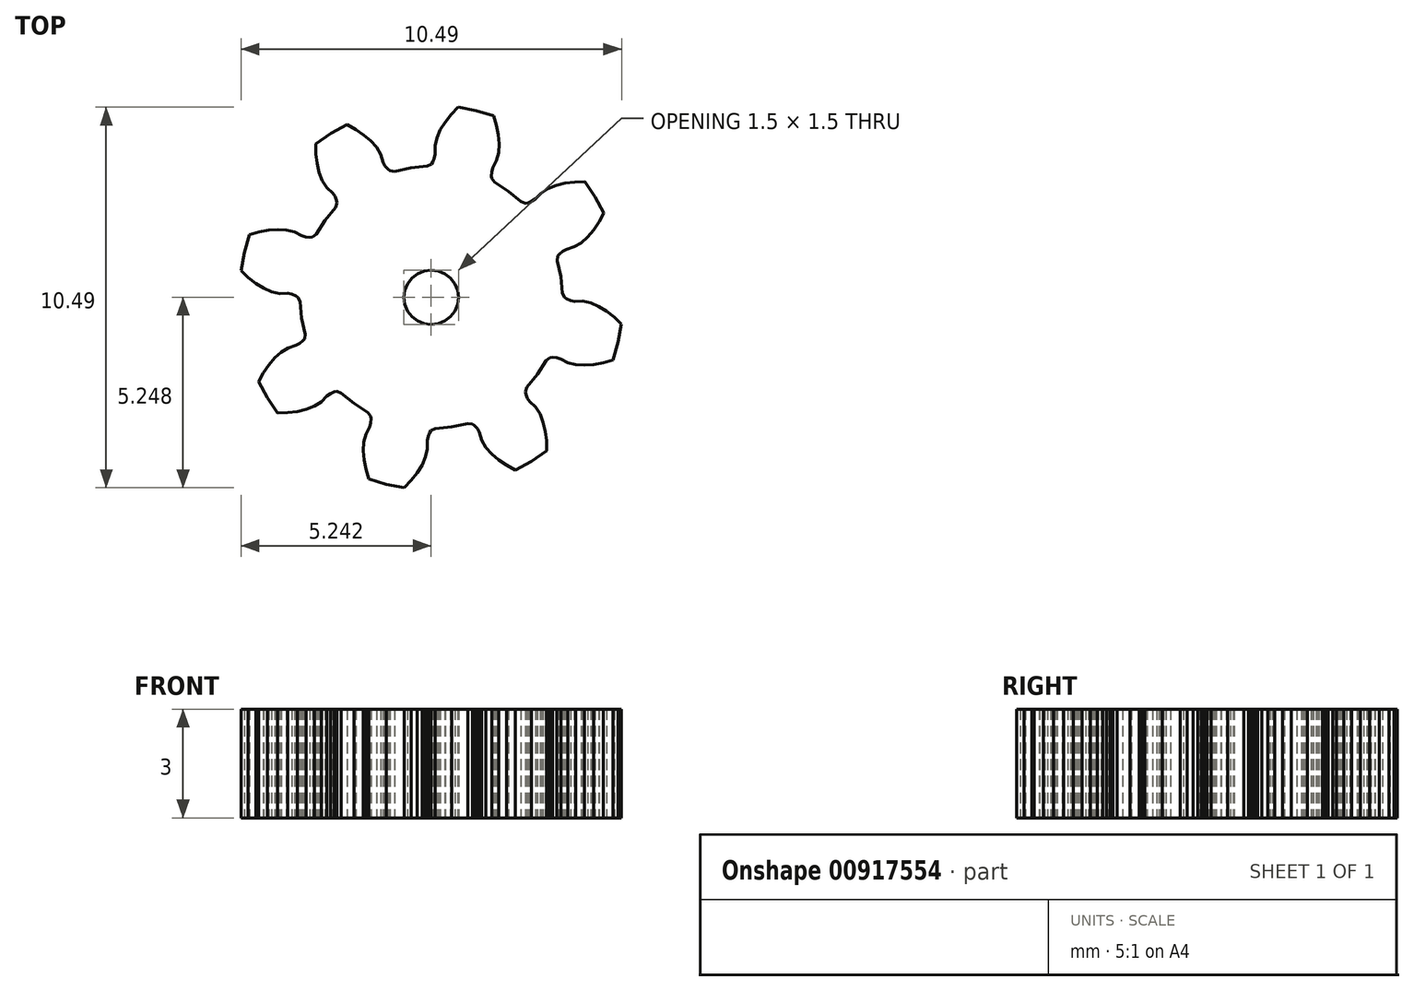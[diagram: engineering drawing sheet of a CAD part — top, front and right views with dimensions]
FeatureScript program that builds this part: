
annotation { "Feature Type Name" : "Feature", "Feature Type Description" : "" }
export const myFeature = defineFeature(function(context is Context, id is Id, definition is map)
    precondition{}
    {
        {
            var Q0;
            Q0=qCreatedBy(makeId("Top.planeOp"),FACE);
            var sketch = newSketch(context, id + "F0", { "sketchPlane" : qUnion([Q0])});
            skLineSegment(sketch, "E0", {"start": v(97.7, 0.47) * mm, "end": v(98.13, 0.32) * mm});
            skLineSegment(sketch, "E1", {"start": v(98.13, 0.32) * mm, "end": v(98.97, 0.02) * mm});
            skLineSegment(sketch, "E2", {"start": v(98.97, 0.02) * mm, "end": v(99.39, -0.14) * mm});
            skLineSegment(sketch, "E3", {"start": v(99.39, -0.14) * mm, "end": v(99.38, -1.27) * mm});
            skLineSegment(sketch, "E4", {"start": v(99.38, -1.27) * mm, "end": v(98.96, -1.43) * mm});
            skLineSegment(sketch, "E5", {"start": v(98.96, -1.43) * mm, "end": v(98.11, -1.72) * mm});
            skLineSegment(sketch, "E6", {"start": v(98.11, -1.72) * mm, "end": v(97.69, -1.86) * mm});
            skLineSegment(sketch, "E7", {"start": v(97.69, -1.86) * mm, "end": v(97.66, -3) * mm});
            skLineSegment(sketch, "E8", {"start": v(97.66, -3) * mm, "end": v(98.08, -3.16) * mm});
            skLineSegment(sketch, "E9", {"start": v(98.08, -3.16) * mm, "end": v(98.9, -3.5) * mm});
            skLineSegment(sketch, "E10", {"start": v(98.9, -3.5) * mm, "end": v(99.32, -3.67) * mm});
            skLineSegment(sketch, "E11", {"start": v(99.32, -3.67) * mm, "end": v(99.28, -4.8) * mm});
            skLineSegment(sketch, "E12", {"start": v(99.28, -4.8) * mm, "end": v(98.85, -4.94) * mm});
            skLineSegment(sketch, "E13", {"start": v(98.85, -4.94) * mm, "end": v(98, -5.2) * mm});
            skLineSegment(sketch, "E14", {"start": v(98, -5.2) * mm, "end": v(97.57, -5.33) * mm});
            skLineSegment(sketch, "E15", {"start": v(97.57, -5.33) * mm, "end": v(97.5, -6.47) * mm});
            skLineSegment(sketch, "E16", {"start": v(97.5, -6.47) * mm, "end": v(97.91, -6.65) * mm});
            skLineSegment(sketch, "E17", {"start": v(97.91, -6.65) * mm, "end": v(98.73, -7) * mm});
            skLineSegment(sketch, "E18", {"start": v(98.73, -7) * mm, "end": v(99.14, -7.2) * mm});
            skLineSegment(sketch, "E19", {"start": v(99.14, -7.2) * mm, "end": v(99.06, -8.32) * mm});
            skLineSegment(sketch, "E20", {"start": v(99.06, -8.32) * mm, "end": v(98.62, -8.45) * mm});
            skLineSegment(sketch, "E21", {"start": v(98.62, -8.45) * mm, "end": v(97.76, -8.68) * mm});
            skLineSegment(sketch, "E22", {"start": v(97.76, -8.68) * mm, "end": v(97.33, -8.8) * mm});
            skLineSegment(sketch, "E23", {"start": v(97.33, -8.8) * mm, "end": v(97.23, -9.93) * mm});
            skLineSegment(sketch, "E24", {"start": v(97.23, -9.93) * mm, "end": v(97.63, -10.12) * mm});
            skLineSegment(sketch, "E25", {"start": v(97.63, -10.12) * mm, "end": v(98.44, -10.5) * mm});
            skLineSegment(sketch, "E26", {"start": v(98.44, -10.5) * mm, "end": v(98.84, -10.7) * mm});
            skLineSegment(sketch, "E27", {"start": v(98.84, -10.7) * mm, "end": v(98.72, -11.83) * mm});
            skLineSegment(sketch, "E28", {"start": v(98.72, -11.83) * mm, "end": v(98.28, -11.94) * mm});
            skLineSegment(sketch, "E29", {"start": v(98.28, -11.94) * mm, "end": v(97.41, -12.15) * mm});
            skLineSegment(sketch, "E30", {"start": v(97.41, -12.15) * mm, "end": v(96.98, -12.24) * mm});
            skLineSegment(sketch, "E31", {"start": v(96.98, -12.24) * mm, "end": v(96.84, -13.38) * mm});
            skLineSegment(sketch, "E32", {"start": v(96.84, -13.38) * mm, "end": v(97.23, -13.58) * mm});
            skLineSegment(sketch, "E33", {"start": v(97.23, -13.58) * mm, "end": v(98.03, -14) * mm});
            skLineSegment(sketch, "E34", {"start": v(98.03, -14) * mm, "end": v(98.42, -14.21) * mm});
            skLineSegment(sketch, "E35", {"start": v(98.42, -14.21) * mm, "end": v(98.26, -15.33) * mm});
            skLineSegment(sketch, "E36", {"start": v(98.26, -15.33) * mm, "end": v(97.82, -15.43) * mm});
            skLineSegment(sketch, "E37", {"start": v(97.82, -15.43) * mm, "end": v(96.95, -15.6) * mm});
            skLineSegment(sketch, "E38", {"start": v(96.95, -15.6) * mm, "end": v(96.5, -15.68) * mm});
            skLineSegment(sketch, "E39", {"start": v(96.5, -15.68) * mm, "end": v(96.33, -16.82) * mm});
            skLineSegment(sketch, "E40", {"start": v(96.33, -16.82) * mm, "end": v(96.72, -17.03) * mm});
            skLineSegment(sketch, "E41", {"start": v(96.72, -17.03) * mm, "end": v(97.5, -17.47) * mm});
            skLineSegment(sketch, "E42", {"start": v(97.5, -17.47) * mm, "end": v(97.88, -17.7) * mm});
            skLineSegment(sketch, "E43", {"start": v(97.88, -17.7) * mm, "end": v(97.69, -18.81) * mm});
            skLineSegment(sketch, "E44", {"start": v(97.69, -18.81) * mm, "end": v(97.25, -18.9) * mm});
            skLineSegment(sketch, "E45", {"start": v(97.25, -18.9) * mm, "end": v(96.36, -19.04) * mm});
            skLineSegment(sketch, "E46", {"start": v(96.36, -19.04) * mm, "end": v(95.93, -19.1) * mm});
            skLineSegment(sketch, "E47", {"start": v(95.93, -19.1) * mm, "end": v(95.7, -20.23) * mm});
            skLineSegment(sketch, "E48", {"start": v(95.7, -20.23) * mm, "end": v(96.09, -20.46) * mm});
            skLineSegment(sketch, "E49", {"start": v(96.09, -20.46) * mm, "end": v(96.85, -20.92) * mm});
            skLineSegment(sketch, "E50", {"start": v(96.85, -20.92) * mm, "end": v(97.23, -21.17) * mm});
            skLineSegment(sketch, "E51", {"start": v(97.23, -21.17) * mm, "end": v(97, -22.27) * mm});
            skLineSegment(sketch, "E52", {"start": v(97, -22.27) * mm, "end": v(96.55, -22.34) * mm});
            skLineSegment(sketch, "E53", {"start": v(96.55, -22.34) * mm, "end": v(95.67, -22.46) * mm});
            skLineSegment(sketch, "E54", {"start": v(95.67, -22.46) * mm, "end": v(95.23, -22.5) * mm});
            skLineSegment(sketch, "E55", {"start": v(95.23, -22.5) * mm, "end": v(94.97, -23.63) * mm});
            skLineSegment(sketch, "E56", {"start": v(94.97, -23.63) * mm, "end": v(95.35, -23.86) * mm});
            skLineSegment(sketch, "E57", {"start": v(95.35, -23.86) * mm, "end": v(96.1, -24.36) * mm});
            skLineSegment(sketch, "E58", {"start": v(96.1, -24.36) * mm, "end": v(96.46, -24.6) * mm});
            skLineSegment(sketch, "E59", {"start": v(96.46, -24.6) * mm, "end": v(96.2, -25.7) * mm});
            skLineSegment(sketch, "E60", {"start": v(96.2, -25.7) * mm, "end": v(95.74, -25.76) * mm});
            skLineSegment(sketch, "E61", {"start": v(95.74, -25.76) * mm, "end": v(94.86, -25.85) * mm});
            skLineSegment(sketch, "E62", {"start": v(94.86, -25.85) * mm, "end": v(94.41, -25.88) * mm});
            skLineSegment(sketch, "E63", {"start": v(94.41, -25.88) * mm, "end": v(94.12, -27) * mm});
            skLineSegment(sketch, "E64", {"start": v(94.12, -27) * mm, "end": v(94.49, -27.24) * mm});
            skLineSegment(sketch, "E65", {"start": v(94.49, -27.24) * mm, "end": v(95.22, -27.76) * mm});
            skLineSegment(sketch, "E66", {"start": v(95.22, -27.76) * mm, "end": v(95.58, -28.02) * mm});
            skLineSegment(sketch, "E67", {"start": v(95.58, -28.02) * mm, "end": v(95.27, -29.11) * mm});
            skLineSegment(sketch, "E68", {"start": v(95.27, -29.11) * mm, "end": v(94.82, -29.15) * mm});
            skLineSegment(sketch, "E69", {"start": v(94.82, -29.15) * mm, "end": v(93.93, -29.2) * mm});
            skLineSegment(sketch, "E70", {"start": v(93.93, -29.2) * mm, "end": v(93.49, -29.23) * mm});
            skLineSegment(sketch, "E71", {"start": v(93.49, -29.23) * mm, "end": v(93.16, -30.33) * mm});
            skLineSegment(sketch, "E72", {"start": v(93.16, -30.33) * mm, "end": v(93.51, -30.59) * mm});
            skLineSegment(sketch, "E73", {"start": v(93.51, -30.59) * mm, "end": v(94.23, -31.13) * mm});
            skLineSegment(sketch, "E74", {"start": v(94.23, -31.13) * mm, "end": v(94.58, -31.4) * mm});
            skLineSegment(sketch, "E75", {"start": v(94.58, -31.4) * mm, "end": v(94.24, -32.48) * mm});
            skLineSegment(sketch, "E76", {"start": v(94.24, -32.48) * mm, "end": v(93.79, -32.5) * mm});
            skLineSegment(sketch, "E77", {"start": v(93.79, -32.5) * mm, "end": v(92.9, -32.54) * mm});
            skLineSegment(sketch, "E78", {"start": v(92.9, -32.54) * mm, "end": v(92.45, -32.54) * mm});
            skLineSegment(sketch, "E79", {"start": v(92.45, -32.54) * mm, "end": v(92.08, -33.63) * mm});
            skLineSegment(sketch, "E80", {"start": v(92.08, -33.63) * mm, "end": v(92.43, -33.9) * mm});
            skLineSegment(sketch, "E81", {"start": v(92.43, -33.9) * mm, "end": v(93.12, -34.47) * mm});
            skLineSegment(sketch, "E82", {"start": v(93.12, -34.47) * mm, "end": v(93.47, -34.76) * mm});
            skLineSegment(sketch, "E83", {"start": v(93.47, -34.76) * mm, "end": v(93.09, -35.82) * mm});
            skLineSegment(sketch, "E84", {"start": v(93.09, -35.82) * mm, "end": v(92.64, -35.83) * mm});
            skLineSegment(sketch, "E85", {"start": v(92.64, -35.83) * mm, "end": v(91.74, -35.83) * mm});
            skLineSegment(sketch, "E86", {"start": v(91.74, -35.83) * mm, "end": v(91.3, -35.82) * mm});
            skLineSegment(sketch, "E87", {"start": v(91.3, -35.82) * mm, "end": v(90.9, -36.9) * mm});
            skLineSegment(sketch, "E88", {"start": v(90.9, -36.9) * mm, "end": v(91.24, -37.18) * mm});
            skLineSegment(sketch, "E89", {"start": v(91.24, -37.18) * mm, "end": v(91.91, -37.76) * mm});
            skLineSegment(sketch, "E90", {"start": v(91.91, -37.76) * mm, "end": v(92.24, -38.07) * mm});
            skLineSegment(sketch, "E91", {"start": v(92.24, -38.07) * mm, "end": v(91.83, -39.12) * mm});
            skLineSegment(sketch, "E92", {"start": v(91.83, -39.12) * mm, "end": v(91.38, -39.1) * mm});
            skLineSegment(sketch, "E93", {"start": v(91.38, -39.1) * mm, "end": v(90.49, -39.08) * mm});
            skLineSegment(sketch, "E94", {"start": v(90.49, -39.08) * mm, "end": v(90.04, -39.05) * mm});
            skLineSegment(sketch, "E95", {"start": v(90.04, -39.05) * mm, "end": v(89.6, -40.11) * mm});
            skLineSegment(sketch, "E96", {"start": v(89.6, -40.11) * mm, "end": v(89.93, -40.41) * mm});
            skLineSegment(sketch, "E97", {"start": v(89.93, -40.41) * mm, "end": v(90.59, -41.02) * mm});
            skLineSegment(sketch, "E98", {"start": v(90.59, -41.02) * mm, "end": v(90.91, -41.33) * mm});
            skLineSegment(sketch, "E99", {"start": v(90.91, -41.33) * mm, "end": v(90.46, -42.37) * mm});
            skLineSegment(sketch, "E100", {"start": v(90.46, -42.37) * mm, "end": v(90.01, -42.35) * mm});
            skLineSegment(sketch, "E101", {"start": v(90.01, -42.35) * mm, "end": v(89.12, -42.28) * mm});
            skLineSegment(sketch, "E102", {"start": v(89.12, -42.28) * mm, "end": v(88.68, -42.24) * mm});
            skLineSegment(sketch, "E103", {"start": v(88.68, -42.24) * mm, "end": v(88.2, -43.3) * mm});
            skLineSegment(sketch, "E104", {"start": v(88.2, -43.3) * mm, "end": v(88.52, -43.6) * mm});
            skLineSegment(sketch, "E105", {"start": v(88.52, -43.6) * mm, "end": v(89.15, -44.23) * mm});
            skLineSegment(sketch, "E106", {"start": v(89.15, -44.23) * mm, "end": v(89.47, -44.55) * mm});
            skLineSegment(sketch, "E107", {"start": v(89.47, -44.55) * mm, "end": v(88.98, -45.57) * mm});
            skLineSegment(sketch, "E108", {"start": v(88.98, -45.57) * mm, "end": v(88.53, -45.53) * mm});
            skLineSegment(sketch, "E109", {"start": v(88.53, -45.53) * mm, "end": v(87.65, -45.44) * mm});
            skLineSegment(sketch, "E110", {"start": v(87.65, -45.44) * mm, "end": v(87.2, -45.39) * mm});
            skLineSegment(sketch, "E111", {"start": v(87.2, -45.39) * mm, "end": v(86.7, -46.42) * mm});
            skLineSegment(sketch, "E112", {"start": v(86.7, -46.42) * mm, "end": v(87, -46.74) * mm});
            skLineSegment(sketch, "E113", {"start": v(87, -46.74) * mm, "end": v(87.62, -47.39) * mm});
            skLineSegment(sketch, "E114", {"start": v(87.62, -47.39) * mm, "end": v(87.92, -47.72) * mm});
            skLineSegment(sketch, "E115", {"start": v(87.92, -47.72) * mm, "end": v(87.4, -48.72) * mm});
            skLineSegment(sketch, "E116", {"start": v(87.4, -48.72) * mm, "end": v(86.95, -48.67) * mm});
            skLineSegment(sketch, "E117", {"start": v(86.95, -48.67) * mm, "end": v(86.07, -48.55) * mm});
            skLineSegment(sketch, "E118", {"start": v(86.07, -48.55) * mm, "end": v(85.63, -48.48) * mm});
            skLineSegment(sketch, "E119", {"start": v(85.63, -48.48) * mm, "end": v(85.08, -49.5) * mm});
            skLineSegment(sketch, "E120", {"start": v(85.08, -49.5) * mm, "end": v(85.38, -49.82) * mm});
            skLineSegment(sketch, "E121", {"start": v(85.38, -49.82) * mm, "end": v(85.97, -50.5) * mm});
            skLineSegment(sketch, "E122", {"start": v(85.97, -50.5) * mm, "end": v(86.26, -50.84) * mm});
            skLineSegment(sketch, "E123", {"start": v(86.26, -50.84) * mm, "end": v(85.7, -51.82) * mm});
            skLineSegment(sketch, "E124", {"start": v(85.7, -51.82) * mm, "end": v(85.26, -51.75) * mm});
            skLineSegment(sketch, "E125", {"start": v(85.26, -51.75) * mm, "end": v(84.38, -51.6) * mm});
            skLineSegment(sketch, "E126", {"start": v(84.38, -51.6) * mm, "end": v(83.95, -51.52) * mm});
            skLineSegment(sketch, "E127", {"start": v(83.95, -51.52) * mm, "end": v(83.37, -52.51) * mm});
            skLineSegment(sketch, "E128", {"start": v(83.37, -52.51) * mm, "end": v(83.66, -52.85) * mm});
            skLineSegment(sketch, "E129", {"start": v(83.66, -52.85) * mm, "end": v(84.22, -53.54) * mm});
            skLineSegment(sketch, "E130", {"start": v(84.22, -53.54) * mm, "end": v(84.5, -53.9) * mm});
            skLineSegment(sketch, "E131", {"start": v(84.5, -53.9) * mm, "end": v(83.92, -54.86) * mm});
            skLineSegment(sketch, "E132", {"start": v(83.92, -54.86) * mm, "end": v(83.47, -54.78) * mm});
            skLineSegment(sketch, "E133", {"start": v(83.47, -54.78) * mm, "end": v(82.6, -54.6) * mm});
            skLineSegment(sketch, "E134", {"start": v(82.6, -54.6) * mm, "end": v(82.17, -54.5) * mm});
            skLineSegment(sketch, "E135", {"start": v(82.17, -54.5) * mm, "end": v(81.56, -55.47) * mm});
            skLineSegment(sketch, "E136", {"start": v(81.56, -55.47) * mm, "end": v(81.83, -55.82) * mm});
            skLineSegment(sketch, "E137", {"start": v(81.83, -55.82) * mm, "end": v(82.37, -56.53) * mm});
            skLineSegment(sketch, "E138", {"start": v(82.37, -56.53) * mm, "end": v(82.64, -56.9) * mm});
            skLineSegment(sketch, "E139", {"start": v(82.64, -56.9) * mm, "end": v(82.02, -57.84) * mm});
            skLineSegment(sketch, "E140", {"start": v(82.02, -57.84) * mm, "end": v(81.58, -57.74) * mm});
            skLineSegment(sketch, "E141", {"start": v(81.58, -57.74) * mm, "end": v(80.72, -57.53) * mm});
            skLineSegment(sketch, "E142", {"start": v(80.72, -57.53) * mm, "end": v(80.29, -57.42) * mm});
            skLineSegment(sketch, "E143", {"start": v(80.29, -57.42) * mm, "end": v(79.64, -58.37) * mm});
            skLineSegment(sketch, "E144", {"start": v(79.64, -58.37) * mm, "end": v(79.9, -58.73) * mm});
            skLineSegment(sketch, "E145", {"start": v(79.9, -58.73) * mm, "end": v(80.43, -59.45) * mm});
            skLineSegment(sketch, "E146", {"start": v(80.43, -59.45) * mm, "end": v(80.68, -59.82) * mm});
            skLineSegment(sketch, "E147", {"start": v(80.68, -59.82) * mm, "end": v(80.03, -60.75) * mm});
            skLineSegment(sketch, "E148", {"start": v(80.03, -60.75) * mm, "end": v(79.6, -60.64) * mm});
            skLineSegment(sketch, "E149", {"start": v(79.6, -60.64) * mm, "end": v(78.73, -60.4) * mm});
            skLineSegment(sketch, "E150", {"start": v(78.73, -60.4) * mm, "end": v(78.3, -60.27) * mm});
            skLineSegment(sketch, "E151", {"start": v(78.3, -60.27) * mm, "end": v(77.63, -61.2) * mm});
            skLineSegment(sketch, "E152", {"start": v(77.63, -61.2) * mm, "end": v(77.89, -61.57) * mm});
            skLineSegment(sketch, "E153", {"start": v(77.89, -61.57) * mm, "end": v(78.38, -62.31) * mm});
            skLineSegment(sketch, "E154", {"start": v(78.38, -62.31) * mm, "end": v(78.62, -62.69) * mm});
            skLineSegment(sketch, "E155", {"start": v(78.62, -62.69) * mm, "end": v(77.94, -63.6) * mm});
            skLineSegment(sketch, "E156", {"start": v(77.94, -63.6) * mm, "end": v(77.51, -63.47) * mm});
            skLineSegment(sketch, "E157", {"start": v(77.51, -63.47) * mm, "end": v(76.66, -63.2) * mm});
            skLineSegment(sketch, "E158", {"start": v(76.66, -63.2) * mm, "end": v(76.24, -63.06) * mm});
            skLineSegment(sketch, "E159", {"start": v(76.24, -63.06) * mm, "end": v(75.53, -63.96) * mm});
            skLineSegment(sketch, "E160", {"start": v(75.53, -63.96) * mm, "end": v(75.77, -64.34) * mm});
            skLineSegment(sketch, "E161", {"start": v(75.77, -64.34) * mm, "end": v(76.24, -65.1) * mm});
            skLineSegment(sketch, "E162", {"start": v(76.24, -65.1) * mm, "end": v(76.47, -65.48) * mm});
            skLineSegment(sketch, "E163", {"start": v(76.47, -65.48) * mm, "end": v(75.76, -66.36) * mm});
            skLineSegment(sketch, "E164", {"start": v(75.76, -66.36) * mm, "end": v(75.33, -66.22) * mm});
            skLineSegment(sketch, "E165", {"start": v(75.33, -66.22) * mm, "end": v(74.49, -65.93) * mm});
            skLineSegment(sketch, "E166", {"start": v(74.49, -65.93) * mm, "end": v(74.07, -65.77) * mm});
            skLineSegment(sketch, "E167", {"start": v(74.07, -65.77) * mm, "end": v(73.34, -66.65) * mm});
            skLineSegment(sketch, "E168", {"start": v(73.34, -66.65) * mm, "end": v(73.56, -67.03) * mm});
            skLineSegment(sketch, "E169", {"start": v(73.56, -67.03) * mm, "end": v(74, -67.81) * mm});
            skLineSegment(sketch, "E170", {"start": v(74, -67.81) * mm, "end": v(74.22, -68.2) * mm});
            skLineSegment(sketch, "E171", {"start": v(74.22, -68.2) * mm, "end": v(73.48, -69.06) * mm});
            skLineSegment(sketch, "E172", {"start": v(73.48, -69.06) * mm, "end": v(73.06, -68.9) * mm});
            skLineSegment(sketch, "E173", {"start": v(73.06, -68.9) * mm, "end": v(72.23, -68.58) * mm});
            skLineSegment(sketch, "E174", {"start": v(72.23, -68.58) * mm, "end": v(71.82, -68.41) * mm});
            skLineSegment(sketch, "E175", {"start": v(71.82, -68.41) * mm, "end": v(71.05, -69.27) * mm});
            skLineSegment(sketch, "E176", {"start": v(71.05, -69.27) * mm, "end": v(71.27, -69.66) * mm});
            skLineSegment(sketch, "E177", {"start": v(71.27, -69.66) * mm, "end": v(71.68, -70.45) * mm});
            skLineSegment(sketch, "E178", {"start": v(71.68, -70.45) * mm, "end": v(71.89, -70.85) * mm});
            skLineSegment(sketch, "E179", {"start": v(71.89, -70.85) * mm, "end": v(71.12, -71.68) * mm});
            skLineSegment(sketch, "E180", {"start": v(71.12, -71.68) * mm, "end": v(70.7, -71.5) * mm});
            skLineSegment(sketch, "E181", {"start": v(70.7, -71.5) * mm, "end": v(69.88, -71.16) * mm});
            skLineSegment(sketch, "E182", {"start": v(69.88, -71.16) * mm, "end": v(69.48, -70.97) * mm});
            skLineSegment(sketch, "E183", {"start": v(69.48, -70.97) * mm, "end": v(68.68, -71.8) * mm});
            skLineSegment(sketch, "E184", {"start": v(68.68, -71.8) * mm, "end": v(68.88, -72.2) * mm});
            skLineSegment(sketch, "E185", {"start": v(68.88, -72.2) * mm, "end": v(69.27, -73) * mm});
            skLineSegment(sketch, "E186", {"start": v(69.27, -73) * mm, "end": v(69.46, -73.41) * mm});
            skLineSegment(sketch, "E187", {"start": v(69.46, -73.41) * mm, "end": v(68.67, -74.22) * mm});
            skLineSegment(sketch, "E188", {"start": v(68.67, -74.22) * mm, "end": v(68.26, -74.03) * mm});
            skLineSegment(sketch, "E189", {"start": v(68.26, -74.03) * mm, "end": v(67.45, -73.65) * mm});
            skLineSegment(sketch, "E190", {"start": v(67.45, -73.65) * mm, "end": v(67.05, -73.46) * mm});
            skLineSegment(sketch, "E191", {"start": v(67.05, -73.46) * mm, "end": v(66.23, -74.26) * mm});
            skLineSegment(sketch, "E192", {"start": v(66.23, -74.26) * mm, "end": v(66.42, -74.66) * mm});
            skLineSegment(sketch, "E193", {"start": v(66.42, -74.66) * mm, "end": v(66.78, -75.48) * mm});
            skLineSegment(sketch, "E194", {"start": v(66.78, -75.48) * mm, "end": v(66.95, -75.9) * mm});
            skLineSegment(sketch, "E195", {"start": v(66.95, -75.9) * mm, "end": v(66.13, -76.67) * mm});
            skLineSegment(sketch, "E196", {"start": v(66.13, -76.67) * mm, "end": v(65.73, -76.47) * mm});
            skLineSegment(sketch, "E197", {"start": v(65.73, -76.47) * mm, "end": v(64.93, -76.07) * mm});
            skLineSegment(sketch, "E198", {"start": v(64.93, -76.07) * mm, "end": v(64.54, -75.86) * mm});
            skLineSegment(sketch, "E199", {"start": v(64.54, -75.86) * mm, "end": v(63.7, -76.63) * mm});
            skLineSegment(sketch, "E200", {"start": v(63.7, -76.63) * mm, "end": v(63.87, -77.04) * mm});
            skLineSegment(sketch, "E201", {"start": v(63.87, -77.04) * mm, "end": v(64.2, -77.87) * mm});
            skLineSegment(sketch, "E202", {"start": v(64.2, -77.87) * mm, "end": v(64.36, -78.29) * mm});
            skLineSegment(sketch, "E203", {"start": v(64.36, -78.29) * mm, "end": v(63.52, -79.04) * mm});
            skLineSegment(sketch, "E204", {"start": v(63.52, -79.04) * mm, "end": v(63.12, -78.83) * mm});
            skLineSegment(sketch, "E205", {"start": v(63.12, -78.83) * mm, "end": v(62.34, -78.4) * mm});
            skLineSegment(sketch, "E206", {"start": v(62.34, -78.4) * mm, "end": v(61.95, -78.17) * mm});
            skLineSegment(sketch, "E207", {"start": v(61.95, -78.17) * mm, "end": v(61.08, -78.92) * mm});
            skLineSegment(sketch, "E208", {"start": v(61.08, -78.92) * mm, "end": v(61.24, -79.33) * mm});
            skLineSegment(sketch, "E209", {"start": v(61.24, -79.33) * mm, "end": v(61.55, -80.17) * mm});
            skLineSegment(sketch, "E210", {"start": v(61.55, -80.17) * mm, "end": v(61.7, -80.6) * mm});
            skLineSegment(sketch, "E211", {"start": v(61.7, -80.6) * mm, "end": v(60.82, -81.31) * mm});
            skLineSegment(sketch, "E212", {"start": v(60.82, -81.31) * mm, "end": v(60.43, -81.1) * mm});
            skLineSegment(sketch, "E213", {"start": v(60.43, -81.1) * mm, "end": v(59.67, -80.63) * mm});
            skLineSegment(sketch, "E214", {"start": v(59.67, -80.63) * mm, "end": v(59.29, -80.4) * mm});
            skLineSegment(sketch, "E215", {"start": v(59.29, -80.4) * mm, "end": v(58.4, -81.11) * mm});
            skLineSegment(sketch, "E216", {"start": v(58.4, -81.11) * mm, "end": v(58.54, -81.53) * mm});
            skLineSegment(sketch, "E217", {"start": v(58.54, -81.53) * mm, "end": v(58.82, -82.38) * mm});
            skLineSegment(sketch, "E218", {"start": v(58.82, -82.38) * mm, "end": v(58.95, -82.81) * mm});
            skLineSegment(sketch, "E219", {"start": v(58.95, -82.81) * mm, "end": v(58.05, -83.5) * mm});
            skLineSegment(sketch, "E220", {"start": v(58.05, -83.5) * mm, "end": v(57.67, -83.26) * mm});
            skLineSegment(sketch, "E221", {"start": v(57.67, -83.26) * mm, "end": v(56.92, -82.78) * mm});
            skLineSegment(sketch, "E222", {"start": v(56.92, -82.78) * mm, "end": v(56.55, -82.53) * mm});
            skLineSegment(sketch, "E223", {"start": v(56.55, -82.53) * mm, "end": v(55.63, -83.22) * mm});
            skLineSegment(sketch, "E224", {"start": v(55.63, -83.22) * mm, "end": v(55.76, -83.64) * mm});
            skLineSegment(sketch, "E225", {"start": v(55.76, -83.64) * mm, "end": v(56.01, -84.5) * mm});
            skLineSegment(sketch, "E226", {"start": v(56.01, -84.5) * mm, "end": v(56.13, -84.93) * mm});
            skLineSegment(sketch, "E227", {"start": v(56.13, -84.93) * mm, "end": v(55.21, -85.6) * mm});
            skLineSegment(sketch, "E228", {"start": v(55.21, -85.6) * mm, "end": v(54.84, -85.34) * mm});
            skLineSegment(sketch, "E229", {"start": v(54.84, -85.34) * mm, "end": v(54.1, -84.83) * mm});
            skLineSegment(sketch, "E230", {"start": v(54.1, -84.83) * mm, "end": v(53.74, -84.57) * mm});
            skLineSegment(sketch, "E231", {"start": v(53.74, -84.57) * mm, "end": v(52.8, -85.23) * mm});
            skLineSegment(sketch, "E232", {"start": v(52.8, -85.23) * mm, "end": v(52.92, -85.66) * mm});
            skLineSegment(sketch, "E233", {"start": v(52.92, -85.66) * mm, "end": v(53.14, -86.52) * mm});
            skLineSegment(sketch, "E234", {"start": v(53.14, -86.52) * mm, "end": v(53.24, -86.96) * mm});
            skLineSegment(sketch, "E235", {"start": v(53.24, -86.96) * mm, "end": v(52.3, -87.59) * mm});
            skLineSegment(sketch, "E236", {"start": v(52.3, -87.59) * mm, "end": v(51.94, -87.33) * mm});
            skLineSegment(sketch, "E237", {"start": v(51.94, -87.33) * mm, "end": v(51.22, -86.8) * mm});
            skLineSegment(sketch, "E238", {"start": v(51.22, -86.8) * mm, "end": v(50.87, -86.52) * mm});
            skLineSegment(sketch, "E239", {"start": v(50.87, -86.52) * mm, "end": v(49.9, -87.14) * mm});
            skLineSegment(sketch, "E240", {"start": v(49.9, -87.14) * mm, "end": v(50, -87.57) * mm});
            skLineSegment(sketch, "E241", {"start": v(50, -87.57) * mm, "end": v(50.2, -88.45) * mm});
            skLineSegment(sketch, "E242", {"start": v(50.2, -88.45) * mm, "end": v(50.29, -88.89) * mm});
            skLineSegment(sketch, "E243", {"start": v(50.29, -88.89) * mm, "end": v(49.33, -89.48) * mm});
            skLineSegment(sketch, "E244", {"start": v(49.33, -89.48) * mm, "end": v(48.97, -89.21) * mm});
            skLineSegment(sketch, "E245", {"start": v(48.97, -89.21) * mm, "end": v(48.27, -88.65) * mm});
            skLineSegment(sketch, "E246", {"start": v(48.27, -88.65) * mm, "end": v(47.93, -88.37) * mm});
            skLineSegment(sketch, "E247", {"start": v(47.93, -88.37) * mm, "end": v(46.95, -88.96) * mm});
            skLineSegment(sketch, "E248", {"start": v(46.95, -88.96) * mm, "end": v(47.03, -89.4) * mm});
            skLineSegment(sketch, "E249", {"start": v(47.03, -89.4) * mm, "end": v(47.2, -90.27) * mm});
            skLineSegment(sketch, "E250", {"start": v(47.2, -90.27) * mm, "end": v(47.27, -90.72) * mm});
            skLineSegment(sketch, "E251", {"start": v(47.27, -90.72) * mm, "end": v(46.3, -91.28) * mm});
            skLineSegment(sketch, "E252", {"start": v(46.3, -91.28) * mm, "end": v(45.94, -91) * mm});
            skLineSegment(sketch, "E253", {"start": v(45.94, -91) * mm, "end": v(45.26, -90.41) * mm});
            skLineSegment(sketch, "E254", {"start": v(45.26, -90.41) * mm, "end": v(44.93, -90.12) * mm});
            skLineSegment(sketch, "E255", {"start": v(44.93, -90.12) * mm, "end": v(43.93, -90.67) * mm});
            skLineSegment(sketch, "E256", {"start": v(43.93, -90.67) * mm, "end": v(44, -91.11) * mm});
            skLineSegment(sketch, "E257", {"start": v(44, -91.11) * mm, "end": v(44.13, -92) * mm});
            skLineSegment(sketch, "E258", {"start": v(44.13, -92) * mm, "end": v(44.2, -92.44) * mm});
            skLineSegment(sketch, "E259", {"start": v(44.2, -92.44) * mm, "end": v(43.2, -92.97) * mm});
            skLineSegment(sketch, "E260", {"start": v(43.2, -92.97) * mm, "end": v(42.86, -92.67) * mm});
            skLineSegment(sketch, "E261", {"start": v(42.86, -92.67) * mm, "end": v(42.2, -92.07) * mm});
            skLineSegment(sketch, "E262", {"start": v(42.2, -92.07) * mm, "end": v(41.88, -91.77) * mm});
            skLineSegment(sketch, "E263", {"start": v(41.88, -91.77) * mm, "end": v(40.85, -92.29) * mm});
            skLineSegment(sketch, "E264", {"start": v(40.85, -92.29) * mm, "end": v(40.91, -92.73) * mm});
            skLineSegment(sketch, "E265", {"start": v(40.91, -92.73) * mm, "end": v(41.02, -93.62) * mm});
            skLineSegment(sketch, "E266", {"start": v(41.02, -93.62) * mm, "end": v(41.06, -94.06) * mm});
            skLineSegment(sketch, "E267", {"start": v(41.06, -94.06) * mm, "end": v(40.04, -94.56) * mm});
            skLineSegment(sketch, "E268", {"start": v(40.04, -94.56) * mm, "end": v(39.72, -94.25) * mm});
            skLineSegment(sketch, "E269", {"start": v(39.72, -94.25) * mm, "end": v(39.08, -93.63) * mm});
            skLineSegment(sketch, "E270", {"start": v(39.08, -93.63) * mm, "end": v(38.77, -93.3) * mm});
            skLineSegment(sketch, "E271", {"start": v(38.77, -93.3) * mm, "end": v(37.73, -93.8) * mm});
            skLineSegment(sketch, "E272", {"start": v(37.73, -93.8) * mm, "end": v(37.77, -94.24) * mm});
            skLineSegment(sketch, "E273", {"start": v(37.77, -94.24) * mm, "end": v(37.84, -95.13) * mm});
            skLineSegment(sketch, "E274", {"start": v(37.84, -95.13) * mm, "end": v(37.87, -95.58) * mm});
            skLineSegment(sketch, "E275", {"start": v(37.87, -95.58) * mm, "end": v(36.84, -96.04) * mm});
            skLineSegment(sketch, "E276", {"start": v(36.84, -96.04) * mm, "end": v(36.53, -95.72) * mm});
            skLineSegment(sketch, "E277", {"start": v(36.53, -95.72) * mm, "end": v(35.9, -95.07) * mm});
            skLineSegment(sketch, "E278", {"start": v(35.9, -95.07) * mm, "end": v(35.6, -94.75) * mm});
            skLineSegment(sketch, "E279", {"start": v(35.6, -94.75) * mm, "end": v(34.55, -95.2) * mm});
            skLineSegment(sketch, "E280", {"start": v(34.55, -95.2) * mm, "end": v(34.58, -95.64) * mm});
            skLineSegment(sketch, "E281", {"start": v(34.58, -95.64) * mm, "end": v(34.62, -96.54) * mm});
            skLineSegment(sketch, "E282", {"start": v(34.62, -96.54) * mm, "end": v(34.64, -96.98) * mm});
            skLineSegment(sketch, "E283", {"start": v(34.64, -96.98) * mm, "end": v(33.6, -97.41) * mm});
            skLineSegment(sketch, "E284", {"start": v(33.6, -97.41) * mm, "end": v(33.29, -97.08) * mm});
            skLineSegment(sketch, "E285", {"start": v(33.29, -97.08) * mm, "end": v(32.7, -96.42) * mm});
            skLineSegment(sketch, "E286", {"start": v(32.7, -96.42) * mm, "end": v(32.4, -96.08) * mm});
            skLineSegment(sketch, "E287", {"start": v(32.4, -96.08) * mm, "end": v(31.33, -96.5) * mm});
            skLineSegment(sketch, "E288", {"start": v(31.33, -96.5) * mm, "end": v(31.35, -96.94) * mm});
            skLineSegment(sketch, "E289", {"start": v(31.35, -96.94) * mm, "end": v(31.36, -97.83) * mm});
            skLineSegment(sketch, "E290", {"start": v(31.36, -97.83) * mm, "end": v(31.36, -98.28) * mm});
            skLineSegment(sketch, "E291", {"start": v(31.36, -98.28) * mm, "end": v(30.3, -98.67) * mm});
            skLineSegment(sketch, "E292", {"start": v(30.3, -98.67) * mm, "end": v(30, -98.33) * mm});
            skLineSegment(sketch, "E293", {"start": v(30, -98.33) * mm, "end": v(29.43, -97.65) * mm});
            skLineSegment(sketch, "E294", {"start": v(29.43, -97.65) * mm, "end": v(29.15, -97.3) * mm});
            skLineSegment(sketch, "E295", {"start": v(29.15, -97.3) * mm, "end": v(28.07, -97.68) * mm});
            skLineSegment(sketch, "E296", {"start": v(28.07, -97.68) * mm, "end": v(28.07, -98.13) * mm});
            skLineSegment(sketch, "E297", {"start": v(28.07, -98.13) * mm, "end": v(28.05, -99.02) * mm});
            skLineSegment(sketch, "E298", {"start": v(28.05, -99.02) * mm, "end": v(28.03, -99.47) * mm});
            skLineSegment(sketch, "E299", {"start": v(28.03, -99.47) * mm, "end": v(26.96, -99.83) * mm});
            skLineSegment(sketch, "E300", {"start": v(26.96, -99.83) * mm, "end": v(26.68, -99.48) * mm});
            skLineSegment(sketch, "E301", {"start": v(26.68, -99.48) * mm, "end": v(26.13, -98.77) * mm});
            skLineSegment(sketch, "E302", {"start": v(26.13, -98.77) * mm, "end": v(25.86, -98.42) * mm});
            skLineSegment(sketch, "E303", {"start": v(25.86, -98.42) * mm, "end": v(24.77, -98.76) * mm});
            skLineSegment(sketch, "E304", {"start": v(24.77, -98.76) * mm, "end": v(24.75, -99.2) * mm});
            skLineSegment(sketch, "E305", {"start": v(24.75, -99.2) * mm, "end": v(24.7, -100.1) * mm});
            skLineSegment(sketch, "E306", {"start": v(24.7, -100.1) * mm, "end": v(24.67, -100.54) * mm});
            skLineSegment(sketch, "E307", {"start": v(24.67, -100.54) * mm, "end": v(23.6, -100.86) * mm});
            skLineSegment(sketch, "E308", {"start": v(23.6, -100.86) * mm, "end": v(23.32, -100.5) * mm});
            skLineSegment(sketch, "E309", {"start": v(23.32, -100.5) * mm, "end": v(22.8, -99.78) * mm});
            skLineSegment(sketch, "E310", {"start": v(22.8, -99.78) * mm, "end": v(22.54, -99.42) * mm});
            skLineSegment(sketch, "E311", {"start": v(22.54, -99.42) * mm, "end": v(21.43, -99.72) * mm});
            skLineSegment(sketch, "E312", {"start": v(21.43, -99.72) * mm, "end": v(21.4, -100.17) * mm});
            skLineSegment(sketch, "E313", {"start": v(21.4, -100.17) * mm, "end": v(21.33, -101.06) * mm});
            skLineSegment(sketch, "E314", {"start": v(21.33, -101.06) * mm, "end": v(21.28, -101.5) * mm});
            skLineSegment(sketch, "E315", {"start": v(21.28, -101.5) * mm, "end": v(20.19, -101.79) * mm});
            skLineSegment(sketch, "E316", {"start": v(20.19, -101.79) * mm, "end": v(19.93, -101.42) * mm});
            skLineSegment(sketch, "E317", {"start": v(19.93, -101.42) * mm, "end": v(19.43, -100.68) * mm});
            skLineSegment(sketch, "E318", {"start": v(19.43, -100.68) * mm, "end": v(19.18, -100.3) * mm});
            skLineSegment(sketch, "E319", {"start": v(19.18, -100.3) * mm, "end": v(18.07, -100.58) * mm});
            skLineSegment(sketch, "E320", {"start": v(18.07, -100.58) * mm, "end": v(18.02, -101.02) * mm});
            skLineSegment(sketch, "E321", {"start": v(18.02, -101.02) * mm, "end": v(17.92, -101.9) * mm});
            skLineSegment(sketch, "E322", {"start": v(17.92, -101.9) * mm, "end": v(17.85, -102.35) * mm});
            skLineSegment(sketch, "E323", {"start": v(17.85, -102.35) * mm, "end": v(16.75, -102.6) * mm});
            skLineSegment(sketch, "E324", {"start": v(16.75, -102.6) * mm, "end": v(16.5, -102.22) * mm});
            skLineSegment(sketch, "E325", {"start": v(16.5, -102.22) * mm, "end": v(16.03, -101.46) * mm});
            skLineSegment(sketch, "E326", {"start": v(16.03, -101.46) * mm, "end": v(15.8, -101.08) * mm});
            skLineSegment(sketch, "E327", {"start": v(15.8, -101.08) * mm, "end": v(14.68, -101.32) * mm});
            skLineSegment(sketch, "E328", {"start": v(14.68, -101.32) * mm, "end": v(14.62, -101.76) * mm});
            skLineSegment(sketch, "E329", {"start": v(14.62, -101.76) * mm, "end": v(14.48, -102.64) * mm});
            skLineSegment(sketch, "E330", {"start": v(14.48, -102.64) * mm, "end": v(14.4, -103.08) * mm});
            skLineSegment(sketch, "E331", {"start": v(14.4, -103.08) * mm, "end": v(13.3, -103.3) * mm});
            skLineSegment(sketch, "E332", {"start": v(13.3, -103.3) * mm, "end": v(13.06, -102.9) * mm});
            skLineSegment(sketch, "E333", {"start": v(13.06, -102.9) * mm, "end": v(12.6, -102.13) * mm});
            skLineSegment(sketch, "E334", {"start": v(12.6, -102.13) * mm, "end": v(12.4, -101.75) * mm});
            skLineSegment(sketch, "E335", {"start": v(12.4, -101.75) * mm, "end": v(11.26, -101.94) * mm});
            skLineSegment(sketch, "E336", {"start": v(11.26, -101.94) * mm, "end": v(11.19, -102.38) * mm});
            skLineSegment(sketch, "E337", {"start": v(11.19, -102.38) * mm, "end": v(11.02, -103.26) * mm});
            skLineSegment(sketch, "E338", {"start": v(11.02, -103.26) * mm, "end": v(10.93, -103.7) * mm});
            skLineSegment(sketch, "E339", {"start": v(10.93, -103.7) * mm, "end": v(9.81, -103.87) * mm});
            skLineSegment(sketch, "E340", {"start": v(9.81, -103.87) * mm, "end": v(9.6, -103.48) * mm});
            skLineSegment(sketch, "E341", {"start": v(9.6, -103.48) * mm, "end": v(9.17, -102.69) * mm});
            skLineSegment(sketch, "E342", {"start": v(9.17, -102.69) * mm, "end": v(8.97, -102.3) * mm});
            skLineSegment(sketch, "E343", {"start": v(8.97, -102.3) * mm, "end": v(7.83, -102.45) * mm});
            skLineSegment(sketch, "E344", {"start": v(7.83, -102.45) * mm, "end": v(7.74, -102.89) * mm});
            skLineSegment(sketch, "E345", {"start": v(7.74, -102.89) * mm, "end": v(7.54, -103.76) * mm});
            skLineSegment(sketch, "E346", {"start": v(7.54, -103.76) * mm, "end": v(7.44, -104.2) * mm});
            skLineSegment(sketch, "E347", {"start": v(7.44, -104.2) * mm, "end": v(6.31, -104.33) * mm});
            skLineSegment(sketch, "E348", {"start": v(6.31, -104.33) * mm, "end": v(6.1, -103.93) * mm});
            skLineSegment(sketch, "E349", {"start": v(6.1, -103.93) * mm, "end": v(5.71, -103.13) * mm});
            skLineSegment(sketch, "E350", {"start": v(5.71, -103.13) * mm, "end": v(5.52, -102.73) * mm});
            skLineSegment(sketch, "E351", {"start": v(5.52, -102.73) * mm, "end": v(4.38, -102.84) * mm});
            skLineSegment(sketch, "E352", {"start": v(4.38, -102.84) * mm, "end": v(4.27, -103.28) * mm});
            skLineSegment(sketch, "E353", {"start": v(4.27, -103.28) * mm, "end": v(4.05, -104.14) * mm});
            skLineSegment(sketch, "E354", {"start": v(4.05, -104.14) * mm, "end": v(3.93, -104.57) * mm});
            skLineSegment(sketch, "E355", {"start": v(3.93, -104.57) * mm, "end": v(2.8, -104.67) * mm});
            skLineSegment(sketch, "E356", {"start": v(2.8, -104.67) * mm, "end": v(2.6, -104.26) * mm});
            skLineSegment(sketch, "E357", {"start": v(2.6, -104.26) * mm, "end": v(2.24, -103.45) * mm});
            skLineSegment(sketch, "E358", {"start": v(2.24, -103.45) * mm, "end": v(2.06, -103.04) * mm});
            skLineSegment(sketch, "E359", {"start": v(2.06, -103.04) * mm, "end": v(0.92, -103.12) * mm});
            skLineSegment(sketch, "E360", {"start": v(0.92, -103.12) * mm, "end": v(0.8, -103.55) * mm});
            skLineSegment(sketch, "E361", {"start": v(0.8, -103.55) * mm, "end": v(0.55, -104.4) * mm});
            skLineSegment(sketch, "E362", {"start": v(0.55, -104.4) * mm, "end": v(0.4, -104.84) * mm});
            skLineSegment(sketch, "E363", {"start": v(0.4, -104.84) * mm, "end": v(-0.72, -104.9) * mm});
            skLineSegment(sketch, "E364", {"start": v(-0.72, -104.9) * mm, "end": v(-0.9, -104.48) * mm});
            skLineSegment(sketch, "E365", {"start": v(-0.9, -104.48) * mm, "end": v(-1.24, -103.66) * mm});
            skLineSegment(sketch, "E366", {"start": v(-1.24, -103.66) * mm, "end": v(-1.4, -103.24) * mm});
            skLineSegment(sketch, "E367", {"start": v(-1.4, -103.24) * mm, "end": v(-2.55, -103.28) * mm});
            skLineSegment(sketch, "E368", {"start": v(-2.55, -103.28) * mm, "end": v(-2.68, -103.7) * mm});
            skLineSegment(sketch, "E369", {"start": v(-2.68, -103.7) * mm, "end": v(-2.97, -104.56) * mm});
            skLineSegment(sketch, "E370", {"start": v(-2.97, -104.56) * mm, "end": v(-3.12, -104.98) * mm});
            skLineSegment(sketch, "E371", {"start": v(-3.12, -104.98) * mm, "end": v(-4.25, -105) * mm});
            skLineSegment(sketch, "E372", {"start": v(-4.25, -105) * mm, "end": v(-4.41, -104.58) * mm});
            skLineSegment(sketch, "E373", {"start": v(-4.41, -104.58) * mm, "end": v(-4.72, -103.75) * mm});
            skLineSegment(sketch, "E374", {"start": v(-4.72, -103.75) * mm, "end": v(-4.87, -103.33) * mm});
            skLineSegment(sketch, "E375", {"start": v(-4.87, -103.33) * mm, "end": v(-6.02, -103.33) * mm});
            skLineSegment(sketch, "E376", {"start": v(-6.02, -103.33) * mm, "end": v(-6.17, -103.75) * mm});
            skLineSegment(sketch, "E377", {"start": v(-6.17, -103.75) * mm, "end": v(-6.48, -104.59) * mm});
            skLineSegment(sketch, "E378", {"start": v(-6.48, -104.59) * mm, "end": v(-6.64, -105) * mm});
            skLineSegment(sketch, "E379", {"start": v(-6.64, -105) * mm, "end": v(-7.77, -104.99) * mm});
            skLineSegment(sketch, "E380", {"start": v(-7.77, -104.99) * mm, "end": v(-7.92, -104.56) * mm});
            skLineSegment(sketch, "E381", {"start": v(-7.92, -104.56) * mm, "end": v(-8.21, -103.72) * mm});
            skLineSegment(sketch, "E382", {"start": v(-8.21, -103.72) * mm, "end": v(-8.34, -103.3) * mm});
            skLineSegment(sketch, "E383", {"start": v(-8.34, -103.3) * mm, "end": v(-9.5, -103.26) * mm});
            skLineSegment(sketch, "E384", {"start": v(-9.5, -103.26) * mm, "end": v(-9.65, -103.67) * mm});
            skLineSegment(sketch, "E385", {"start": v(-9.65, -103.67) * mm, "end": v(-10, -104.5) * mm});
            skLineSegment(sketch, "E386", {"start": v(-10, -104.5) * mm, "end": v(-10.17, -104.91) * mm});
            skLineSegment(sketch, "E387", {"start": v(-10.17, -104.91) * mm, "end": v(-11.3, -104.86) * mm});
            skLineSegment(sketch, "E388", {"start": v(-11.3, -104.86) * mm, "end": v(-11.44, -104.43) * mm});
            skLineSegment(sketch, "E389", {"start": v(-11.44, -104.43) * mm, "end": v(-11.7, -103.57) * mm});
            skLineSegment(sketch, "E390", {"start": v(-11.7, -103.57) * mm, "end": v(-11.81, -103.14) * mm});
            skLineSegment(sketch, "E391", {"start": v(-11.81, -103.14) * mm, "end": v(-12.96, -103.07) * mm});
            skLineSegment(sketch, "E392", {"start": v(-12.96, -103.07) * mm, "end": v(-13.13, -103.48) * mm});
            skLineSegment(sketch, "E393", {"start": v(-13.13, -103.48) * mm, "end": v(-13.5, -104.3) * mm});
            skLineSegment(sketch, "E394", {"start": v(-13.5, -104.3) * mm, "end": v(-13.7, -104.7) * mm});
            skLineSegment(sketch, "E395", {"start": v(-13.7, -104.7) * mm, "end": v(-14.82, -104.6) * mm});
            skLineSegment(sketch, "E396", {"start": v(-14.82, -104.6) * mm, "end": v(-14.94, -104.17) * mm});
            skLineSegment(sketch, "E397", {"start": v(-14.94, -104.17) * mm, "end": v(-15.17, -103.3) * mm});
            skLineSegment(sketch, "E398", {"start": v(-15.17, -103.3) * mm, "end": v(-15.27, -102.88) * mm});
            skLineSegment(sketch, "E399", {"start": v(-15.27, -102.88) * mm, "end": v(-16.42, -102.76) * mm});
            skLineSegment(sketch, "E400", {"start": v(-16.42, -102.76) * mm, "end": v(-16.6, -103.17) * mm});
            skLineSegment(sketch, "E401", {"start": v(-16.6, -103.17) * mm, "end": v(-17, -103.97) * mm});
            skLineSegment(sketch, "E402", {"start": v(-17, -103.97) * mm, "end": v(-17.2, -104.37) * mm});
            skLineSegment(sketch, "E403", {"start": v(-17.2, -104.37) * mm, "end": v(-18.33, -104.24) * mm});
            skLineSegment(sketch, "E404", {"start": v(-18.33, -104.24) * mm, "end": v(-18.43, -103.8) * mm});
            skLineSegment(sketch, "E405", {"start": v(-18.43, -103.8) * mm, "end": v(-18.63, -102.93) * mm});
            skLineSegment(sketch, "E406", {"start": v(-18.63, -102.93) * mm, "end": v(-18.72, -102.5) * mm});
            skLineSegment(sketch, "E407", {"start": v(-18.72, -102.5) * mm, "end": v(-19.86, -102.34) * mm});
            skLineSegment(sketch, "E408", {"start": v(-19.86, -102.34) * mm, "end": v(-20.06, -102.74) * mm});
            skLineSegment(sketch, "E409", {"start": v(-20.06, -102.74) * mm, "end": v(-20.49, -103.53) * mm});
            skLineSegment(sketch, "E410", {"start": v(-20.49, -103.53) * mm, "end": v(-20.7, -103.92) * mm});
            skLineSegment(sketch, "E411", {"start": v(-20.7, -103.92) * mm, "end": v(-21.82, -103.75) * mm});
            skLineSegment(sketch, "E412", {"start": v(-21.82, -103.75) * mm, "end": v(-21.91, -103.31) * mm});
            skLineSegment(sketch, "E413", {"start": v(-21.91, -103.31) * mm, "end": v(-22.08, -102.43) * mm});
            skLineSegment(sketch, "E414", {"start": v(-22.08, -102.43) * mm, "end": v(-22.16, -102) * mm});
            skLineSegment(sketch, "E415", {"start": v(-22.16, -102) * mm, "end": v(-23.3, -101.8) * mm});
            skLineSegment(sketch, "E416", {"start": v(-23.3, -101.8) * mm, "end": v(-23.5, -102.2) * mm});
            skLineSegment(sketch, "E417", {"start": v(-23.5, -102.2) * mm, "end": v(-23.95, -102.97) * mm});
            skLineSegment(sketch, "E418", {"start": v(-23.95, -102.97) * mm, "end": v(-24.19, -103.35) * mm});
            skLineSegment(sketch, "E419", {"start": v(-24.19, -103.35) * mm, "end": v(-25.3, -103.15) * mm});
            skLineSegment(sketch, "E420", {"start": v(-25.3, -103.15) * mm, "end": v(-25.38, -102.7) * mm});
            skLineSegment(sketch, "E421", {"start": v(-25.38, -102.7) * mm, "end": v(-25.52, -101.82) * mm});
            skLineSegment(sketch, "E422", {"start": v(-25.52, -101.82) * mm, "end": v(-25.58, -101.38) * mm});
            skLineSegment(sketch, "E423", {"start": v(-25.58, -101.38) * mm, "end": v(-26.7, -101.16) * mm});
            skLineSegment(sketch, "E424", {"start": v(-26.7, -101.16) * mm, "end": v(-26.93, -101.54) * mm});
            skLineSegment(sketch, "E425", {"start": v(-26.93, -101.54) * mm, "end": v(-27.4, -102.3) * mm});
            skLineSegment(sketch, "E426", {"start": v(-27.4, -102.3) * mm, "end": v(-27.65, -102.67) * mm});
            skLineSegment(sketch, "E427", {"start": v(-27.65, -102.67) * mm, "end": v(-28.75, -102.43) * mm});
            skLineSegment(sketch, "E428", {"start": v(-28.75, -102.43) * mm, "end": v(-28.82, -101.98) * mm});
            skLineSegment(sketch, "E429", {"start": v(-28.82, -101.98) * mm, "end": v(-28.93, -101.1) * mm});
            skLineSegment(sketch, "E430", {"start": v(-28.93, -101.1) * mm, "end": v(-28.97, -100.66) * mm});
            skLineSegment(sketch, "E431", {"start": v(-28.97, -100.66) * mm, "end": v(-30.09, -100.4) * mm});
            skLineSegment(sketch, "E432", {"start": v(-30.09, -100.4) * mm, "end": v(-30.33, -100.76) * mm});
            skLineSegment(sketch, "E433", {"start": v(-30.33, -100.76) * mm, "end": v(-30.83, -101.5) * mm});
            skLineSegment(sketch, "E434", {"start": v(-30.83, -101.5) * mm, "end": v(-31.08, -101.87) * mm});
            skLineSegment(sketch, "E435", {"start": v(-31.08, -101.87) * mm, "end": v(-32.18, -101.6) * mm});
            skLineSegment(sketch, "E436", {"start": v(-32.18, -101.6) * mm, "end": v(-32.23, -101.15) * mm});
            skLineSegment(sketch, "E437", {"start": v(-32.23, -101.15) * mm, "end": v(-32.3, -100.26) * mm});
            skLineSegment(sketch, "E438", {"start": v(-32.3, -100.26) * mm, "end": v(-32.34, -99.81) * mm});
            skLineSegment(sketch, "E439", {"start": v(-32.34, -99.81) * mm, "end": v(-33.45, -99.51) * mm});
            skLineSegment(sketch, "E440", {"start": v(-33.45, -99.51) * mm, "end": v(-33.7, -99.88) * mm});
            skLineSegment(sketch, "E441", {"start": v(-33.7, -99.88) * mm, "end": v(-34.22, -100.6) * mm});
            skLineSegment(sketch, "E442", {"start": v(-34.22, -100.6) * mm, "end": v(-34.5, -100.96) * mm});
            skLineSegment(sketch, "E443", {"start": v(-34.5, -100.96) * mm, "end": v(-35.58, -100.65) * mm});
            skLineSegment(sketch, "E444", {"start": v(-35.58, -100.65) * mm, "end": v(-35.61, -100.2) * mm});
            skLineSegment(sketch, "E445", {"start": v(-35.61, -100.2) * mm, "end": v(-35.66, -99.3) * mm});
            skLineSegment(sketch, "E446", {"start": v(-35.66, -99.3) * mm, "end": v(-35.68, -98.86) * mm});
            skLineSegment(sketch, "E447", {"start": v(-35.68, -98.86) * mm, "end": v(-36.78, -98.52) * mm});
            skLineSegment(sketch, "E448", {"start": v(-36.78, -98.52) * mm, "end": v(-37.04, -98.88) * mm});
            skLineSegment(sketch, "E449", {"start": v(-37.04, -98.88) * mm, "end": v(-37.59, -99.58) * mm});
            skLineSegment(sketch, "E450", {"start": v(-37.59, -99.58) * mm, "end": v(-37.87, -99.93) * mm});
            skLineSegment(sketch, "E451", {"start": v(-37.87, -99.93) * mm, "end": v(-38.94, -99.58) * mm});
            skLineSegment(sketch, "E452", {"start": v(-38.94, -99.58) * mm, "end": v(-38.96, -99.13) * mm});
            skLineSegment(sketch, "E453", {"start": v(-38.96, -99.13) * mm, "end": v(-38.98, -98.24) * mm});
            skLineSegment(sketch, "E454", {"start": v(-38.98, -98.24) * mm, "end": v(-38.98, -97.8) * mm});
            skLineSegment(sketch, "E455", {"start": v(-38.98, -97.8) * mm, "end": v(-40.07, -97.42) * mm});
            skLineSegment(sketch, "E456", {"start": v(-40.07, -97.42) * mm, "end": v(-40.34, -97.77) * mm});
            skLineSegment(sketch, "E457", {"start": v(-40.34, -97.77) * mm, "end": v(-40.91, -98.45) * mm});
            skLineSegment(sketch, "E458", {"start": v(-40.91, -98.45) * mm, "end": v(-41.2, -98.8) * mm});
            skLineSegment(sketch, "E459", {"start": v(-41.2, -98.8) * mm, "end": v(-42.27, -98.4) * mm});
            skLineSegment(sketch, "E460", {"start": v(-42.27, -98.4) * mm, "end": v(-42.27, -97.96) * mm});
            skLineSegment(sketch, "E461", {"start": v(-42.27, -97.96) * mm, "end": v(-42.26, -97.06) * mm});
            skLineSegment(sketch, "E462", {"start": v(-42.26, -97.06) * mm, "end": v(-42.25, -96.62) * mm});
            skLineSegment(sketch, "E463", {"start": v(-42.25, -96.62) * mm, "end": v(-43.32, -96.2) * mm});
            skLineSegment(sketch, "E464", {"start": v(-43.32, -96.2) * mm, "end": v(-43.6, -96.54) * mm});
            skLineSegment(sketch, "E465", {"start": v(-43.6, -96.54) * mm, "end": v(-44.2, -97.21) * mm});
            skLineSegment(sketch, "E466", {"start": v(-44.2, -97.21) * mm, "end": v(-44.5, -97.54) * mm});
            skLineSegment(sketch, "E467", {"start": v(-44.5, -97.54) * mm, "end": v(-45.55, -97.12) * mm});
            skLineSegment(sketch, "E468", {"start": v(-45.55, -97.12) * mm, "end": v(-45.54, -96.67) * mm});
            skLineSegment(sketch, "E469", {"start": v(-45.54, -96.67) * mm, "end": v(-45.5, -95.78) * mm});
            skLineSegment(sketch, "E470", {"start": v(-45.5, -95.78) * mm, "end": v(-45.47, -95.33) * mm});
            skLineSegment(sketch, "E471", {"start": v(-45.47, -95.33) * mm, "end": v(-46.53, -94.89) * mm});
            skLineSegment(sketch, "E472", {"start": v(-46.53, -94.89) * mm, "end": v(-46.83, -95.21) * mm});
            skLineSegment(sketch, "E473", {"start": v(-46.83, -95.21) * mm, "end": v(-47.45, -95.86) * mm});
            skLineSegment(sketch, "E474", {"start": v(-47.45, -95.86) * mm, "end": v(-47.76, -96.18) * mm});
            skLineSegment(sketch, "E475", {"start": v(-47.76, -96.18) * mm, "end": v(-48.8, -95.72) * mm});
            skLineSegment(sketch, "E476", {"start": v(-48.8, -95.72) * mm, "end": v(-48.77, -95.27) * mm});
            skLineSegment(sketch, "E477", {"start": v(-48.77, -95.27) * mm, "end": v(-48.7, -94.38) * mm});
            skLineSegment(sketch, "E478", {"start": v(-48.7, -94.38) * mm, "end": v(-48.65, -93.94) * mm});
            skLineSegment(sketch, "E479", {"start": v(-48.65, -93.94) * mm, "end": v(-49.7, -93.46) * mm});
            skLineSegment(sketch, "E480", {"start": v(-49.7, -93.46) * mm, "end": v(-50, -93.78) * mm});
            skLineSegment(sketch, "E481", {"start": v(-50, -93.78) * mm, "end": v(-50.64, -94.4) * mm});
            skLineSegment(sketch, "E482", {"start": v(-50.64, -94.4) * mm, "end": v(-50.97, -94.71) * mm});
            skLineSegment(sketch, "E483", {"start": v(-50.97, -94.71) * mm, "end": v(-51.98, -94.22) * mm});
            skLineSegment(sketch, "E484", {"start": v(-51.98, -94.22) * mm, "end": v(-51.94, -93.77) * mm});
            skLineSegment(sketch, "E485", {"start": v(-51.94, -93.77) * mm, "end": v(-51.84, -92.88) * mm});
            skLineSegment(sketch, "E486", {"start": v(-51.84, -92.88) * mm, "end": v(-51.79, -92.44) * mm});
            skLineSegment(sketch, "E487", {"start": v(-51.79, -92.44) * mm, "end": v(-52.8, -91.92) * mm});
            skLineSegment(sketch, "E488", {"start": v(-52.8, -91.92) * mm, "end": v(-53.13, -92.23) * mm});
            skLineSegment(sketch, "E489", {"start": v(-53.13, -92.23) * mm, "end": v(-53.79, -92.84) * mm});
            skLineSegment(sketch, "E490", {"start": v(-53.79, -92.84) * mm, "end": v(-54.12, -93.14) * mm});
            skLineSegment(sketch, "E491", {"start": v(-54.12, -93.14) * mm, "end": v(-55.12, -92.6) * mm});
            skLineSegment(sketch, "E492", {"start": v(-55.12, -92.6) * mm, "end": v(-55.07, -92.16) * mm});
            skLineSegment(sketch, "E493", {"start": v(-55.07, -92.16) * mm, "end": v(-54.94, -91.28) * mm});
            skLineSegment(sketch, "E494", {"start": v(-54.94, -91.28) * mm, "end": v(-54.86, -90.84) * mm});
            skLineSegment(sketch, "E495", {"start": v(-54.86, -90.84) * mm, "end": v(-55.87, -90.29) * mm});
            skLineSegment(sketch, "E496", {"start": v(-55.87, -90.29) * mm, "end": v(-56.2, -90.58) * mm});
            skLineSegment(sketch, "E497", {"start": v(-56.2, -90.58) * mm, "end": v(-56.88, -91.17) * mm});
            skLineSegment(sketch, "E498", {"start": v(-56.88, -91.17) * mm, "end": v(-57.22, -91.45) * mm});
            skLineSegment(sketch, "E499", {"start": v(-57.22, -91.45) * mm, "end": v(-58.2, -90.9) * mm});
            skLineSegment(sketch, "E500", {"start": v(-58.2, -90.9) * mm, "end": v(-58.13, -90.45) * mm});
            skLineSegment(sketch, "E501", {"start": v(-58.13, -90.45) * mm, "end": v(-57.98, -89.57) * mm});
            skLineSegment(sketch, "E502", {"start": v(-57.98, -89.57) * mm, "end": v(-57.89, -89.13) * mm});
            skLineSegment(sketch, "E503", {"start": v(-57.89, -89.13) * mm, "end": v(-58.88, -88.55) * mm});
            skLineSegment(sketch, "E504", {"start": v(-58.88, -88.55) * mm, "end": v(-59.22, -88.83) * mm});
            skLineSegment(sketch, "E505", {"start": v(-59.22, -88.83) * mm, "end": v(-59.91, -89.4) * mm});
            skLineSegment(sketch, "E506", {"start": v(-59.91, -89.4) * mm, "end": v(-60.27, -89.67) * mm});
            skLineSegment(sketch, "E507", {"start": v(-60.27, -89.67) * mm, "end": v(-61.23, -89.08) * mm});
            skLineSegment(sketch, "E508", {"start": v(-61.23, -89.08) * mm, "end": v(-61.14, -88.63) * mm});
            skLineSegment(sketch, "E509", {"start": v(-61.14, -88.63) * mm, "end": v(-60.95, -87.76) * mm});
            skLineSegment(sketch, "E510", {"start": v(-60.95, -87.76) * mm, "end": v(-60.85, -87.33) * mm});
            skLineSegment(sketch, "E511", {"start": v(-60.85, -87.33) * mm, "end": v(-61.82, -86.7) * mm});
            skLineSegment(sketch, "E512", {"start": v(-61.82, -86.7) * mm, "end": v(-62.17, -86.98) * mm});
            skLineSegment(sketch, "E513", {"start": v(-62.17, -86.98) * mm, "end": v(-62.88, -87.52) * mm});
            skLineSegment(sketch, "E514", {"start": v(-62.88, -87.52) * mm, "end": v(-63.25, -87.78) * mm});
            skLineSegment(sketch, "E515", {"start": v(-63.25, -87.78) * mm, "end": v(-64.2, -87.16) * mm});
            skLineSegment(sketch, "E516", {"start": v(-64.2, -87.16) * mm, "end": v(-64.09, -86.72) * mm});
            skLineSegment(sketch, "E517", {"start": v(-64.09, -86.72) * mm, "end": v(-63.87, -85.85) * mm});
            skLineSegment(sketch, "E518", {"start": v(-63.87, -85.85) * mm, "end": v(-63.76, -85.42) * mm});
            skLineSegment(sketch, "E519", {"start": v(-63.76, -85.42) * mm, "end": v(-64.7, -84.77) * mm});
            skLineSegment(sketch, "E520", {"start": v(-64.7, -84.77) * mm, "end": v(-65.06, -85.03) * mm});
            skLineSegment(sketch, "E521", {"start": v(-65.06, -85.03) * mm, "end": v(-65.8, -85.55) * mm});
            skLineSegment(sketch, "E522", {"start": v(-65.8, -85.55) * mm, "end": v(-66.17, -85.8) * mm});
            skLineSegment(sketch, "E523", {"start": v(-66.17, -85.8) * mm, "end": v(-67.09, -85.14) * mm});
            skLineSegment(sketch, "E524", {"start": v(-67.09, -85.14) * mm, "end": v(-66.97, -84.7) * mm});
            skLineSegment(sketch, "E525", {"start": v(-66.97, -84.7) * mm, "end": v(-66.72, -83.85) * mm});
            skLineSegment(sketch, "E526", {"start": v(-66.72, -83.85) * mm, "end": v(-66.6, -83.42) * mm});
            skLineSegment(sketch, "E527", {"start": v(-66.6, -83.42) * mm, "end": v(-67.52, -82.74) * mm});
            skLineSegment(sketch, "E528", {"start": v(-67.52, -82.74) * mm, "end": v(-67.88, -82.99) * mm});
            skLineSegment(sketch, "E529", {"start": v(-67.88, -82.99) * mm, "end": v(-68.63, -83.48) * mm});
            skLineSegment(sketch, "E530", {"start": v(-68.63, -83.48) * mm, "end": v(-69.01, -83.71) * mm});
            skLineSegment(sketch, "E531", {"start": v(-69.01, -83.71) * mm, "end": v(-69.91, -83.03) * mm});
            skLineSegment(sketch, "E532", {"start": v(-69.91, -83.03) * mm, "end": v(-69.78, -82.6) * mm});
            skLineSegment(sketch, "E533", {"start": v(-69.78, -82.6) * mm, "end": v(-69.5, -81.75) * mm});
            skLineSegment(sketch, "E534", {"start": v(-69.5, -81.75) * mm, "end": v(-69.36, -81.33) * mm});
            skLineSegment(sketch, "E535", {"start": v(-69.36, -81.33) * mm, "end": v(-70.26, -80.61) * mm});
            skLineSegment(sketch, "E536", {"start": v(-70.26, -80.61) * mm, "end": v(-70.64, -80.85) * mm});
            skLineSegment(sketch, "E537", {"start": v(-70.64, -80.85) * mm, "end": v(-71.4, -81.31) * mm});
            skLineSegment(sketch, "E538", {"start": v(-71.4, -81.31) * mm, "end": v(-71.8, -81.54) * mm});
            skLineSegment(sketch, "E539", {"start": v(-71.8, -81.54) * mm, "end": v(-72.66, -80.82) * mm});
            skLineSegment(sketch, "E540", {"start": v(-72.66, -80.82) * mm, "end": v(-72.52, -80.4) * mm});
            skLineSegment(sketch, "E541", {"start": v(-72.52, -80.4) * mm, "end": v(-72.22, -79.55) * mm});
            skLineSegment(sketch, "E542", {"start": v(-72.22, -79.55) * mm, "end": v(-72.06, -79.14) * mm});
            skLineSegment(sketch, "E543", {"start": v(-72.06, -79.14) * mm, "end": v(-72.93, -78.4) * mm});
            skLineSegment(sketch, "E544", {"start": v(-72.93, -78.4) * mm, "end": v(-73.32, -78.62) * mm});
            skLineSegment(sketch, "E545", {"start": v(-73.32, -78.62) * mm, "end": v(-74.1, -79.06) * mm});
            skLineSegment(sketch, "E546", {"start": v(-74.1, -79.06) * mm, "end": v(-74.5, -79.27) * mm});
            skLineSegment(sketch, "E547", {"start": v(-74.5, -79.27) * mm, "end": v(-75.34, -78.52) * mm});
            skLineSegment(sketch, "E548", {"start": v(-75.34, -78.52) * mm, "end": v(-75.18, -78.1) * mm});
            skLineSegment(sketch, "E549", {"start": v(-75.18, -78.1) * mm, "end": v(-74.85, -77.27) * mm});
            skLineSegment(sketch, "E550", {"start": v(-74.85, -77.27) * mm, "end": v(-74.68, -76.86) * mm});
            skLineSegment(sketch, "E551", {"start": v(-74.68, -76.86) * mm, "end": v(-75.53, -76.1) * mm});
            skLineSegment(sketch, "E552", {"start": v(-75.53, -76.1) * mm, "end": v(-75.92, -76.3) * mm});
            skLineSegment(sketch, "E553", {"start": v(-75.92, -76.3) * mm, "end": v(-76.71, -76.71) * mm});
            skLineSegment(sketch, "E554", {"start": v(-76.71, -76.71) * mm, "end": v(-77.12, -76.91) * mm});
            skLineSegment(sketch, "E555", {"start": v(-77.12, -76.91) * mm, "end": v(-77.94, -76.14) * mm});
            skLineSegment(sketch, "E556", {"start": v(-77.94, -76.14) * mm, "end": v(-77.77, -75.72) * mm});
            skLineSegment(sketch, "E557", {"start": v(-77.77, -75.72) * mm, "end": v(-77.4, -74.9) * mm});
            skLineSegment(sketch, "E558", {"start": v(-77.4, -74.9) * mm, "end": v(-77.22, -74.5) * mm});
            skLineSegment(sketch, "E559", {"start": v(-77.22, -74.5) * mm, "end": v(-78.04, -73.7) * mm});
            skLineSegment(sketch, "E560", {"start": v(-78.04, -73.7) * mm, "end": v(-78.44, -73.9) * mm});
            skLineSegment(sketch, "E561", {"start": v(-78.44, -73.9) * mm, "end": v(-79.25, -74.28) * mm});
            skLineSegment(sketch, "E562", {"start": v(-79.25, -74.28) * mm, "end": v(-79.66, -74.46) * mm});
            skLineSegment(sketch, "E563", {"start": v(-79.66, -74.46) * mm, "end": v(-80.46, -73.66) * mm});
            skLineSegment(sketch, "E564", {"start": v(-80.46, -73.66) * mm, "end": v(-80.27, -73.26) * mm});
            skLineSegment(sketch, "E565", {"start": v(-80.27, -73.26) * mm, "end": v(-79.88, -72.45) * mm});
            skLineSegment(sketch, "E566", {"start": v(-79.88, -72.45) * mm, "end": v(-79.68, -72.05) * mm});
            skLineSegment(sketch, "E567", {"start": v(-79.68, -72.05) * mm, "end": v(-80.48, -71.23) * mm});
            skLineSegment(sketch, "E568", {"start": v(-80.48, -71.23) * mm, "end": v(-80.88, -71.4) * mm});
            skLineSegment(sketch, "E569", {"start": v(-80.88, -71.4) * mm, "end": v(-81.7, -71.76) * mm});
            skLineSegment(sketch, "E570", {"start": v(-81.7, -71.76) * mm, "end": v(-82.12, -71.94) * mm});
            skLineSegment(sketch, "E571", {"start": v(-82.12, -71.94) * mm, "end": v(-82.89, -71.1) * mm});
            skLineSegment(sketch, "E572", {"start": v(-82.89, -71.1) * mm, "end": v(-82.69, -70.7) * mm});
            skLineSegment(sketch, "E573", {"start": v(-82.69, -70.7) * mm, "end": v(-82.27, -69.91) * mm});
            skLineSegment(sketch, "E574", {"start": v(-82.27, -69.91) * mm, "end": v(-82.06, -69.52) * mm});
            skLineSegment(sketch, "E575", {"start": v(-82.06, -69.52) * mm, "end": v(-82.83, -68.67) * mm});
            skLineSegment(sketch, "E576", {"start": v(-82.83, -68.67) * mm, "end": v(-83.24, -68.84) * mm});
            skLineSegment(sketch, "E577", {"start": v(-83.24, -68.84) * mm, "end": v(-84.07, -69.17) * mm});
            skLineSegment(sketch, "E578", {"start": v(-84.07, -69.17) * mm, "end": v(-84.5, -69.33) * mm});
            skLineSegment(sketch, "E579", {"start": v(-84.5, -69.33) * mm, "end": v(-85.23, -68.47) * mm});
            skLineSegment(sketch, "E580", {"start": v(-85.23, -68.47) * mm, "end": v(-85.02, -68.08) * mm});
            skLineSegment(sketch, "E581", {"start": v(-85.02, -68.08) * mm, "end": v(-84.58, -67.3) * mm});
            skLineSegment(sketch, "E582", {"start": v(-84.58, -67.3) * mm, "end": v(-84.35, -66.92) * mm});
            skLineSegment(sketch, "E583", {"start": v(-84.35, -66.92) * mm, "end": v(-85.1, -66.04) * mm});
            skLineSegment(sketch, "E584", {"start": v(-85.1, -66.04) * mm, "end": v(-85.5, -66.2) * mm});
            skLineSegment(sketch, "E585", {"start": v(-85.5, -66.2) * mm, "end": v(-86.35, -66.5) * mm});
            skLineSegment(sketch, "E586", {"start": v(-86.35, -66.5) * mm, "end": v(-86.78, -66.64) * mm});
            skLineSegment(sketch, "E587", {"start": v(-86.78, -66.64) * mm, "end": v(-87.49, -65.76) * mm});
            skLineSegment(sketch, "E588", {"start": v(-87.49, -65.76) * mm, "end": v(-87.26, -65.37) * mm});
            skLineSegment(sketch, "E589", {"start": v(-87.26, -65.37) * mm, "end": v(-86.8, -64.6) * mm});
            skLineSegment(sketch, "E590", {"start": v(-86.8, -64.6) * mm, "end": v(-86.56, -64.23) * mm});
            skLineSegment(sketch, "E591", {"start": v(-86.56, -64.23) * mm, "end": v(-87.27, -63.33) * mm});
            skLineSegment(sketch, "E592", {"start": v(-87.27, -63.33) * mm, "end": v(-87.69, -63.47) * mm});
            skLineSegment(sketch, "E593", {"start": v(-87.69, -63.47) * mm, "end": v(-88.54, -63.74) * mm});
            skLineSegment(sketch, "E594", {"start": v(-88.54, -63.74) * mm, "end": v(-88.97, -63.87) * mm});
            skLineSegment(sketch, "E595", {"start": v(-88.97, -63.87) * mm, "end": v(-89.65, -62.97) * mm});
            skLineSegment(sketch, "E596", {"start": v(-89.65, -62.97) * mm, "end": v(-89.41, -62.6) * mm});
            skLineSegment(sketch, "E597", {"start": v(-89.41, -62.6) * mm, "end": v(-88.92, -61.85) * mm});
            skLineSegment(sketch, "E598", {"start": v(-88.92, -61.85) * mm, "end": v(-88.67, -61.48) * mm});
            skLineSegment(sketch, "E599", {"start": v(-88.67, -61.48) * mm, "end": v(-89.35, -60.55) * mm});
            skLineSegment(sketch, "E600", {"start": v(-89.35, -60.55) * mm, "end": v(-89.77, -60.68) * mm});
            skLineSegment(sketch, "E601", {"start": v(-89.77, -60.68) * mm, "end": v(-90.63, -60.92) * mm});
            skLineSegment(sketch, "E602", {"start": v(-90.63, -60.92) * mm, "end": v(-91.07, -61.04) * mm});
            skLineSegment(sketch, "E603", {"start": v(-91.07, -61.04) * mm, "end": v(-91.72, -60.11) * mm});
            skLineSegment(sketch, "E604", {"start": v(-91.72, -60.11) * mm, "end": v(-91.47, -59.74) * mm});
            skLineSegment(sketch, "E605", {"start": v(-91.47, -59.74) * mm, "end": v(-90.95, -59.01) * mm});
            skLineSegment(sketch, "E606", {"start": v(-90.95, -59.01) * mm, "end": v(-90.69, -58.65) * mm});
            skLineSegment(sketch, "E607", {"start": v(-90.69, -58.65) * mm, "end": v(-91.33, -57.7) * mm});
            skLineSegment(sketch, "E608", {"start": v(-91.33, -57.7) * mm, "end": v(-91.76, -57.82) * mm});
            skLineSegment(sketch, "E609", {"start": v(-91.76, -57.82) * mm, "end": v(-92.63, -58.03) * mm});
            skLineSegment(sketch, "E610", {"start": v(-92.63, -58.03) * mm, "end": v(-93.07, -58.13) * mm});
            skLineSegment(sketch, "E611", {"start": v(-93.07, -58.13) * mm, "end": v(-93.7, -57.19) * mm});
            skLineSegment(sketch, "E612", {"start": v(-93.7, -57.19) * mm, "end": v(-93.43, -56.82) * mm});
            skLineSegment(sketch, "E613", {"start": v(-93.43, -56.82) * mm, "end": v(-92.89, -56.11) * mm});
            skLineSegment(sketch, "E614", {"start": v(-92.89, -56.11) * mm, "end": v(-92.61, -55.76) * mm});
            skLineSegment(sketch, "E615", {"start": v(-92.61, -55.76) * mm, "end": v(-93.22, -54.8) * mm});
            skLineSegment(sketch, "E616", {"start": v(-93.22, -54.8) * mm, "end": v(-93.66, -54.9) * mm});
            skLineSegment(sketch, "E617", {"start": v(-93.66, -54.9) * mm, "end": v(-94.53, -55.08) * mm});
            skLineSegment(sketch, "E618", {"start": v(-94.53, -55.08) * mm, "end": v(-94.97, -55.16) * mm});
            skLineSegment(sketch, "E619", {"start": v(-94.97, -55.16) * mm, "end": v(-95.56, -54.2) * mm});
            skLineSegment(sketch, "E620", {"start": v(-95.56, -54.2) * mm, "end": v(-95.28, -53.84) * mm});
            skLineSegment(sketch, "E621", {"start": v(-95.28, -53.84) * mm, "end": v(-94.72, -53.15) * mm});
            skLineSegment(sketch, "E622", {"start": v(-94.72, -53.15) * mm, "end": v(-94.43, -52.81) * mm});
            skLineSegment(sketch, "E623", {"start": v(-94.43, -52.81) * mm, "end": v(-95.02, -51.82) * mm});
            skLineSegment(sketch, "E624", {"start": v(-95.02, -51.82) * mm, "end": v(-95.45, -51.9) * mm});
            skLineSegment(sketch, "E625", {"start": v(-95.45, -51.9) * mm, "end": v(-96.33, -52.06) * mm});
            skLineSegment(sketch, "E626", {"start": v(-96.33, -52.06) * mm, "end": v(-96.78, -52.13) * mm});
            skLineSegment(sketch, "E627", {"start": v(-96.78, -52.13) * mm, "end": v(-97.33, -51.14) * mm});
            skLineSegment(sketch, "E628", {"start": v(-97.33, -51.14) * mm, "end": v(-97.04, -50.8) * mm});
            skLineSegment(sketch, "E629", {"start": v(-97.04, -50.8) * mm, "end": v(-96.46, -50.13) * mm});
            skLineSegment(sketch, "E630", {"start": v(-96.46, -50.13) * mm, "end": v(-96.16, -49.8) * mm});
            skLineSegment(sketch, "E631", {"start": v(-96.16, -49.8) * mm, "end": v(-96.7, -48.79) * mm});
            skLineSegment(sketch, "E632", {"start": v(-96.7, -48.79) * mm, "end": v(-97.14, -48.86) * mm});
            skLineSegment(sketch, "E633", {"start": v(-97.14, -48.86) * mm, "end": v(-98.03, -48.98) * mm});
            skLineSegment(sketch, "E634", {"start": v(-98.03, -48.98) * mm, "end": v(-98.48, -49.04) * mm});
            skLineSegment(sketch, "E635", {"start": v(-98.48, -49.04) * mm, "end": v(-99, -48.03) * mm});
            skLineSegment(sketch, "E636", {"start": v(-99, -48.03) * mm, "end": v(-98.7, -47.7) * mm});
            skLineSegment(sketch, "E637", {"start": v(-98.7, -47.7) * mm, "end": v(-98.09, -47.05) * mm});
            skLineSegment(sketch, "E638", {"start": v(-98.09, -47.05) * mm, "end": v(-97.78, -46.73) * mm});
            skLineSegment(sketch, "E639", {"start": v(-97.78, -46.73) * mm, "end": v(-98.3, -45.7) * mm});
            skLineSegment(sketch, "E640", {"start": v(-98.3, -45.7) * mm, "end": v(-98.73, -45.76) * mm});
            skLineSegment(sketch, "E641", {"start": v(-98.73, -45.76) * mm, "end": v(-99.62, -45.85) * mm});
            skLineSegment(sketch, "E642", {"start": v(-99.62, -45.85) * mm, "end": v(-100.07, -45.89) * mm});
            skLineSegment(sketch, "E643", {"start": v(-100.07, -45.89) * mm, "end": v(-100.56, -44.87) * mm});
            skLineSegment(sketch, "E644", {"start": v(-100.56, -44.87) * mm, "end": v(-100.25, -44.55) * mm});
            skLineSegment(sketch, "E645", {"start": v(-100.25, -44.55) * mm, "end": v(-99.62, -43.91) * mm});
            skLineSegment(sketch, "E646", {"start": v(-99.62, -43.91) * mm, "end": v(-99.3, -43.6) * mm});
            skLineSegment(sketch, "E647", {"start": v(-99.3, -43.6) * mm, "end": v(-99.78, -42.56) * mm});
            skLineSegment(sketch, "E648", {"start": v(-99.78, -42.56) * mm, "end": v(-100.22, -42.6) * mm});
            skLineSegment(sketch, "E649", {"start": v(-100.22, -42.6) * mm, "end": v(-101.1, -42.67) * mm});
            skLineSegment(sketch, "E650", {"start": v(-101.1, -42.67) * mm, "end": v(-101.56, -42.7) * mm});
            skLineSegment(sketch, "E651", {"start": v(-101.56, -42.7) * mm, "end": v(-102.01, -41.66) * mm});
            skLineSegment(sketch, "E652", {"start": v(-102.01, -41.66) * mm, "end": v(-101.7, -41.34) * mm});
            skLineSegment(sketch, "E653", {"start": v(-101.7, -41.34) * mm, "end": v(-101.04, -40.73) * mm});
            skLineSegment(sketch, "E654", {"start": v(-101.04, -40.73) * mm, "end": v(-100.7, -40.43) * mm});
            skLineSegment(sketch, "E655", {"start": v(-100.7, -40.43) * mm, "end": v(-101.15, -39.37) * mm});
            skLineSegment(sketch, "E656", {"start": v(-101.15, -39.37) * mm, "end": v(-101.6, -39.4) * mm});
            skLineSegment(sketch, "E657", {"start": v(-101.6, -39.4) * mm, "end": v(-102.49, -39.43) * mm});
            skLineSegment(sketch, "E658", {"start": v(-102.49, -39.43) * mm, "end": v(-102.94, -39.44) * mm});
            skLineSegment(sketch, "E659", {"start": v(-102.94, -39.44) * mm, "end": v(-103.36, -38.4) * mm});
            skLineSegment(sketch, "E660", {"start": v(-103.36, -38.4) * mm, "end": v(-103.02, -38.1) * mm});
            skLineSegment(sketch, "E661", {"start": v(-103.02, -38.1) * mm, "end": v(-102.35, -37.5) * mm});
            skLineSegment(sketch, "E662", {"start": v(-102.35, -37.5) * mm, "end": v(-102.01, -37.22) * mm});
            skLineSegment(sketch, "E663", {"start": v(-102.01, -37.22) * mm, "end": v(-102.42, -36.14) * mm});
            skLineSegment(sketch, "E664", {"start": v(-102.42, -36.14) * mm, "end": v(-102.87, -36.15) * mm});
            skLineSegment(sketch, "E665", {"start": v(-102.87, -36.15) * mm, "end": v(-103.76, -36.16) * mm});
            skLineSegment(sketch, "E666", {"start": v(-103.76, -36.16) * mm, "end": v(-104.2, -36.15) * mm});
            skLineSegment(sketch, "E667", {"start": v(-104.2, -36.15) * mm, "end": v(-104.6, -35.09) * mm});
            skLineSegment(sketch, "E668", {"start": v(-104.6, -35.09) * mm, "end": v(-104.25, -34.8) * mm});
            skLineSegment(sketch, "E669", {"start": v(-104.25, -34.8) * mm, "end": v(-103.56, -34.23) * mm});
            skLineSegment(sketch, "E670", {"start": v(-103.56, -34.23) * mm, "end": v(-103.2, -33.96) * mm});
            skLineSegment(sketch, "E671", {"start": v(-103.2, -33.96) * mm, "end": v(-103.58, -32.87) * mm});
            skLineSegment(sketch, "E672", {"start": v(-103.58, -32.87) * mm, "end": v(-104.03, -32.87) * mm});
            skLineSegment(sketch, "E673", {"start": v(-104.03, -32.87) * mm, "end": v(-104.92, -32.84) * mm});
            skLineSegment(sketch, "E674", {"start": v(-104.92, -32.84) * mm, "end": v(-105.37, -32.82) * mm});
            skLineSegment(sketch, "E675", {"start": v(-105.37, -32.82) * mm, "end": v(-105.71, -31.75) * mm});
            skLineSegment(sketch, "E676", {"start": v(-105.71, -31.75) * mm, "end": v(-105.36, -31.47) * mm});
            skLineSegment(sketch, "E677", {"start": v(-105.36, -31.47) * mm, "end": v(-104.65, -30.92) * mm});
            skLineSegment(sketch, "E678", {"start": v(-104.65, -30.92) * mm, "end": v(-104.3, -30.66) * mm});
            skLineSegment(sketch, "E679", {"start": v(-104.3, -30.66) * mm, "end": v(-104.63, -29.56) * mm});
            skLineSegment(sketch, "E680", {"start": v(-104.63, -29.56) * mm, "end": v(-105.07, -29.54) * mm});
            skLineSegment(sketch, "E681", {"start": v(-105.07, -29.54) * mm, "end": v(-105.97, -29.49) * mm});
            skLineSegment(sketch, "E682", {"start": v(-105.97, -29.49) * mm, "end": v(-106.41, -29.45) * mm});
            skLineSegment(sketch, "E683", {"start": v(-106.41, -29.45) * mm, "end": v(-106.72, -28.36) * mm});
            skLineSegment(sketch, "E684", {"start": v(-106.72, -28.36) * mm, "end": v(-106.36, -28.1) * mm});
            skLineSegment(sketch, "E685", {"start": v(-106.36, -28.1) * mm, "end": v(-105.64, -27.58) * mm});
            skLineSegment(sketch, "E686", {"start": v(-105.64, -27.58) * mm, "end": v(-105.27, -27.33) * mm});
            skLineSegment(sketch, "E687", {"start": v(-105.27, -27.33) * mm, "end": v(-105.57, -26.22) * mm});
            skLineSegment(sketch, "E688", {"start": v(-105.57, -26.22) * mm, "end": v(-106, -26.18) * mm});
            skLineSegment(sketch, "E689", {"start": v(-106, -26.18) * mm, "end": v(-106.9, -26.1) * mm});
            skLineSegment(sketch, "E690", {"start": v(-106.9, -26.1) * mm, "end": v(-107.35, -26.05) * mm});
            skLineSegment(sketch, "E691", {"start": v(-107.35, -26.05) * mm, "end": v(-107.62, -24.95) * mm});
            skLineSegment(sketch, "E692", {"start": v(-107.62, -24.95) * mm, "end": v(-107.25, -24.7) * mm});
            skLineSegment(sketch, "E693", {"start": v(-107.25, -24.7) * mm, "end": v(-106.5, -24.2) * mm});
            skLineSegment(sketch, "E694", {"start": v(-106.5, -24.2) * mm, "end": v(-106.13, -23.96) * mm});
            skLineSegment(sketch, "E695", {"start": v(-106.13, -23.96) * mm, "end": v(-106.4, -22.85) * mm});
            skLineSegment(sketch, "E696", {"start": v(-106.4, -22.85) * mm, "end": v(-106.83, -22.8) * mm});
            skLineSegment(sketch, "E697", {"start": v(-106.83, -22.8) * mm, "end": v(-107.72, -22.68) * mm});
            skLineSegment(sketch, "E698", {"start": v(-107.72, -22.68) * mm, "end": v(-108.16, -22.62) * mm});
            skLineSegment(sketch, "E699", {"start": v(-108.16, -22.62) * mm, "end": v(-108.4, -21.51) * mm});
            skLineSegment(sketch, "E700", {"start": v(-108.4, -21.51) * mm, "end": v(-108.02, -21.27) * mm});
            skLineSegment(sketch, "E701", {"start": v(-108.02, -21.27) * mm, "end": v(-107.26, -20.8) * mm});
            skLineSegment(sketch, "E702", {"start": v(-107.26, -20.8) * mm, "end": v(-106.88, -20.57) * mm});
            skLineSegment(sketch, "E703", {"start": v(-106.88, -20.57) * mm, "end": v(-107.1, -19.45) * mm});
            skLineSegment(sketch, "E704", {"start": v(-107.1, -19.45) * mm, "end": v(-107.54, -19.38) * mm});
            skLineSegment(sketch, "E705", {"start": v(-107.54, -19.38) * mm, "end": v(-108.42, -19.24) * mm});
            skLineSegment(sketch, "E706", {"start": v(-108.42, -19.24) * mm, "end": v(-108.87, -19.16) * mm});
            skLineSegment(sketch, "E707", {"start": v(-108.87, -19.16) * mm, "end": v(-109.07, -18.05) * mm});
            skLineSegment(sketch, "E708", {"start": v(-109.07, -18.05) * mm, "end": v(-108.68, -17.82) * mm});
            skLineSegment(sketch, "E709", {"start": v(-108.68, -17.82) * mm, "end": v(-107.9, -17.37) * mm});
            skLineSegment(sketch, "E710", {"start": v(-107.9, -17.37) * mm, "end": v(-107.51, -17.16) * mm});
            skLineSegment(sketch, "E711", {"start": v(-107.51, -17.16) * mm, "end": v(-107.7, -16.03) * mm});
            skLineSegment(sketch, "E712", {"start": v(-107.7, -16.03) * mm, "end": v(-108.13, -15.95) * mm});
            skLineSegment(sketch, "E713", {"start": v(-108.13, -15.95) * mm, "end": v(-109.01, -15.78) * mm});
            skLineSegment(sketch, "E714", {"start": v(-109.01, -15.78) * mm, "end": v(-109.45, -15.68) * mm});
            skLineSegment(sketch, "E715", {"start": v(-109.45, -15.68) * mm, "end": v(-109.61, -14.56) * mm});
            skLineSegment(sketch, "E716", {"start": v(-109.61, -14.56) * mm, "end": v(-109.22, -14.34) * mm});
            skLineSegment(sketch, "E717", {"start": v(-109.22, -14.34) * mm, "end": v(-108.43, -13.93) * mm});
            skLineSegment(sketch, "E718", {"start": v(-108.43, -13.93) * mm, "end": v(-108.03, -13.73) * mm});
            skLineSegment(sketch, "E719", {"start": v(-108.03, -13.73) * mm, "end": v(-108.18, -12.59) * mm});
            skLineSegment(sketch, "E720", {"start": v(-108.18, -12.59) * mm, "end": v(-108.61, -12.5) * mm});
            skLineSegment(sketch, "E721", {"start": v(-108.61, -12.5) * mm, "end": v(-109.48, -12.3) * mm});
            skLineSegment(sketch, "E722", {"start": v(-109.48, -12.3) * mm, "end": v(-109.92, -12.18) * mm});
            skLineSegment(sketch, "E723", {"start": v(-109.92, -12.18) * mm, "end": v(-110.04, -11.06) * mm});
            skLineSegment(sketch, "E724", {"start": v(-110.04, -11.06) * mm, "end": v(-109.64, -10.86) * mm});
            skLineSegment(sketch, "E725", {"start": v(-109.64, -10.86) * mm, "end": v(-108.84, -10.47) * mm});
            skLineSegment(sketch, "E726", {"start": v(-108.84, -10.47) * mm, "end": v(-108.44, -10.28) * mm});
            skLineSegment(sketch, "E727", {"start": v(-108.44, -10.28) * mm, "end": v(-108.54, -9.14) * mm});
            skLineSegment(sketch, "E728", {"start": v(-108.54, -9.14) * mm, "end": v(-108.97, -9.03) * mm});
            skLineSegment(sketch, "E729", {"start": v(-108.97, -9.03) * mm, "end": v(-109.84, -8.8) * mm});
            skLineSegment(sketch, "E730", {"start": v(-109.84, -8.8) * mm, "end": v(-110.27, -8.67) * mm});
            skLineSegment(sketch, "E731", {"start": v(-110.27, -8.67) * mm, "end": v(-110.36, -7.55) * mm});
            skLineSegment(sketch, "E732", {"start": v(-110.36, -7.55) * mm, "end": v(-109.95, -7.36) * mm});
            skLineSegment(sketch, "E733", {"start": v(-109.95, -7.36) * mm, "end": v(-109.13, -7) * mm});
            skLineSegment(sketch, "E734", {"start": v(-109.13, -7) * mm, "end": v(-108.72, -6.82) * mm});
            skLineSegment(sketch, "E735", {"start": v(-108.72, -6.82) * mm, "end": v(-108.8, -5.67) * mm});
            skLineSegment(sketch, "E736", {"start": v(-108.8, -5.67) * mm, "end": v(-109.22, -5.55) * mm});
            skLineSegment(sketch, "E737", {"start": v(-109.22, -5.55) * mm, "end": v(-110.07, -5.3) * mm});
            skLineSegment(sketch, "E738", {"start": v(-110.07, -5.3) * mm, "end": v(-110.5, -5.15) * mm});
            skLineSegment(sketch, "E739", {"start": v(-110.5, -5.15) * mm, "end": v(-110.55, -4.02) * mm});
            skLineSegment(sketch, "E740", {"start": v(-110.55, -4.02) * mm, "end": v(-110.14, -3.85) * mm});
            skLineSegment(sketch, "E741", {"start": v(-110.14, -3.85) * mm, "end": v(-109.3, -3.51) * mm});
            skLineSegment(sketch, "E742", {"start": v(-109.3, -3.51) * mm, "end": v(-108.9, -3.35) * mm});
            skLineSegment(sketch, "E743", {"start": v(-108.9, -3.35) * mm, "end": v(-108.92, -2.2) * mm});
            skLineSegment(sketch, "E744", {"start": v(-108.92, -2.2) * mm, "end": v(-109.35, -2.07) * mm});
            skLineSegment(sketch, "E745", {"start": v(-109.35, -2.07) * mm, "end": v(-110.2, -1.78) * mm});
            skLineSegment(sketch, "E746", {"start": v(-110.2, -1.78) * mm, "end": v(-110.61, -1.63) * mm});
            skLineSegment(sketch, "E747", {"start": v(-110.61, -1.63) * mm, "end": v(-110.63, -0.5) * mm});
            skLineSegment(sketch, "E748", {"start": v(-110.63, -0.5) * mm, "end": v(-110.2, -0.33) * mm});
            skLineSegment(sketch, "E749", {"start": v(-110.2, -0.33) * mm, "end": v(-109.37, -0.03) * mm});
            skLineSegment(sketch, "E750", {"start": v(-109.37, -0.03) * mm, "end": v(-108.95, 0.12) * mm});
            skLineSegment(sketch, "E751", {"start": v(-108.95, 0.12) * mm, "end": v(-108.94, 1.27) * mm});
            skLineSegment(sketch, "E752", {"start": v(-108.94, 1.27) * mm, "end": v(-109.36, 1.42) * mm});
            skLineSegment(sketch, "E753", {"start": v(-109.36, 1.42) * mm, "end": v(-110.2, 1.73) * mm});
            skLineSegment(sketch, "E754", {"start": v(-110.2, 1.73) * mm, "end": v(-110.61, 1.9) * mm});
            skLineSegment(sketch, "E755", {"start": v(-110.61, 1.9) * mm, "end": v(-110.58, 3.03) * mm});
            skLineSegment(sketch, "E756", {"start": v(-110.58, 3.03) * mm, "end": v(-110.16, 3.18) * mm});
            skLineSegment(sketch, "E757", {"start": v(-110.16, 3.18) * mm, "end": v(-109.31, 3.46) * mm});
            skLineSegment(sketch, "E758", {"start": v(-109.31, 3.46) * mm, "end": v(-108.89, 3.59) * mm});
            skLineSegment(sketch, "E759", {"start": v(-108.89, 3.59) * mm, "end": v(-108.84, 4.74) * mm});
            skLineSegment(sketch, "E760", {"start": v(-108.84, 4.74) * mm, "end": v(-109.25, 4.9) * mm});
            skLineSegment(sketch, "E761", {"start": v(-109.25, 4.9) * mm, "end": v(-110.08, 5.25) * mm});
            skLineSegment(sketch, "E762", {"start": v(-110.08, 5.25) * mm, "end": v(-110.49, 5.43) * mm});
            skLineSegment(sketch, "E763", {"start": v(-110.49, 5.43) * mm, "end": v(-110.42, 6.56) * mm});
            skLineSegment(sketch, "E764", {"start": v(-110.42, 6.56) * mm, "end": v(-110, 6.7) * mm});
            skLineSegment(sketch, "E765", {"start": v(-110, 6.7) * mm, "end": v(-109.14, 6.94) * mm});
            skLineSegment(sketch, "E766", {"start": v(-109.14, 6.94) * mm, "end": v(-108.7, 7.06) * mm});
            skLineSegment(sketch, "E767", {"start": v(-108.7, 7.06) * mm, "end": v(-108.62, 8.2) * mm});
            skLineSegment(sketch, "E768", {"start": v(-108.62, 8.2) * mm, "end": v(-109.03, 8.38) * mm});
            skLineSegment(sketch, "E769", {"start": v(-109.03, 8.38) * mm, "end": v(-109.84, 8.75) * mm});
            skLineSegment(sketch, "E770", {"start": v(-109.84, 8.75) * mm, "end": v(-110.25, 8.95) * mm});
            skLineSegment(sketch, "E771", {"start": v(-110.25, 8.95) * mm, "end": v(-110.14, 10.07) * mm});
            skLineSegment(sketch, "E772", {"start": v(-110.14, 10.07) * mm, "end": v(-109.7, 10.2) * mm});
            skLineSegment(sketch, "E773", {"start": v(-109.7, 10.2) * mm, "end": v(-108.84, 10.41) * mm});
            skLineSegment(sketch, "E774", {"start": v(-108.84, 10.41) * mm, "end": v(-108.41, 10.52) * mm});
            skLineSegment(sketch, "E775", {"start": v(-108.41, 10.52) * mm, "end": v(-108.29, 11.66) * mm});
            skLineSegment(sketch, "E776", {"start": v(-108.29, 11.66) * mm, "end": v(-108.69, 11.85) * mm});
            skLineSegment(sketch, "E777", {"start": v(-108.69, 11.85) * mm, "end": v(-109.49, 12.25) * mm});
            skLineSegment(sketch, "E778", {"start": v(-109.49, 12.25) * mm, "end": v(-109.89, 12.46) * mm});
            skLineSegment(sketch, "E779", {"start": v(-109.89, 12.46) * mm, "end": v(-109.75, 13.58) * mm});
            skLineSegment(sketch, "E780", {"start": v(-109.75, 13.58) * mm, "end": v(-109.3, 13.68) * mm});
            skLineSegment(sketch, "E781", {"start": v(-109.3, 13.68) * mm, "end": v(-108.44, 13.88) * mm});
            skLineSegment(sketch, "E782", {"start": v(-108.44, 13.88) * mm, "end": v(-108, 13.96) * mm});
            skLineSegment(sketch, "E783", {"start": v(-108, 13.96) * mm, "end": v(-107.84, 15.1) * mm});
            skLineSegment(sketch, "E784", {"start": v(-107.84, 15.1) * mm, "end": v(-108.23, 15.3) * mm});
            skLineSegment(sketch, "E785", {"start": v(-108.23, 15.3) * mm, "end": v(-109.02, 15.73) * mm});
            skLineSegment(sketch, "E786", {"start": v(-109.02, 15.73) * mm, "end": v(-109.4, 15.95) * mm});
            skLineSegment(sketch, "E787", {"start": v(-109.4, 15.95) * mm, "end": v(-109.23, 17.07) * mm});
            skLineSegment(sketch, "E788", {"start": v(-109.23, 17.07) * mm, "end": v(-108.79, 17.16) * mm});
            skLineSegment(sketch, "E789", {"start": v(-108.79, 17.16) * mm, "end": v(-107.91, 17.32) * mm});
            skLineSegment(sketch, "E790", {"start": v(-107.91, 17.32) * mm, "end": v(-107.47, 17.4) * mm});
            skLineSegment(sketch, "E791", {"start": v(-107.47, 17.4) * mm, "end": v(-107.27, 18.52) * mm});
            skLineSegment(sketch, "E792", {"start": v(-107.27, 18.52) * mm, "end": v(-107.66, 18.74) * mm});
            skLineSegment(sketch, "E793", {"start": v(-107.66, 18.74) * mm, "end": v(-108.43, 19.2) * mm});
            skLineSegment(sketch, "E794", {"start": v(-108.43, 19.2) * mm, "end": v(-108.81, 19.43) * mm});
            skLineSegment(sketch, "E795", {"start": v(-108.81, 19.43) * mm, "end": v(-108.6, 20.54) * mm});
            skLineSegment(sketch, "E796", {"start": v(-108.6, 20.54) * mm, "end": v(-108.16, 20.62) * mm});
            skLineSegment(sketch, "E797", {"start": v(-108.16, 20.62) * mm, "end": v(-107.27, 20.75) * mm});
            skLineSegment(sketch, "E798", {"start": v(-107.27, 20.75) * mm, "end": v(-106.83, 20.8) * mm});
            skLineSegment(sketch, "E799", {"start": v(-106.83, 20.8) * mm, "end": v(-106.6, 21.93) * mm});
            skLineSegment(sketch, "E800", {"start": v(-106.6, 21.93) * mm, "end": v(-106.97, 22.16) * mm});
            skLineSegment(sketch, "E801", {"start": v(-106.97, 22.16) * mm, "end": v(-107.73, 22.64) * mm});
            skLineSegment(sketch, "E802", {"start": v(-107.73, 22.64) * mm, "end": v(-108.1, 22.89) * mm});
            skLineSegment(sketch, "E803", {"start": v(-108.1, 22.89) * mm, "end": v(-107.85, 23.99) * mm});
            skLineSegment(sketch, "E804", {"start": v(-107.85, 23.99) * mm, "end": v(-107.4, 24.05) * mm});
            skLineSegment(sketch, "E805", {"start": v(-107.4, 24.05) * mm, "end": v(-106.52, 24.15) * mm});
            skLineSegment(sketch, "E806", {"start": v(-106.52, 24.15) * mm, "end": v(-106.08, 24.2) * mm});
            skLineSegment(sketch, "E807", {"start": v(-106.08, 24.2) * mm, "end": v(-105.8, 25.3) * mm});
            skLineSegment(sketch, "E808", {"start": v(-105.8, 25.3) * mm, "end": v(-106.17, 25.55) * mm});
            skLineSegment(sketch, "E809", {"start": v(-106.17, 25.55) * mm, "end": v(-106.9, 26.06) * mm});
            skLineSegment(sketch, "E810", {"start": v(-106.9, 26.06) * mm, "end": v(-107.28, 26.32) * mm});
            skLineSegment(sketch, "E811", {"start": v(-107.28, 26.32) * mm, "end": v(-106.99, 27.4) * mm});
            skLineSegment(sketch, "E812", {"start": v(-106.99, 27.4) * mm, "end": v(-106.54, 27.45) * mm});
            skLineSegment(sketch, "E813", {"start": v(-106.54, 27.45) * mm, "end": v(-105.65, 27.53) * mm});
            skLineSegment(sketch, "E814", {"start": v(-105.65, 27.53) * mm, "end": v(-105.2, 27.55) * mm});
            skLineSegment(sketch, "E815", {"start": v(-105.2, 27.55) * mm, "end": v(-104.9, 28.66) * mm});
            skLineSegment(sketch, "E816", {"start": v(-104.9, 28.66) * mm, "end": v(-105.26, 28.92) * mm});
            skLineSegment(sketch, "E817", {"start": v(-105.26, 28.92) * mm, "end": v(-105.98, 29.44) * mm});
            skLineSegment(sketch, "E818", {"start": v(-105.98, 29.44) * mm, "end": v(-106.33, 29.72) * mm});
            skLineSegment(sketch, "E819", {"start": v(-106.33, 29.72) * mm, "end": v(-106, 30.8) * mm});
            skLineSegment(sketch, "E820", {"start": v(-106, 30.8) * mm, "end": v(-105.56, 30.83) * mm});
            skLineSegment(sketch, "E821", {"start": v(-105.56, 30.83) * mm, "end": v(-104.67, 30.87) * mm});
            skLineSegment(sketch, "E822", {"start": v(-104.67, 30.87) * mm, "end": v(-104.22, 30.88) * mm});
            skLineSegment(sketch, "E823", {"start": v(-104.22, 30.88) * mm, "end": v(-103.87, 31.98) * mm});
            skLineSegment(sketch, "E824", {"start": v(-103.87, 31.98) * mm, "end": v(-104.23, 32.25) * mm});
            skLineSegment(sketch, "E825", {"start": v(-104.23, 32.25) * mm, "end": v(-104.93, 32.8) * mm});
            skLineSegment(sketch, "E826", {"start": v(-104.93, 32.8) * mm, "end": v(-105.28, 33.08) * mm});
            skLineSegment(sketch, "E827", {"start": v(-105.28, 33.08) * mm, "end": v(-104.92, 34.15) * mm});
            skLineSegment(sketch, "E828", {"start": v(-104.92, 34.15) * mm, "end": v(-104.47, 34.17) * mm});
            skLineSegment(sketch, "E829", {"start": v(-104.47, 34.17) * mm, "end": v(-103.57, 34.18) * mm});
            skLineSegment(sketch, "E830", {"start": v(-103.57, 34.18) * mm, "end": v(-103.13, 34.18) * mm});
            skLineSegment(sketch, "E831", {"start": v(-103.13, 34.18) * mm, "end": v(-102.74, 35.26) * mm});
            skLineSegment(sketch, "E832", {"start": v(-102.74, 35.26) * mm, "end": v(-103.09, 35.54) * mm});
            skLineSegment(sketch, "E833", {"start": v(-103.09, 35.54) * mm, "end": v(-103.77, 36.12) * mm});
            skLineSegment(sketch, "E834", {"start": v(-103.77, 36.12) * mm, "end": v(-104.11, 36.41) * mm});
            skLineSegment(sketch, "E835", {"start": v(-104.11, 36.41) * mm, "end": v(-103.71, 37.47) * mm});
            skLineSegment(sketch, "E836", {"start": v(-103.71, 37.47) * mm, "end": v(-103.26, 37.47) * mm});
            skLineSegment(sketch, "E837", {"start": v(-103.26, 37.47) * mm, "end": v(-102.37, 37.45) * mm});
            skLineSegment(sketch, "E838", {"start": v(-102.37, 37.45) * mm, "end": v(-101.93, 37.44) * mm});
            skLineSegment(sketch, "E839", {"start": v(-101.93, 37.44) * mm, "end": v(-101.5, 38.5) * mm});
            skLineSegment(sketch, "E840", {"start": v(-101.5, 38.5) * mm, "end": v(-101.84, 38.8) * mm});
            skLineSegment(sketch, "E841", {"start": v(-101.84, 38.8) * mm, "end": v(-102.5, 39.4) * mm});
            skLineSegment(sketch, "E842", {"start": v(-102.5, 39.4) * mm, "end": v(-102.83, 39.7) * mm});
            skLineSegment(sketch, "E843", {"start": v(-102.83, 39.7) * mm, "end": v(-102.4, 40.74) * mm});
            skLineSegment(sketch, "E844", {"start": v(-102.4, 40.74) * mm, "end": v(-101.95, 40.73) * mm});
            skLineSegment(sketch, "E845", {"start": v(-101.95, 40.73) * mm, "end": v(-101.06, 40.68) * mm});
            skLineSegment(sketch, "E846", {"start": v(-101.06, 40.68) * mm, "end": v(-100.62, 40.65) * mm});
            skLineSegment(sketch, "E847", {"start": v(-100.62, 40.65) * mm, "end": v(-100.16, 41.7) * mm});
            skLineSegment(sketch, "E848", {"start": v(-100.16, 41.7) * mm, "end": v(-100.48, 42) * mm});
            skLineSegment(sketch, "E849", {"start": v(-100.48, 42) * mm, "end": v(-101.13, 42.63) * mm});
            skLineSegment(sketch, "E850", {"start": v(-101.13, 42.63) * mm, "end": v(-101.44, 42.94) * mm});
            skLineSegment(sketch, "E851", {"start": v(-101.44, 42.94) * mm, "end": v(-100.98, 43.97) * mm});
            skLineSegment(sketch, "E852", {"start": v(-100.98, 43.97) * mm, "end": v(-100.53, 43.94) * mm});
            skLineSegment(sketch, "E853", {"start": v(-100.53, 43.94) * mm, "end": v(-99.64, 43.87) * mm});
            skLineSegment(sketch, "E854", {"start": v(-99.64, 43.87) * mm, "end": v(-99.2, 43.82) * mm});
            skLineSegment(sketch, "E855", {"start": v(-99.2, 43.82) * mm, "end": v(-98.7, 44.86) * mm});
            skLineSegment(sketch, "E856", {"start": v(-98.7, 44.86) * mm, "end": v(-99.02, 45.17) * mm});
            skLineSegment(sketch, "E857", {"start": v(-99.02, 45.17) * mm, "end": v(-99.64, 45.81) * mm});
            skLineSegment(sketch, "E858", {"start": v(-99.64, 45.81) * mm, "end": v(-99.95, 46.14) * mm});
            skLineSegment(sketch, "E859", {"start": v(-99.95, 46.14) * mm, "end": v(-99.44, 47.15) * mm});
            skLineSegment(sketch, "E860", {"start": v(-99.44, 47.15) * mm, "end": v(-99, 47.1) * mm});
            skLineSegment(sketch, "E861", {"start": v(-99, 47.1) * mm, "end": v(-98.11, 47) * mm});
            skLineSegment(sketch, "E862", {"start": v(-98.11, 47) * mm, "end": v(-97.67, 46.94) * mm});
            skLineSegment(sketch, "E863", {"start": v(-97.67, 46.94) * mm, "end": v(-97.14, 47.96) * mm});
            skLineSegment(sketch, "E864", {"start": v(-97.14, 47.96) * mm, "end": v(-97.45, 48.28) * mm});
            skLineSegment(sketch, "E865", {"start": v(-97.45, 48.28) * mm, "end": v(-98.05, 48.94) * mm});
            skLineSegment(sketch, "E866", {"start": v(-98.05, 48.94) * mm, "end": v(-98.34, 49.28) * mm});
            skLineSegment(sketch, "E867", {"start": v(-98.34, 49.28) * mm, "end": v(-97.8, 50.28) * mm});
            skLineSegment(sketch, "E868", {"start": v(-97.8, 50.28) * mm, "end": v(-97.36, 50.22) * mm});
            skLineSegment(sketch, "E869", {"start": v(-97.36, 50.22) * mm, "end": v(-96.48, 50.08) * mm});
            skLineSegment(sketch, "E870", {"start": v(-96.48, 50.08) * mm, "end": v(-96.04, 50) * mm});
            skLineSegment(sketch, "E871", {"start": v(-96.04, 50) * mm, "end": v(-95.48, 51) * mm});
            skLineSegment(sketch, "E872", {"start": v(-95.48, 51) * mm, "end": v(-95.77, 51.34) * mm});
            skLineSegment(sketch, "E873", {"start": v(-95.77, 51.34) * mm, "end": v(-96.35, 52.02) * mm});
            skLineSegment(sketch, "E874", {"start": v(-96.35, 52.02) * mm, "end": v(-96.64, 52.37) * mm});
            skLineSegment(sketch, "E875", {"start": v(-96.64, 52.37) * mm, "end": v(-96.07, 53.34) * mm});
            skLineSegment(sketch, "E876", {"start": v(-96.07, 53.34) * mm, "end": v(-95.62, 53.27) * mm});
            skLineSegment(sketch, "E877", {"start": v(-95.62, 53.27) * mm, "end": v(-94.75, 53.1) * mm});
            skLineSegment(sketch, "E878", {"start": v(-94.75, 53.1) * mm, "end": v(-94.31, 53.01) * mm});
            skLineSegment(sketch, "E879", {"start": v(-94.31, 53.01) * mm, "end": v(-93.72, 54) * mm});
            skLineSegment(sketch, "E880", {"start": v(-93.72, 54) * mm, "end": v(-94, 54.34) * mm});
            skLineSegment(sketch, "E881", {"start": v(-94, 54.34) * mm, "end": v(-94.55, 55.04) * mm});
            skLineSegment(sketch, "E882", {"start": v(-94.55, 55.04) * mm, "end": v(-94.82, 55.4) * mm});
            skLineSegment(sketch, "E883", {"start": v(-94.82, 55.4) * mm, "end": v(-94.22, 56.35) * mm});
            skLineSegment(sketch, "E884", {"start": v(-94.22, 56.35) * mm, "end": v(-93.78, 56.26) * mm});
            skLineSegment(sketch, "E885", {"start": v(-93.78, 56.26) * mm, "end": v(-92.91, 56.07) * mm});
            skLineSegment(sketch, "E886", {"start": v(-92.91, 56.07) * mm, "end": v(-92.48, 55.96) * mm});
            skLineSegment(sketch, "E887", {"start": v(-92.48, 55.96) * mm, "end": v(-91.85, 56.92) * mm});
            skLineSegment(sketch, "E888", {"start": v(-91.85, 56.92) * mm, "end": v(-92.12, 57.28) * mm});
            skLineSegment(sketch, "E889", {"start": v(-92.12, 57.28) * mm, "end": v(-92.65, 58) * mm});
            skLineSegment(sketch, "E890", {"start": v(-92.65, 58) * mm, "end": v(-92.91, 58.36) * mm});
            skLineSegment(sketch, "E891", {"start": v(-92.91, 58.36) * mm, "end": v(-92.28, 59.3) * mm});
            skLineSegment(sketch, "E892", {"start": v(-92.28, 59.3) * mm, "end": v(-91.84, 59.2) * mm});
            skLineSegment(sketch, "E893", {"start": v(-91.84, 59.2) * mm, "end": v(-90.98, 58.97) * mm});
            skLineSegment(sketch, "E894", {"start": v(-90.98, 58.97) * mm, "end": v(-90.55, 58.85) * mm});
            skLineSegment(sketch, "E895", {"start": v(-90.55, 58.85) * mm, "end": v(-89.9, 59.79) * mm});
            skLineSegment(sketch, "E896", {"start": v(-89.9, 59.79) * mm, "end": v(-90.15, 60.15) * mm});
            skLineSegment(sketch, "E897", {"start": v(-90.15, 60.15) * mm, "end": v(-90.66, 60.89) * mm});
            skLineSegment(sketch, "E898", {"start": v(-90.66, 60.89) * mm, "end": v(-90.9, 61.26) * mm});
            skLineSegment(sketch, "E899", {"start": v(-90.9, 61.26) * mm, "end": v(-90.24, 62.18) * mm});
            skLineSegment(sketch, "E900", {"start": v(-90.24, 62.18) * mm, "end": v(-89.8, 62.06) * mm});
            skLineSegment(sketch, "E901", {"start": v(-89.8, 62.06) * mm, "end": v(-88.95, 61.8) * mm});
            skLineSegment(sketch, "E902", {"start": v(-88.95, 61.8) * mm, "end": v(-88.53, 61.67) * mm});
            skLineSegment(sketch, "E903", {"start": v(-88.53, 61.67) * mm, "end": v(-87.84, 62.59) * mm});
            skLineSegment(sketch, "E904", {"start": v(-87.84, 62.59) * mm, "end": v(-88.08, 62.96) * mm});
            skLineSegment(sketch, "E905", {"start": v(-88.08, 62.96) * mm, "end": v(-88.56, 63.7) * mm});
            skLineSegment(sketch, "E906", {"start": v(-88.56, 63.7) * mm, "end": v(-88.8, 64.1) * mm});
            skLineSegment(sketch, "E907", {"start": v(-88.8, 64.1) * mm, "end": v(-88.1, 64.98) * mm});
            skLineSegment(sketch, "E908", {"start": v(-88.1, 64.98) * mm, "end": v(-87.67, 64.85) * mm});
            skLineSegment(sketch, "E909", {"start": v(-87.67, 64.85) * mm, "end": v(-86.83, 64.57) * mm});
            skLineSegment(sketch, "E910", {"start": v(-86.83, 64.57) * mm, "end": v(-86.4, 64.42) * mm});
            skLineSegment(sketch, "E911", {"start": v(-86.4, 64.42) * mm, "end": v(-85.69, 65.31) * mm});
            skLineSegment(sketch, "E912", {"start": v(-85.69, 65.31) * mm, "end": v(-85.92, 65.69) * mm});
            skLineSegment(sketch, "E913", {"start": v(-85.92, 65.69) * mm, "end": v(-86.38, 66.46) * mm});
            skLineSegment(sketch, "E914", {"start": v(-86.38, 66.46) * mm, "end": v(-86.6, 66.85) * mm});
            skLineSegment(sketch, "E915", {"start": v(-86.6, 66.85) * mm, "end": v(-85.87, 67.72) * mm});
            skLineSegment(sketch, "E916", {"start": v(-85.87, 67.72) * mm, "end": v(-85.45, 67.57) * mm});
            skLineSegment(sketch, "E917", {"start": v(-85.45, 67.57) * mm, "end": v(-84.61, 67.26) * mm});
            skLineSegment(sketch, "E918", {"start": v(-84.61, 67.26) * mm, "end": v(-84.2, 67.1) * mm});
            skLineSegment(sketch, "E919", {"start": v(-84.2, 67.1) * mm, "end": v(-83.45, 67.97) * mm});
            skLineSegment(sketch, "E920", {"start": v(-83.45, 67.97) * mm, "end": v(-83.67, 68.35) * mm});
            skLineSegment(sketch, "E921", {"start": v(-83.67, 68.35) * mm, "end": v(-84.1, 69.13) * mm});
            skLineSegment(sketch, "E922", {"start": v(-84.1, 69.13) * mm, "end": v(-84.3, 69.53) * mm});
            skLineSegment(sketch, "E923", {"start": v(-84.3, 69.53) * mm, "end": v(-83.55, 70.37) * mm});
            skLineSegment(sketch, "E924", {"start": v(-83.55, 70.37) * mm, "end": v(-83.13, 70.21) * mm});
            skLineSegment(sketch, "E925", {"start": v(-83.13, 70.21) * mm, "end": v(-82.3, 69.87) * mm});
            skLineSegment(sketch, "E926", {"start": v(-82.3, 69.87) * mm, "end": v(-81.9, 69.7) * mm});
            skLineSegment(sketch, "E927", {"start": v(-81.9, 69.7) * mm, "end": v(-81.12, 70.54) * mm});
            skLineSegment(sketch, "E928", {"start": v(-81.12, 70.54) * mm, "end": v(-81.33, 70.93) * mm});
            skLineSegment(sketch, "E929", {"start": v(-81.33, 70.93) * mm, "end": v(-81.73, 71.73) * mm});
            skLineSegment(sketch, "E930", {"start": v(-81.73, 71.73) * mm, "end": v(-81.93, 72.14) * mm});
            skLineSegment(sketch, "E931", {"start": v(-81.93, 72.14) * mm, "end": v(-81.15, 72.95) * mm});
            skLineSegment(sketch, "E932", {"start": v(-81.15, 72.95) * mm, "end": v(-80.73, 72.78) * mm});
            skLineSegment(sketch, "E933", {"start": v(-80.73, 72.78) * mm, "end": v(-79.92, 72.41) * mm});
            skLineSegment(sketch, "E934", {"start": v(-79.92, 72.41) * mm, "end": v(-79.52, 72.22) * mm});
            skLineSegment(sketch, "E935", {"start": v(-79.52, 72.22) * mm, "end": v(-78.7, 73.04) * mm});
            skLineSegment(sketch, "E936", {"start": v(-78.7, 73.04) * mm, "end": v(-78.9, 73.44) * mm});
            skLineSegment(sketch, "E937", {"start": v(-78.9, 73.44) * mm, "end": v(-79.28, 74.25) * mm});
            skLineSegment(sketch, "E938", {"start": v(-79.28, 74.25) * mm, "end": v(-79.46, 74.66) * mm});
            skLineSegment(sketch, "E939", {"start": v(-79.46, 74.66) * mm, "end": v(-78.65, 75.45) * mm});
            skLineSegment(sketch, "E940", {"start": v(-78.65, 75.45) * mm, "end": v(-78.24, 75.26) * mm});
            skLineSegment(sketch, "E941", {"start": v(-78.24, 75.26) * mm, "end": v(-77.44, 74.87) * mm});
            skLineSegment(sketch, "E942", {"start": v(-77.44, 74.87) * mm, "end": v(-77.05, 74.66) * mm});
            skLineSegment(sketch, "E943", {"start": v(-77.05, 74.66) * mm, "end": v(-76.21, 75.45) * mm});
            skLineSegment(sketch, "E944", {"start": v(-76.21, 75.45) * mm, "end": v(-76.4, 75.86) * mm});
            skLineSegment(sketch, "E945", {"start": v(-76.4, 75.86) * mm, "end": v(-76.74, 76.68) * mm});
            skLineSegment(sketch, "E946", {"start": v(-76.74, 76.68) * mm, "end": v(-76.9, 77.1) * mm});
            skLineSegment(sketch, "E947", {"start": v(-76.9, 77.1) * mm, "end": v(-76.08, 77.86) * mm});
            skLineSegment(sketch, "E948", {"start": v(-76.08, 77.86) * mm, "end": v(-75.68, 77.66) * mm});
            skLineSegment(sketch, "E949", {"start": v(-75.68, 77.66) * mm, "end": v(-74.89, 77.24) * mm});
            skLineSegment(sketch, "E950", {"start": v(-74.89, 77.24) * mm, "end": v(-74.5, 77.02) * mm});
            skLineSegment(sketch, "E951", {"start": v(-74.5, 77.02) * mm, "end": v(-73.64, 77.78) * mm});
            skLineSegment(sketch, "E952", {"start": v(-73.64, 77.78) * mm, "end": v(-73.8, 78.2) * mm});
            skLineSegment(sketch, "E953", {"start": v(-73.8, 78.2) * mm, "end": v(-74.13, 79.03) * mm});
            skLineSegment(sketch, "E954", {"start": v(-74.13, 79.03) * mm, "end": v(-74.28, 79.45) * mm});
            skLineSegment(sketch, "E955", {"start": v(-74.28, 79.45) * mm, "end": v(-73.42, 80.18) * mm});
            skLineSegment(sketch, "E956", {"start": v(-73.42, 80.18) * mm, "end": v(-73.03, 79.97) * mm});
            skLineSegment(sketch, "E957", {"start": v(-73.03, 79.97) * mm, "end": v(-72.25, 79.52) * mm});
            skLineSegment(sketch, "E958", {"start": v(-72.25, 79.52) * mm, "end": v(-71.87, 79.3) * mm});
            skLineSegment(sketch, "E959", {"start": v(-71.87, 79.3) * mm, "end": v(-70.99, 80.02) * mm});
            skLineSegment(sketch, "E960", {"start": v(-70.99, 80.02) * mm, "end": v(-71.14, 80.44) * mm});
            skLineSegment(sketch, "E961", {"start": v(-71.14, 80.44) * mm, "end": v(-71.43, 81.28) * mm});
            skLineSegment(sketch, "E962", {"start": v(-71.43, 81.28) * mm, "end": v(-71.57, 81.71) * mm});
            skLineSegment(sketch, "E963", {"start": v(-71.57, 81.71) * mm, "end": v(-70.69, 82.42) * mm});
            skLineSegment(sketch, "E964", {"start": v(-70.69, 82.42) * mm, "end": v(-70.3, 82.18) * mm});
            skLineSegment(sketch, "E965", {"start": v(-70.3, 82.18) * mm, "end": v(-69.54, 81.71) * mm});
            skLineSegment(sketch, "E966", {"start": v(-69.54, 81.71) * mm, "end": v(-69.17, 81.47) * mm});
            skLineSegment(sketch, "E967", {"start": v(-69.17, 81.47) * mm, "end": v(-68.26, 82.17) * mm});
            skLineSegment(sketch, "E968", {"start": v(-68.26, 82.17) * mm, "end": v(-68.4, 82.6) * mm});
            skLineSegment(sketch, "E969", {"start": v(-68.4, 82.6) * mm, "end": v(-68.66, 83.45) * mm});
            skLineSegment(sketch, "E970", {"start": v(-68.66, 83.45) * mm, "end": v(-68.79, 83.88) * mm});
            skLineSegment(sketch, "E971", {"start": v(-68.79, 83.88) * mm, "end": v(-67.88, 84.55) * mm});
            skLineSegment(sketch, "E972", {"start": v(-67.88, 84.55) * mm, "end": v(-67.5, 84.31) * mm});
            skLineSegment(sketch, "E973", {"start": v(-67.5, 84.31) * mm, "end": v(-66.76, 83.81) * mm});
            skLineSegment(sketch, "E974", {"start": v(-66.76, 83.81) * mm, "end": v(-66.4, 83.56) * mm});
            skLineSegment(sketch, "E975", {"start": v(-66.4, 83.56) * mm, "end": v(-65.47, 84.23) * mm});
            skLineSegment(sketch, "E976", {"start": v(-65.47, 84.23) * mm, "end": v(-65.6, 84.66) * mm});
            skLineSegment(sketch, "E977", {"start": v(-65.6, 84.66) * mm, "end": v(-65.83, 85.52) * mm});
            skLineSegment(sketch, "E978", {"start": v(-65.83, 85.52) * mm, "end": v(-65.94, 85.95) * mm});
            skLineSegment(sketch, "E979", {"start": v(-65.94, 85.95) * mm, "end": v(-65, 86.6) * mm});
            skLineSegment(sketch, "E980", {"start": v(-65, 86.6) * mm, "end": v(-64.64, 86.34) * mm});
            skLineSegment(sketch, "E981", {"start": v(-64.64, 86.34) * mm, "end": v(-63.91, 85.82) * mm});
            skLineSegment(sketch, "E982", {"start": v(-63.91, 85.82) * mm, "end": v(-63.56, 85.55) * mm});
            skLineSegment(sketch, "E983", {"start": v(-63.56, 85.55) * mm, "end": v(-62.6, 86.2) * mm});
            skLineSegment(sketch, "E984", {"start": v(-62.6, 86.2) * mm, "end": v(-62.71, 86.62) * mm});
            skLineSegment(sketch, "E985", {"start": v(-62.71, 86.62) * mm, "end": v(-62.92, 87.5) * mm});
            skLineSegment(sketch, "E986", {"start": v(-62.92, 87.5) * mm, "end": v(-63.01, 87.93) * mm});
            skLineSegment(sketch, "E987", {"start": v(-63.01, 87.93) * mm, "end": v(-62.06, 88.54) * mm});
            skLineSegment(sketch, "E988", {"start": v(-62.06, 88.54) * mm, "end": v(-61.7, 88.28) * mm});
            skLineSegment(sketch, "E989", {"start": v(-61.7, 88.28) * mm, "end": v(-61, 87.73) * mm});
            skLineSegment(sketch, "E990", {"start": v(-61, 87.73) * mm, "end": v(-60.65, 87.45) * mm});
            skLineSegment(sketch, "E991", {"start": v(-60.65, 87.45) * mm, "end": v(-59.67, 88.06) * mm});
            skLineSegment(sketch, "E992", {"start": v(-59.67, 88.06) * mm, "end": v(-59.77, 88.5) * mm});
            skLineSegment(sketch, "E993", {"start": v(-59.77, 88.5) * mm, "end": v(-59.95, 89.37) * mm});
            skLineSegment(sketch, "E994", {"start": v(-59.95, 89.37) * mm, "end": v(-60.03, 89.81) * mm});
            skLineSegment(sketch, "E995", {"start": v(-60.03, 89.81) * mm, "end": v(-59.06, 90.4) * mm});
            skLineSegment(sketch, "E996", {"start": v(-59.06, 90.4) * mm, "end": v(-58.7, 90.11) * mm});
            skLineSegment(sketch, "E997", {"start": v(-58.7, 90.11) * mm, "end": v(-58.02, 89.54) * mm});
            skLineSegment(sketch, "E998", {"start": v(-58.02, 89.54) * mm, "end": v(-57.68, 89.25) * mm});
            skLineSegment(sketch, "E999", {"start": v(-57.68, 89.25) * mm, "end": v(-56.69, 89.82) * mm});
            skLineSegment(sketch, "E1000", {"start": v(-56.69, 89.82) * mm, "end": v(-56.77, 90.26) * mm});
            skLineSegment(sketch, "E1001", {"start": v(-56.77, 90.26) * mm, "end": v(-56.91, 91.14) * mm});
            skLineSegment(sketch, "E1002", {"start": v(-56.91, 91.14) * mm, "end": v(-56.98, 91.59) * mm});
            skLineSegment(sketch, "E1003", {"start": v(-56.98, 91.59) * mm, "end": v(-56, 92.13) * mm});
            skLineSegment(sketch, "E1004", {"start": v(-56, 92.13) * mm, "end": v(-55.65, 91.84) * mm});
            skLineSegment(sketch, "E1005", {"start": v(-55.65, 91.84) * mm, "end": v(-54.98, 91.25) * mm});
            skLineSegment(sketch, "E1006", {"start": v(-54.98, 91.25) * mm, "end": v(-54.65, 90.95) * mm});
            skLineSegment(sketch, "E1007", {"start": v(-54.65, 90.95) * mm, "end": v(-53.64, 91.49) * mm});
            skLineSegment(sketch, "E1008", {"start": v(-53.64, 91.49) * mm, "end": v(-53.7, 91.93) * mm});
            skLineSegment(sketch, "E1009", {"start": v(-53.7, 91.93) * mm, "end": v(-53.82, 92.81) * mm});
            skLineSegment(sketch, "E1010", {"start": v(-53.82, 92.81) * mm, "end": v(-53.87, 93.26) * mm});
            skLineSegment(sketch, "E1011", {"start": v(-53.87, 93.26) * mm, "end": v(-52.87, 93.77) * mm});
            skLineSegment(sketch, "E1012", {"start": v(-52.87, 93.77) * mm, "end": v(-52.54, 93.47) * mm});
            skLineSegment(sketch, "E1013", {"start": v(-52.54, 93.47) * mm, "end": v(-51.89, 92.86) * mm});
            skLineSegment(sketch, "E1014", {"start": v(-51.89, 92.86) * mm, "end": v(-51.57, 92.55) * mm});
            skLineSegment(sketch, "E1015", {"start": v(-51.57, 92.55) * mm, "end": v(-50.54, 93.05) * mm});
            skLineSegment(sketch, "E1016", {"start": v(-50.54, 93.05) * mm, "end": v(-50.6, 93.5) * mm});
            skLineSegment(sketch, "E1017", {"start": v(-50.6, 93.5) * mm, "end": v(-50.68, 94.38) * mm});
            skLineSegment(sketch, "E1018", {"start": v(-50.68, 94.38) * mm, "end": v(-50.71, 94.83) * mm});
            skLineSegment(sketch, "E1019", {"start": v(-50.71, 94.83) * mm, "end": v(-49.7, 95.3) * mm});
            skLineSegment(sketch, "E1020", {"start": v(-49.7, 95.3) * mm, "end": v(-49.37, 95) * mm});
            skLineSegment(sketch, "E1021", {"start": v(-49.37, 95) * mm, "end": v(-48.74, 94.36) * mm});
            skLineSegment(sketch, "E1022", {"start": v(-48.74, 94.36) * mm, "end": v(-48.44, 94.04) * mm});
            skLineSegment(sketch, "E1023", {"start": v(-48.44, 94.04) * mm, "end": v(-47.39, 94.5) * mm});
            skLineSegment(sketch, "E1024", {"start": v(-47.39, 94.5) * mm, "end": v(-47.42, 94.95) * mm});
            skLineSegment(sketch, "E1025", {"start": v(-47.42, 94.95) * mm, "end": v(-47.48, 95.84) * mm});
            skLineSegment(sketch, "E1026", {"start": v(-47.48, 95.84) * mm, "end": v(-47.5, 96.3) * mm});
            skLineSegment(sketch, "E1027", {"start": v(-47.5, 96.3) * mm, "end": v(-46.46, 96.74) * mm});
            skLineSegment(sketch, "E1028", {"start": v(-46.46, 96.74) * mm, "end": v(-46.15, 96.41) * mm});
            skLineSegment(sketch, "E1029", {"start": v(-46.15, 96.41) * mm, "end": v(-45.55, 95.75) * mm});
            skLineSegment(sketch, "E1030", {"start": v(-45.55, 95.75) * mm, "end": v(-45.25, 95.42) * mm});
            skLineSegment(sketch, "E1031", {"start": v(-45.25, 95.42) * mm, "end": v(-44.19, 95.86) * mm});
            skLineSegment(sketch, "E1032", {"start": v(-44.19, 95.86) * mm, "end": v(-44.21, 96.3) * mm});
            skLineSegment(sketch, "E1033", {"start": v(-44.21, 96.3) * mm, "end": v(-44.24, 97.2) * mm});
            skLineSegment(sketch, "E1034", {"start": v(-44.24, 97.2) * mm, "end": v(-44.24, 97.64) * mm});
            skLineSegment(sketch, "E1035", {"start": v(-44.24, 97.64) * mm, "end": v(-43.2, 98.05) * mm});
            skLineSegment(sketch, "E1036", {"start": v(-43.2, 98.05) * mm, "end": v(-42.9, 97.72) * mm});
            skLineSegment(sketch, "E1037", {"start": v(-42.9, 97.72) * mm, "end": v(-42.3, 97.04) * mm});
            skLineSegment(sketch, "E1038", {"start": v(-42.3, 97.04) * mm, "end": v(-42.02, 96.7) * mm});
            skLineSegment(sketch, "E1039", {"start": v(-42.02, 96.7) * mm, "end": v(-40.95, 97.1) * mm});
            skLineSegment(sketch, "E1040", {"start": v(-40.95, 97.1) * mm, "end": v(-40.95, 97.54) * mm});
            skLineSegment(sketch, "E1041", {"start": v(-40.95, 97.54) * mm, "end": v(-40.95, 98.44) * mm});
            skLineSegment(sketch, "E1042", {"start": v(-40.95, 98.44) * mm, "end": v(-40.94, 98.89) * mm});
            skLineSegment(sketch, "E1043", {"start": v(-40.94, 98.89) * mm, "end": v(-39.88, 99.26) * mm});
            skLineSegment(sketch, "E1044", {"start": v(-39.88, 99.26) * mm, "end": v(-39.59, 98.92) * mm});
            skLineSegment(sketch, "E1045", {"start": v(-39.59, 98.92) * mm, "end": v(-39.03, 98.22) * mm});
            skLineSegment(sketch, "E1046", {"start": v(-39.03, 98.22) * mm, "end": v(-38.75, 97.87) * mm});
            skLineSegment(sketch, "E1047", {"start": v(-38.75, 97.87) * mm, "end": v(-37.66, 98.23) * mm});
            skLineSegment(sketch, "E1048", {"start": v(-37.66, 98.23) * mm, "end": v(-37.66, 98.67) * mm});
            skLineSegment(sketch, "E1049", {"start": v(-37.66, 98.67) * mm, "end": v(-37.62, 99.57) * mm});
            skLineSegment(sketch, "E1050", {"start": v(-37.62, 99.57) * mm, "end": v(-37.6, 100.02) * mm});
            skLineSegment(sketch, "E1051", {"start": v(-37.6, 100.02) * mm, "end": v(-36.52, 100.35) * mm});
            skLineSegment(sketch, "E1052", {"start": v(-36.52, 100.35) * mm, "end": v(-36.25, 100) * mm});
            skLineSegment(sketch, "E1053", {"start": v(-36.25, 100) * mm, "end": v(-35.7, 99.29) * mm});
            skLineSegment(sketch, "E1054", {"start": v(-35.7, 99.29) * mm, "end": v(-35.45, 98.93) * mm});
            skLineSegment(sketch, "E1055", {"start": v(-35.45, 98.93) * mm, "end": v(-34.35, 99.25) * mm});
            skLineSegment(sketch, "E1056", {"start": v(-34.35, 99.25) * mm, "end": v(-34.32, 99.7) * mm});
            skLineSegment(sketch, "E1057", {"start": v(-34.32, 99.7) * mm, "end": v(-34.26, 100.59) * mm});
            skLineSegment(sketch, "E1058", {"start": v(-34.26, 100.59) * mm, "end": v(-34.22, 101.03) * mm});
            skLineSegment(sketch, "E1059", {"start": v(-34.22, 101.03) * mm, "end": v(-33.13, 101.34) * mm});
            skLineSegment(sketch, "E1060", {"start": v(-33.13, 101.34) * mm, "end": v(-32.87, 100.97) * mm});
            skLineSegment(sketch, "E1061", {"start": v(-32.87, 100.97) * mm, "end": v(-32.36, 100.24) * mm});
            skLineSegment(sketch, "E1062", {"start": v(-32.36, 100.24) * mm, "end": v(-32.1, 99.87) * mm});
            skLineSegment(sketch, "E1063", {"start": v(-32.1, 99.87) * mm, "end": v(-31, 100.16) * mm});
            skLineSegment(sketch, "E1064", {"start": v(-31, 100.16) * mm, "end": v(-30.96, 100.6) * mm});
            skLineSegment(sketch, "E1065", {"start": v(-30.96, 100.6) * mm, "end": v(-30.87, 101.5) * mm});
            skLineSegment(sketch, "E1066", {"start": v(-30.87, 101.5) * mm, "end": v(-30.81, 101.94) * mm});
            skLineSegment(sketch, "E1067", {"start": v(-30.81, 101.94) * mm, "end": v(-29.71, 102.2) * mm});
            skLineSegment(sketch, "E1068", {"start": v(-29.71, 102.2) * mm, "end": v(-29.46, 101.83) * mm});
            skLineSegment(sketch, "E1069", {"start": v(-29.46, 101.83) * mm, "end": v(-28.97, 101.08) * mm});
            skLineSegment(sketch, "E1070", {"start": v(-28.97, 101.08) * mm, "end": v(-28.74, 100.7) * mm});
            skLineSegment(sketch, "E1071", {"start": v(-28.74, 100.7) * mm, "end": v(-27.62, 100.96) * mm});
            skLineSegment(sketch, "E1072", {"start": v(-27.62, 100.96) * mm, "end": v(-27.56, 101.4) * mm});
            skLineSegment(sketch, "E1073", {"start": v(-27.56, 101.4) * mm, "end": v(-27.44, 102.28) * mm});
            skLineSegment(sketch, "E1074", {"start": v(-27.44, 102.28) * mm, "end": v(-27.37, 102.73) * mm});
            skLineSegment(sketch, "E1075", {"start": v(-27.37, 102.73) * mm, "end": v(-26.27, 102.95) * mm});
            skLineSegment(sketch, "E1076", {"start": v(-26.27, 102.95) * mm, "end": v(-26.03, 102.57) * mm});
            skLineSegment(sketch, "E1077", {"start": v(-26.03, 102.57) * mm, "end": v(-25.56, 101.81) * mm});
            skLineSegment(sketch, "E1078", {"start": v(-25.56, 101.81) * mm, "end": v(-25.34, 101.43) * mm});
            skLineSegment(sketch, "E1079", {"start": v(-25.34, 101.43) * mm, "end": v(-24.21, 101.64) * mm});
            skLineSegment(sketch, "E1080", {"start": v(-24.21, 101.64) * mm, "end": v(-24.15, 102.08) * mm});
            skLineSegment(sketch, "E1081", {"start": v(-24.15, 102.08) * mm, "end": v(-24, 102.96) * mm});
            skLineSegment(sketch, "E1082", {"start": v(-24, 102.96) * mm, "end": v(-23.9, 103.4) * mm});
            skLineSegment(sketch, "E1083", {"start": v(-23.9, 103.4) * mm, "end": v(-22.8, 103.6) * mm});
            skLineSegment(sketch, "E1084", {"start": v(-22.8, 103.6) * mm, "end": v(-22.57, 103.2) * mm});
            skLineSegment(sketch, "E1085", {"start": v(-22.57, 103.2) * mm, "end": v(-22.13, 102.42) * mm});
            skLineSegment(sketch, "E1086", {"start": v(-22.13, 102.42) * mm, "end": v(-21.92, 102.03) * mm});
            skLineSegment(sketch, "E1087", {"start": v(-21.92, 102.03) * mm, "end": v(-20.79, 102.2) * mm});
            skLineSegment(sketch, "E1088", {"start": v(-20.79, 102.2) * mm, "end": v(-20.7, 102.64) * mm});
            skLineSegment(sketch, "E1089", {"start": v(-20.7, 102.64) * mm, "end": v(-20.52, 103.52) * mm});
            skLineSegment(sketch, "E1090", {"start": v(-20.52, 103.52) * mm, "end": v(-20.43, 103.96) * mm});
            skLineSegment(sketch, "E1091", {"start": v(-20.43, 103.96) * mm, "end": v(-19.3, 104.1) * mm});
            skLineSegment(sketch, "E1092", {"start": v(-19.3, 104.1) * mm, "end": v(-19.1, 103.71) * mm});
            skLineSegment(sketch, "E1093", {"start": v(-19.1, 103.71) * mm, "end": v(-18.68, 102.92) * mm});
            skLineSegment(sketch, "E1094", {"start": v(-18.68, 102.92) * mm, "end": v(-18.49, 102.52) * mm});
            skLineSegment(sketch, "E1095", {"start": v(-18.49, 102.52) * mm, "end": v(-17.35, 102.66) * mm});
            skLineSegment(sketch, "E1096", {"start": v(-17.35, 102.66) * mm, "end": v(-17.25, 103.1) * mm});
            skLineSegment(sketch, "E1097", {"start": v(-17.25, 103.1) * mm, "end": v(-17.04, 103.96) * mm});
            skLineSegment(sketch, "E1098", {"start": v(-17.04, 103.96) * mm, "end": v(-16.92, 104.4) * mm});
            skLineSegment(sketch, "E1099", {"start": v(-16.92, 104.4) * mm, "end": v(-15.8, 104.5) * mm});
            skLineSegment(sketch, "E1100", {"start": v(-15.8, 104.5) * mm, "end": v(-15.6, 104.1) * mm});
            skLineSegment(sketch, "E1101", {"start": v(-15.6, 104.1) * mm, "end": v(-15.22, 103.3) * mm});
            skLineSegment(sketch, "E1102", {"start": v(-15.22, 103.3) * mm, "end": v(-15.04, 102.9) * mm});
            skLineSegment(sketch, "E1103", {"start": v(-15.04, 102.9) * mm, "end": v(-13.9, 103) * mm});
            skLineSegment(sketch, "E1104", {"start": v(-13.9, 103) * mm, "end": v(-13.78, 103.42) * mm});
            skLineSegment(sketch, "E1105", {"start": v(-13.78, 103.42) * mm, "end": v(-13.54, 104.28) * mm});
            skLineSegment(sketch, "E1106", {"start": v(-13.54, 104.28) * mm, "end": v(-13.41, 104.72) * mm});
            skLineSegment(sketch, "E1107", {"start": v(-13.41, 104.72) * mm, "end": v(-12.28, 104.8) * mm});
            skLineSegment(sketch, "E1108", {"start": v(-12.28, 104.8) * mm, "end": v(-12.1, 104.38) * mm});
            skLineSegment(sketch, "E1109", {"start": v(-12.1, 104.38) * mm, "end": v(-11.74, 103.56) * mm});
            skLineSegment(sketch, "E1110", {"start": v(-11.74, 103.56) * mm, "end": v(-11.57, 103.15) * mm});
            skLineSegment(sketch, "E1111", {"start": v(-11.57, 103.15) * mm, "end": v(-10.43, 103.21) * mm});
            skLineSegment(sketch, "E1112", {"start": v(-10.43, 103.21) * mm, "end": v(-10.3, 103.64) * mm});
            skLineSegment(sketch, "E1113", {"start": v(-10.3, 103.64) * mm, "end": v(-10.03, 104.5) * mm});
            skLineSegment(sketch, "E1114", {"start": v(-10.03, 104.5) * mm, "end": v(-9.89, 104.92) * mm});
            skLineSegment(sketch, "E1115", {"start": v(-9.89, 104.92) * mm, "end": v(-8.76, 104.96) * mm});
            skLineSegment(sketch, "E1116", {"start": v(-8.76, 104.96) * mm, "end": v(-8.59, 104.54) * mm});
            skLineSegment(sketch, "E1117", {"start": v(-8.59, 104.54) * mm, "end": v(-8.26, 103.71) * mm});
            skLineSegment(sketch, "E1118", {"start": v(-8.26, 103.71) * mm, "end": v(-8.1, 103.3) * mm});
            skLineSegment(sketch, "E1119", {"start": v(-8.1, 103.3) * mm, "end": v(-6.96, 103.32) * mm});
            skLineSegment(sketch, "E1120", {"start": v(-6.96, 103.32) * mm, "end": v(-6.82, 103.74) * mm});
            skLineSegment(sketch, "E1121", {"start": v(-6.82, 103.74) * mm, "end": v(-6.52, 104.58) * mm});
            skLineSegment(sketch, "E1122", {"start": v(-6.52, 104.58) * mm, "end": v(-6.36, 105) * mm});
            skLineSegment(sketch, "E1123", {"start": v(-6.36, 105) * mm, "end": v(-5.23, 105) * mm});
            skLineSegment(sketch, "E1124", {"start": v(-5.23, 105) * mm, "end": v(-5.07, 104.58) * mm});
            skLineSegment(sketch, "E1125", {"start": v(-5.07, 104.58) * mm, "end": v(-4.77, 103.74) * mm});
            skLineSegment(sketch, "E1126", {"start": v(-4.77, 103.74) * mm, "end": v(-4.63, 103.32) * mm});
            skLineSegment(sketch, "E1127", {"start": v(-4.63, 103.32) * mm, "end": v(-3.48, 103.3) * mm});
            skLineSegment(sketch, "E1128", {"start": v(-3.48, 103.3) * mm, "end": v(-3.33, 103.72) * mm});
            skLineSegment(sketch, "E1129", {"start": v(-3.33, 103.72) * mm, "end": v(-3, 104.55) * mm});
            skLineSegment(sketch, "E1130", {"start": v(-3, 104.55) * mm, "end": v(-2.83, 104.97) * mm});
            skLineSegment(sketch, "E1131", {"start": v(-2.83, 104.97) * mm, "end": v(-1.7, 104.93) * mm});
            skLineSegment(sketch, "E1132", {"start": v(-1.7, 104.93) * mm, "end": v(-1.56, 104.5) * mm});
            skLineSegment(sketch, "E1133", {"start": v(-1.56, 104.5) * mm, "end": v(-1.29, 103.65) * mm});
            skLineSegment(sketch, "E1134", {"start": v(-1.29, 103.65) * mm, "end": v(-1.16, 103.23) * mm});
            skLineSegment(sketch, "E1135", {"start": v(-1.16, 103.23) * mm, "end": v(-0.02, 103.17) * mm});
            skLineSegment(sketch, "E1136", {"start": v(-0.02, 103.17) * mm, "end": v(0.15, 103.58) * mm});
            skLineSegment(sketch, "E1137", {"start": v(0.15, 103.58) * mm, "end": v(0.5, 104.4) * mm});
            skLineSegment(sketch, "E1138", {"start": v(0.5, 104.4) * mm, "end": v(0.7, 104.81) * mm});
            skLineSegment(sketch, "E1139", {"start": v(0.7, 104.81) * mm, "end": v(1.82, 104.74) * mm});
            skLineSegment(sketch, "E1140", {"start": v(1.82, 104.74) * mm, "end": v(1.95, 104.31) * mm});
            skLineSegment(sketch, "E1141", {"start": v(1.95, 104.31) * mm, "end": v(2.2, 103.45) * mm});
            skLineSegment(sketch, "E1142", {"start": v(2.2, 103.45) * mm, "end": v(2.3, 103.02) * mm});
            skLineSegment(sketch, "E1143", {"start": v(2.3, 103.02) * mm, "end": v(3.45, 102.93) * mm});
            skLineSegment(sketch, "E1144", {"start": v(3.45, 102.93) * mm, "end": v(3.63, 103.33) * mm});
            skLineSegment(sketch, "E1145", {"start": v(3.63, 103.33) * mm, "end": v(4, 104.14) * mm});
            skLineSegment(sketch, "E1146", {"start": v(4, 104.14) * mm, "end": v(4.2, 104.54) * mm});
            skLineSegment(sketch, "E1147", {"start": v(4.2, 104.54) * mm, "end": v(5.33, 104.43) * mm});
            skLineSegment(sketch, "E1148", {"start": v(5.33, 104.43) * mm, "end": v(5.45, 104) * mm});
            skLineSegment(sketch, "E1149", {"start": v(5.45, 104) * mm, "end": v(5.66, 103.13) * mm});
            skLineSegment(sketch, "E1150", {"start": v(5.66, 103.13) * mm, "end": v(5.76, 102.7) * mm});
            skLineSegment(sketch, "E1151", {"start": v(5.76, 102.7) * mm, "end": v(6.9, 102.56) * mm});
            skLineSegment(sketch, "E1152", {"start": v(6.9, 102.56) * mm, "end": v(7.1, 102.96) * mm});
            skLineSegment(sketch, "E1153", {"start": v(7.1, 102.96) * mm, "end": v(7.5, 103.76) * mm});
            skLineSegment(sketch, "E1154", {"start": v(7.5, 103.76) * mm, "end": v(7.71, 104.15) * mm});
            skLineSegment(sketch, "E1155", {"start": v(7.71, 104.15) * mm, "end": v(8.83, 104) * mm});
            skLineSegment(sketch, "E1156", {"start": v(8.83, 104) * mm, "end": v(8.94, 103.57) * mm});
            skLineSegment(sketch, "E1157", {"start": v(8.94, 103.57) * mm, "end": v(9.12, 102.7) * mm});
            skLineSegment(sketch, "E1158", {"start": v(9.12, 102.7) * mm, "end": v(9.2, 102.26) * mm});
            skLineSegment(sketch, "E1159", {"start": v(9.2, 102.26) * mm, "end": v(10.34, 102.09) * mm});
            skLineSegment(sketch, "E1160", {"start": v(10.34, 102.09) * mm, "end": v(10.55, 102.48) * mm});
            skLineSegment(sketch, "E1161", {"start": v(10.55, 102.48) * mm, "end": v(10.98, 103.26) * mm});
            skLineSegment(sketch, "E1162", {"start": v(10.98, 103.26) * mm, "end": v(11.2, 103.65) * mm});
            skLineSegment(sketch, "E1163", {"start": v(11.2, 103.65) * mm, "end": v(12.32, 103.46) * mm});
            skLineSegment(sketch, "E1164", {"start": v(12.32, 103.46) * mm, "end": v(12.4, 103.02) * mm});
            skLineSegment(sketch, "E1165", {"start": v(12.4, 103.02) * mm, "end": v(12.56, 102.14) * mm});
            skLineSegment(sketch, "E1166", {"start": v(12.56, 102.14) * mm, "end": v(12.63, 101.7) * mm});
            skLineSegment(sketch, "E1167", {"start": v(12.63, 101.7) * mm, "end": v(13.76, 101.5) * mm});
            skLineSegment(sketch, "E1168", {"start": v(13.76, 101.5) * mm, "end": v(13.98, 101.88) * mm});
            skLineSegment(sketch, "E1169", {"start": v(13.98, 101.88) * mm, "end": v(14.44, 102.64) * mm});
            skLineSegment(sketch, "E1170", {"start": v(14.44, 102.64) * mm, "end": v(14.68, 103.02) * mm});
            skLineSegment(sketch, "E1171", {"start": v(14.68, 103.02) * mm, "end": v(15.79, 102.8) * mm});
            skLineSegment(sketch, "E1172", {"start": v(15.79, 102.8) * mm, "end": v(15.86, 102.36) * mm});
            skLineSegment(sketch, "E1173", {"start": v(15.86, 102.36) * mm, "end": v(15.98, 101.47) * mm});
            skLineSegment(sketch, "E1174", {"start": v(15.98, 101.47) * mm, "end": v(16.04, 101.03) * mm});
            skLineSegment(sketch, "E1175", {"start": v(16.04, 101.03) * mm, "end": v(17.16, 100.78) * mm});
            skLineSegment(sketch, "E1176", {"start": v(17.16, 100.78) * mm, "end": v(17.4, 101.16) * mm});
            skLineSegment(sketch, "E1177", {"start": v(17.4, 101.16) * mm, "end": v(17.88, 101.91) * mm});
            skLineSegment(sketch, "E1178", {"start": v(17.88, 101.91) * mm, "end": v(18.13, 102.28) * mm});
            skLineSegment(sketch, "E1179", {"start": v(18.13, 102.28) * mm, "end": v(19.23, 102.02) * mm});
            skLineSegment(sketch, "E1180", {"start": v(19.23, 102.02) * mm, "end": v(19.28, 101.58) * mm});
            skLineSegment(sketch, "E1181", {"start": v(19.28, 101.58) * mm, "end": v(19.38, 100.69) * mm});
            skLineSegment(sketch, "E1182", {"start": v(19.38, 100.69) * mm, "end": v(19.42, 100.25) * mm});
            skLineSegment(sketch, "E1183", {"start": v(19.42, 100.25) * mm, "end": v(20.53, 99.96) * mm});
            skLineSegment(sketch, "E1184", {"start": v(20.53, 99.96) * mm, "end": v(20.78, 100.33) * mm});
            skLineSegment(sketch, "E1185", {"start": v(20.78, 100.33) * mm, "end": v(21.29, 101.06) * mm});
            skLineSegment(sketch, "E1186", {"start": v(21.29, 101.06) * mm, "end": v(21.55, 101.43) * mm});
            skLineSegment(sketch, "E1187", {"start": v(21.55, 101.43) * mm, "end": v(22.64, 101.13) * mm});
            skLineSegment(sketch, "E1188", {"start": v(22.64, 101.13) * mm, "end": v(22.68, 100.68) * mm});
            skLineSegment(sketch, "E1189", {"start": v(22.68, 100.68) * mm, "end": v(22.75, 99.8) * mm});
            skLineSegment(sketch, "E1190", {"start": v(22.75, 99.8) * mm, "end": v(22.77, 99.35) * mm});
            skLineSegment(sketch, "E1191", {"start": v(22.77, 99.35) * mm, "end": v(23.87, 99.03) * mm});
            skLineSegment(sketch, "E1192", {"start": v(23.87, 99.03) * mm, "end": v(24.13, 99.39) * mm});
            skLineSegment(sketch, "E1193", {"start": v(24.13, 99.39) * mm, "end": v(24.67, 100.1) * mm});
            skLineSegment(sketch, "E1194", {"start": v(24.67, 100.1) * mm, "end": v(24.94, 100.46) * mm});
            skLineSegment(sketch, "E1195", {"start": v(24.94, 100.46) * mm, "end": v(26.02, 100.12) * mm});
            skLineSegment(sketch, "E1196", {"start": v(26.02, 100.12) * mm, "end": v(26.05, 99.67) * mm});
            skLineSegment(sketch, "E1197", {"start": v(26.05, 99.67) * mm, "end": v(26.08, 98.78) * mm});
            skLineSegment(sketch, "E1198", {"start": v(26.08, 98.78) * mm, "end": v(26.1, 98.34) * mm});
            skLineSegment(sketch, "E1199", {"start": v(26.1, 98.34) * mm, "end": v(27.18, 97.98) * mm});
            skLineSegment(sketch, "E1200", {"start": v(27.18, 97.98) * mm, "end": v(27.45, 98.33) * mm});
            skLineSegment(sketch, "E1201", {"start": v(27.45, 98.33) * mm, "end": v(28.01, 99.03) * mm});
            skLineSegment(sketch, "E1202", {"start": v(28.01, 99.03) * mm, "end": v(28.3, 99.37) * mm});
            skLineSegment(sketch, "E1203", {"start": v(28.3, 99.37) * mm, "end": v(29.37, 99) * mm});
            skLineSegment(sketch, "E1204", {"start": v(29.37, 99) * mm, "end": v(29.38, 98.55) * mm});
            skLineSegment(sketch, "E1205", {"start": v(29.38, 98.55) * mm, "end": v(29.38, 97.66) * mm});
            skLineSegment(sketch, "E1206", {"start": v(29.38, 97.66) * mm, "end": v(29.38, 97.22) * mm});
            skLineSegment(sketch, "E1207", {"start": v(29.38, 97.22) * mm, "end": v(30.46, 96.82) * mm});
            skLineSegment(sketch, "E1208", {"start": v(30.46, 96.82) * mm, "end": v(30.74, 97.16) * mm});
            skLineSegment(sketch, "E1209", {"start": v(30.74, 97.16) * mm, "end": v(31.32, 97.84) * mm});
            skLineSegment(sketch, "E1210", {"start": v(31.32, 97.84) * mm, "end": v(31.62, 98.18) * mm});
            skLineSegment(sketch, "E1211", {"start": v(31.62, 98.18) * mm, "end": v(32.67, 97.77) * mm});
            skLineSegment(sketch, "E1212", {"start": v(32.67, 97.77) * mm, "end": v(32.67, 97.32) * mm});
            skLineSegment(sketch, "E1213", {"start": v(32.67, 97.32) * mm, "end": v(32.65, 96.43) * mm});
            skLineSegment(sketch, "E1214", {"start": v(32.65, 96.43) * mm, "end": v(32.62, 95.99) * mm});
            skLineSegment(sketch, "E1215", {"start": v(32.62, 95.99) * mm, "end": v(33.69, 95.56) * mm});
            skLineSegment(sketch, "E1216", {"start": v(33.69, 95.56) * mm, "end": v(33.98, 95.89) * mm});
            skLineSegment(sketch, "E1217", {"start": v(33.98, 95.89) * mm, "end": v(34.59, 96.55) * mm});
            skLineSegment(sketch, "E1218", {"start": v(34.59, 96.55) * mm, "end": v(34.9, 96.87) * mm});
            skLineSegment(sketch, "E1219", {"start": v(34.9, 96.87) * mm, "end": v(35.94, 96.43) * mm});
            skLineSegment(sketch, "E1220", {"start": v(35.94, 96.43) * mm, "end": v(35.92, 95.98) * mm});
            skLineSegment(sketch, "E1221", {"start": v(35.92, 95.98) * mm, "end": v(35.86, 95.1) * mm});
            skLineSegment(sketch, "E1222", {"start": v(35.86, 95.1) * mm, "end": v(35.83, 94.65) * mm});
            skLineSegment(sketch, "E1223", {"start": v(35.83, 94.65) * mm, "end": v(36.88, 94.18) * mm});
            skLineSegment(sketch, "E1224", {"start": v(36.88, 94.18) * mm, "end": v(37.18, 94.5) * mm});
            skLineSegment(sketch, "E1225", {"start": v(37.18, 94.5) * mm, "end": v(37.8, 95.14) * mm});
            skLineSegment(sketch, "E1226", {"start": v(37.8, 95.14) * mm, "end": v(38.13, 95.46) * mm});
            skLineSegment(sketch, "E1227", {"start": v(38.13, 95.46) * mm, "end": v(39.15, 94.98) * mm});
            skLineSegment(sketch, "E1228", {"start": v(39.15, 94.98) * mm, "end": v(39.12, 94.53) * mm});
            skLineSegment(sketch, "E1229", {"start": v(39.12, 94.53) * mm, "end": v(39.03, 93.64) * mm});
            skLineSegment(sketch, "E1230", {"start": v(39.03, 93.64) * mm, "end": v(38.98, 93.2) * mm});
            skLineSegment(sketch, "E1231", {"start": v(38.98, 93.2) * mm, "end": v(40.02, 92.7) * mm});
            skLineSegment(sketch, "E1232", {"start": v(40.02, 92.7) * mm, "end": v(40.33, 93.01) * mm});
            skLineSegment(sketch, "E1233", {"start": v(40.33, 93.01) * mm, "end": v(40.98, 93.63) * mm});
            skLineSegment(sketch, "E1234", {"start": v(40.98, 93.63) * mm, "end": v(41.31, 93.93) * mm});
            skLineSegment(sketch, "E1235", {"start": v(41.31, 93.93) * mm, "end": v(42.32, 93.42) * mm});
            skLineSegment(sketch, "E1236", {"start": v(42.32, 93.42) * mm, "end": v(42.27, 92.98) * mm});
            skLineSegment(sketch, "E1237", {"start": v(42.27, 92.98) * mm, "end": v(42.16, 92.09) * mm});
            skLineSegment(sketch, "E1238", {"start": v(42.16, 92.09) * mm, "end": v(42.1, 91.65) * mm});
            skLineSegment(sketch, "E1239", {"start": v(42.1, 91.65) * mm, "end": v(43.1, 91.11) * mm});
            skLineSegment(sketch, "E1240", {"start": v(43.1, 91.11) * mm, "end": v(43.43, 91.42) * mm});
            skLineSegment(sketch, "E1241", {"start": v(43.43, 91.42) * mm, "end": v(44.1, 92.01) * mm});
            skLineSegment(sketch, "E1242", {"start": v(44.1, 92.01) * mm, "end": v(44.44, 92.3) * mm});
            skLineSegment(sketch, "E1243", {"start": v(44.44, 92.3) * mm, "end": v(45.43, 91.76) * mm});
            skLineSegment(sketch, "E1244", {"start": v(45.43, 91.76) * mm, "end": v(45.37, 91.31) * mm});
            skLineSegment(sketch, "E1245", {"start": v(45.37, 91.31) * mm, "end": v(45.22, 90.43) * mm});
            skLineSegment(sketch, "E1246", {"start": v(45.22, 90.43) * mm, "end": v(45.14, 90) * mm});
            skLineSegment(sketch, "E1247", {"start": v(45.14, 90) * mm, "end": v(46.14, 89.43) * mm});
            skLineSegment(sketch, "E1248", {"start": v(46.14, 89.43) * mm, "end": v(46.48, 89.72) * mm});
            skLineSegment(sketch, "E1249", {"start": v(46.48, 89.72) * mm, "end": v(47.16, 90.29) * mm});
            skLineSegment(sketch, "E1250", {"start": v(47.16, 90.29) * mm, "end": v(47.51, 90.57) * mm});
            skLineSegment(sketch, "E1251", {"start": v(47.51, 90.57) * mm, "end": v(48.48, 90) * mm});
            skLineSegment(sketch, "E1252", {"start": v(48.48, 90) * mm, "end": v(48.4, 89.55) * mm});
            skLineSegment(sketch, "E1253", {"start": v(48.4, 89.55) * mm, "end": v(48.23, 88.67) * mm});
            skLineSegment(sketch, "E1254", {"start": v(48.23, 88.67) * mm, "end": v(48.14, 88.24) * mm});
            skLineSegment(sketch, "E1255", {"start": v(48.14, 88.24) * mm, "end": v(49.11, 87.64) * mm});
            skLineSegment(sketch, "E1256", {"start": v(49.11, 87.64) * mm, "end": v(49.46, 87.92) * mm});
            skLineSegment(sketch, "E1257", {"start": v(49.46, 87.92) * mm, "end": v(50.17, 88.46) * mm});
            skLineSegment(sketch, "E1258", {"start": v(50.17, 88.46) * mm, "end": v(50.53, 88.73) * mm});
            skLineSegment(sketch, "E1259", {"start": v(50.53, 88.73) * mm, "end": v(51.48, 88.12) * mm});
            skLineSegment(sketch, "E1260", {"start": v(51.48, 88.12) * mm, "end": v(51.38, 87.68) * mm});
            skLineSegment(sketch, "E1261", {"start": v(51.38, 87.68) * mm, "end": v(51.18, 86.81) * mm});
            skLineSegment(sketch, "E1262", {"start": v(51.18, 86.81) * mm, "end": v(51.07, 86.38) * mm});
            skLineSegment(sketch, "E1263", {"start": v(51.07, 86.38) * mm, "end": v(52.03, 85.75) * mm});
            skLineSegment(sketch, "E1264", {"start": v(52.03, 85.75) * mm, "end": v(52.38, 86.02) * mm});
            skLineSegment(sketch, "E1265", {"start": v(52.38, 86.02) * mm, "end": v(53.1, 86.54) * mm});
            skLineSegment(sketch, "E1266", {"start": v(53.1, 86.54) * mm, "end": v(53.47, 86.8) * mm});
            skLineSegment(sketch, "E1267", {"start": v(53.47, 86.8) * mm, "end": v(54.4, 86.16) * mm});
            skLineSegment(sketch, "E1268", {"start": v(54.4, 86.16) * mm, "end": v(54.3, 85.72) * mm});
            skLineSegment(sketch, "E1269", {"start": v(54.3, 85.72) * mm, "end": v(54.06, 84.86) * mm});
            skLineSegment(sketch, "E1270", {"start": v(54.06, 84.86) * mm, "end": v(53.94, 84.43) * mm});
            skLineSegment(sketch, "E1271", {"start": v(53.94, 84.43) * mm, "end": v(54.88, 83.76) * mm});
            skLineSegment(sketch, "E1272", {"start": v(54.88, 83.76) * mm, "end": v(55.24, 84.02) * mm});
            skLineSegment(sketch, "E1273", {"start": v(55.24, 84.02) * mm, "end": v(55.98, 84.52) * mm});
            skLineSegment(sketch, "E1274", {"start": v(55.98, 84.52) * mm, "end": v(56.36, 84.76) * mm});
            skLineSegment(sketch, "E1275", {"start": v(56.36, 84.76) * mm, "end": v(57.27, 84.1) * mm});
            skLineSegment(sketch, "E1276", {"start": v(57.27, 84.1) * mm, "end": v(57.14, 83.66) * mm});
            skLineSegment(sketch, "E1277", {"start": v(57.14, 83.66) * mm, "end": v(56.88, 82.8) * mm});
            skLineSegment(sketch, "E1278", {"start": v(56.88, 82.8) * mm, "end": v(56.74, 82.38) * mm});
            skLineSegment(sketch, "E1279", {"start": v(56.74, 82.38) * mm, "end": v(57.66, 81.68) * mm});
            skLineSegment(sketch, "E1280", {"start": v(57.66, 81.68) * mm, "end": v(58.03, 81.93) * mm});
            skLineSegment(sketch, "E1281", {"start": v(58.03, 81.93) * mm, "end": v(58.78, 82.4) * mm});
            skLineSegment(sketch, "E1282", {"start": v(58.78, 82.4) * mm, "end": v(59.17, 82.63) * mm});
            skLineSegment(sketch, "E1283", {"start": v(59.17, 82.63) * mm, "end": v(60.05, 81.93) * mm});
            skLineSegment(sketch, "E1284", {"start": v(60.05, 81.93) * mm, "end": v(59.92, 81.5) * mm});
            skLineSegment(sketch, "E1285", {"start": v(59.92, 81.5) * mm, "end": v(59.63, 80.66) * mm});
            skLineSegment(sketch, "E1286", {"start": v(59.63, 80.66) * mm, "end": v(59.48, 80.24) * mm});
            skLineSegment(sketch, "E1287", {"start": v(59.48, 80.24) * mm, "end": v(60.36, 79.51) * mm});
            skLineSegment(sketch, "E1288", {"start": v(60.36, 79.51) * mm, "end": v(60.74, 79.74) * mm});
            skLineSegment(sketch, "E1289", {"start": v(60.74, 79.74) * mm, "end": v(61.52, 80.2) * mm});
            skLineSegment(sketch, "E1290", {"start": v(61.52, 80.2) * mm, "end": v(61.9, 80.41) * mm});
            skLineSegment(sketch, "E1291", {"start": v(61.9, 80.41) * mm, "end": v(62.77, 79.68) * mm});
            skLineSegment(sketch, "E1292", {"start": v(62.77, 79.68) * mm, "end": v(62.62, 79.26) * mm});
            skLineSegment(sketch, "E1293", {"start": v(62.62, 79.26) * mm, "end": v(62.3, 78.42) * mm});
            skLineSegment(sketch, "E1294", {"start": v(62.3, 78.42) * mm, "end": v(62.13, 78) * mm});
            skLineSegment(sketch, "E1295", {"start": v(62.13, 78) * mm, "end": v(63, 77.25) * mm});
            skLineSegment(sketch, "E1296", {"start": v(63, 77.25) * mm, "end": v(63.39, 77.47) * mm});
            skLineSegment(sketch, "E1297", {"start": v(63.39, 77.47) * mm, "end": v(64.17, 77.9) * mm});
            skLineSegment(sketch, "E1298", {"start": v(64.17, 77.9) * mm, "end": v(64.57, 78.1) * mm});
            skLineSegment(sketch, "E1299", {"start": v(64.57, 78.1) * mm, "end": v(65.4, 77.34) * mm});
            skLineSegment(sketch, "E1300", {"start": v(65.4, 77.34) * mm, "end": v(65.24, 76.92) * mm});
            skLineSegment(sketch, "E1301", {"start": v(65.24, 76.92) * mm, "end": v(64.9, 76.1) * mm});
            skLineSegment(sketch, "E1302", {"start": v(64.9, 76.1) * mm, "end": v(64.72, 75.69) * mm});
            skLineSegment(sketch, "E1303", {"start": v(64.72, 75.69) * mm, "end": v(65.55, 74.9) * mm});
            skLineSegment(sketch, "E1304", {"start": v(65.55, 74.9) * mm, "end": v(65.95, 75.1) * mm});
            skLineSegment(sketch, "E1305", {"start": v(65.95, 75.1) * mm, "end": v(66.75, 75.5) * mm});
            skLineSegment(sketch, "E1306", {"start": v(66.75, 75.5) * mm, "end": v(67.16, 75.7) * mm});
            skLineSegment(sketch, "E1307", {"start": v(67.16, 75.7) * mm, "end": v(67.97, 74.9) * mm});
            skLineSegment(sketch, "E1308", {"start": v(67.97, 74.9) * mm, "end": v(67.79, 74.5) * mm});
            skLineSegment(sketch, "E1309", {"start": v(67.79, 74.5) * mm, "end": v(67.41, 73.68) * mm});
            skLineSegment(sketch, "E1310", {"start": v(67.41, 73.68) * mm, "end": v(67.22, 73.28) * mm});
            skLineSegment(sketch, "E1311", {"start": v(67.22, 73.28) * mm, "end": v(68.03, 72.47) * mm});
            skLineSegment(sketch, "E1312", {"start": v(68.03, 72.47) * mm, "end": v(68.43, 72.66) * mm});
            skLineSegment(sketch, "E1313", {"start": v(68.43, 72.66) * mm, "end": v(69.25, 73.03) * mm});
            skLineSegment(sketch, "E1314", {"start": v(69.25, 73.03) * mm, "end": v(69.66, 73.2) * mm});
            skLineSegment(sketch, "E1315", {"start": v(69.66, 73.2) * mm, "end": v(70.44, 72.4) * mm});
            skLineSegment(sketch, "E1316", {"start": v(70.44, 72.4) * mm, "end": v(70.25, 71.99) * mm});
            skLineSegment(sketch, "E1317", {"start": v(70.25, 71.99) * mm, "end": v(69.85, 71.19) * mm});
            skLineSegment(sketch, "E1318", {"start": v(69.85, 71.19) * mm, "end": v(69.64, 70.8) * mm});
            skLineSegment(sketch, "E1319", {"start": v(69.64, 70.8) * mm, "end": v(70.42, 69.95) * mm});
            skLineSegment(sketch, "E1320", {"start": v(70.42, 69.95) * mm, "end": v(70.83, 70.13) * mm});
            skLineSegment(sketch, "E1321", {"start": v(70.83, 70.13) * mm, "end": v(71.66, 70.47) * mm});
            skLineSegment(sketch, "E1322", {"start": v(71.66, 70.47) * mm, "end": v(72.07, 70.64) * mm});
            skLineSegment(sketch, "E1323", {"start": v(72.07, 70.64) * mm, "end": v(72.83, 69.8) * mm});
            skLineSegment(sketch, "E1324", {"start": v(72.83, 69.8) * mm, "end": v(72.62, 69.4) * mm});
            skLineSegment(sketch, "E1325", {"start": v(72.62, 69.4) * mm, "end": v(72.2, 68.61) * mm});
            skLineSegment(sketch, "E1326", {"start": v(72.2, 68.61) * mm, "end": v(71.98, 68.23) * mm});
            skLineSegment(sketch, "E1327", {"start": v(71.98, 68.23) * mm, "end": v(72.73, 67.36) * mm});
            skLineSegment(sketch, "E1328", {"start": v(72.73, 67.36) * mm, "end": v(73.14, 67.52) * mm});
            skLineSegment(sketch, "E1329", {"start": v(73.14, 67.52) * mm, "end": v(73.98, 67.84) * mm});
            skLineSegment(sketch, "E1330", {"start": v(73.98, 67.84) * mm, "end": v(74.4, 67.99) * mm});
            skLineSegment(sketch, "E1331", {"start": v(74.4, 67.99) * mm, "end": v(75.13, 67.12) * mm});
            skLineSegment(sketch, "E1332", {"start": v(75.13, 67.12) * mm, "end": v(74.91, 66.73) * mm});
            skLineSegment(sketch, "E1333", {"start": v(74.91, 66.73) * mm, "end": v(74.46, 65.96) * mm});
            skLineSegment(sketch, "E1334", {"start": v(74.46, 65.96) * mm, "end": v(74.23, 65.58) * mm});
            skLineSegment(sketch, "E1335", {"start": v(74.23, 65.58) * mm, "end": v(74.95, 64.69) * mm});
            skLineSegment(sketch, "E1336", {"start": v(74.95, 64.69) * mm, "end": v(75.37, 64.84) * mm});
            skLineSegment(sketch, "E1337", {"start": v(75.37, 64.84) * mm, "end": v(76.21, 65.12) * mm});
            skLineSegment(sketch, "E1338", {"start": v(76.21, 65.12) * mm, "end": v(76.64, 65.26) * mm});
            skLineSegment(sketch, "E1339", {"start": v(76.64, 65.26) * mm, "end": v(77.34, 64.37) * mm});
            skLineSegment(sketch, "E1340", {"start": v(77.34, 64.37) * mm, "end": v(77.1, 63.99) * mm});
            skLineSegment(sketch, "E1341", {"start": v(77.1, 63.99) * mm, "end": v(76.63, 63.23) * mm});
            skLineSegment(sketch, "E1342", {"start": v(76.63, 63.23) * mm, "end": v(76.38, 62.86) * mm});
            skLineSegment(sketch, "E1343", {"start": v(76.38, 62.86) * mm, "end": v(77.08, 61.95) * mm});
            skLineSegment(sketch, "E1344", {"start": v(77.08, 61.95) * mm, "end": v(77.5, 62.08) * mm});
            skLineSegment(sketch, "E1345", {"start": v(77.5, 62.08) * mm, "end": v(78.36, 62.34) * mm});
            skLineSegment(sketch, "E1346", {"start": v(78.36, 62.34) * mm, "end": v(78.79, 62.46) * mm});
            skLineSegment(sketch, "E1347", {"start": v(78.79, 62.46) * mm, "end": v(79.46, 61.55) * mm});
            skLineSegment(sketch, "E1348", {"start": v(79.46, 61.55) * mm, "end": v(79.2, 61.17) * mm});
            skLineSegment(sketch, "E1349", {"start": v(79.2, 61.17) * mm, "end": v(78.7, 60.43) * mm});
            skLineSegment(sketch, "E1350", {"start": v(78.7, 60.43) * mm, "end": v(78.45, 60.07) * mm});
            skLineSegment(sketch, "E1351", {"start": v(78.45, 60.07) * mm, "end": v(79.11, 59.13) * mm});
            skLineSegment(sketch, "E1352", {"start": v(79.11, 59.13) * mm, "end": v(79.54, 59.25) * mm});
            skLineSegment(sketch, "E1353", {"start": v(79.54, 59.25) * mm, "end": v(80.4, 59.48) * mm});
            skLineSegment(sketch, "E1354", {"start": v(80.4, 59.48) * mm, "end": v(80.84, 59.59) * mm});
            skLineSegment(sketch, "E1355", {"start": v(80.84, 59.59) * mm, "end": v(81.48, 58.65) * mm});
            skLineSegment(sketch, "E1356", {"start": v(81.48, 58.65) * mm, "end": v(81.22, 58.29) * mm});
            skLineSegment(sketch, "E1357", {"start": v(81.22, 58.29) * mm, "end": v(80.69, 57.57) * mm});
            skLineSegment(sketch, "E1358", {"start": v(80.69, 57.57) * mm, "end": v(80.42, 57.21) * mm});
            skLineSegment(sketch, "E1359", {"start": v(80.42, 57.21) * mm, "end": v(81.05, 56.25) * mm});
            skLineSegment(sketch, "E1360", {"start": v(81.05, 56.25) * mm, "end": v(81.48, 56.36) * mm});
            skLineSegment(sketch, "E1361", {"start": v(81.48, 56.36) * mm, "end": v(82.35, 56.56) * mm});
            skLineSegment(sketch, "E1362", {"start": v(82.35, 56.56) * mm, "end": v(82.8, 56.65) * mm});
            skLineSegment(sketch, "E1363", {"start": v(82.8, 56.65) * mm, "end": v(83.4, 55.7) * mm});
            skLineSegment(sketch, "E1364", {"start": v(83.4, 55.7) * mm, "end": v(83.13, 55.34) * mm});
            skLineSegment(sketch, "E1365", {"start": v(83.13, 55.34) * mm, "end": v(82.57, 54.63) * mm});
            skLineSegment(sketch, "E1366", {"start": v(82.57, 54.63) * mm, "end": v(82.3, 54.3) * mm});
            skLineSegment(sketch, "E1367", {"start": v(82.3, 54.3) * mm, "end": v(82.9, 53.3) * mm});
            skLineSegment(sketch, "E1368", {"start": v(82.9, 53.3) * mm, "end": v(83.33, 53.4) * mm});
            skLineSegment(sketch, "E1369", {"start": v(83.33, 53.4) * mm, "end": v(84.2, 53.57) * mm});
            skLineSegment(sketch, "E1370", {"start": v(84.2, 53.57) * mm, "end": v(84.65, 53.65) * mm});
            skLineSegment(sketch, "E1371", {"start": v(84.65, 53.65) * mm, "end": v(85.22, 52.67) * mm});
            skLineSegment(sketch, "E1372", {"start": v(85.22, 52.67) * mm, "end": v(84.93, 52.32) * mm});
            skLineSegment(sketch, "E1373", {"start": v(84.93, 52.32) * mm, "end": v(84.36, 51.64) * mm});
            skLineSegment(sketch, "E1374", {"start": v(84.36, 51.64) * mm, "end": v(84.07, 51.3) * mm});
            skLineSegment(sketch, "E1375", {"start": v(84.07, 51.3) * mm, "end": v(84.63, 50.3) * mm});
            skLineSegment(sketch, "E1376", {"start": v(84.63, 50.3) * mm, "end": v(85.07, 50.38) * mm});
            skLineSegment(sketch, "E1377", {"start": v(85.07, 50.38) * mm, "end": v(85.95, 50.52) * mm});
            skLineSegment(sketch, "E1378", {"start": v(85.95, 50.52) * mm, "end": v(86.4, 50.59) * mm});
            skLineSegment(sketch, "E1379", {"start": v(86.4, 50.59) * mm, "end": v(86.94, 49.6) * mm});
            skLineSegment(sketch, "E1380", {"start": v(86.94, 49.6) * mm, "end": v(86.64, 49.25) * mm});
            skLineSegment(sketch, "E1381", {"start": v(86.64, 49.25) * mm, "end": v(86.04, 48.59) * mm});
            skLineSegment(sketch, "E1382", {"start": v(86.04, 48.59) * mm, "end": v(85.74, 48.26) * mm});
            skLineSegment(sketch, "E1383", {"start": v(85.74, 48.26) * mm, "end": v(86.27, 47.25) * mm});
            skLineSegment(sketch, "E1384", {"start": v(86.27, 47.25) * mm, "end": v(86.71, 47.3) * mm});
            skLineSegment(sketch, "E1385", {"start": v(86.71, 47.3) * mm, "end": v(87.6, 47.42) * mm});
            skLineSegment(sketch, "E1386", {"start": v(87.6, 47.42) * mm, "end": v(88.04, 47.47) * mm});
            skLineSegment(sketch, "E1387", {"start": v(88.04, 47.47) * mm, "end": v(88.55, 46.46) * mm});
            skLineSegment(sketch, "E1388", {"start": v(88.55, 46.46) * mm, "end": v(88.24, 46.13) * mm});
            skLineSegment(sketch, "E1389", {"start": v(88.24, 46.13) * mm, "end": v(87.62, 45.48) * mm});
            skLineSegment(sketch, "E1390", {"start": v(87.62, 45.48) * mm, "end": v(87.31, 45.17) * mm});
            skLineSegment(sketch, "E1391", {"start": v(87.31, 45.17) * mm, "end": v(87.8, 44.13) * mm});
            skLineSegment(sketch, "E1392", {"start": v(87.8, 44.13) * mm, "end": v(88.25, 44.18) * mm});
            skLineSegment(sketch, "E1393", {"start": v(88.25, 44.18) * mm, "end": v(89.14, 44.26) * mm});
            skLineSegment(sketch, "E1394", {"start": v(89.14, 44.26) * mm, "end": v(89.59, 44.3) * mm});
            skLineSegment(sketch, "E1395", {"start": v(89.59, 44.3) * mm, "end": v(90.06, 43.27) * mm});
            skLineSegment(sketch, "E1396", {"start": v(90.06, 43.27) * mm, "end": v(89.74, 42.95) * mm});
            skLineSegment(sketch, "E1397", {"start": v(89.74, 42.95) * mm, "end": v(89.1, 42.32) * mm});
            skLineSegment(sketch, "E1398", {"start": v(89.1, 42.32) * mm, "end": v(88.78, 42.02) * mm});
            skLineSegment(sketch, "E1399", {"start": v(88.78, 42.02) * mm, "end": v(89.24, 40.97) * mm});
            skLineSegment(sketch, "E1400", {"start": v(89.24, 40.97) * mm, "end": v(89.68, 41) * mm});
            skLineSegment(sketch, "E1401", {"start": v(89.68, 41) * mm, "end": v(90.57, 41.05) * mm});
            skLineSegment(sketch, "E1402", {"start": v(90.57, 41.05) * mm, "end": v(91.02, 41.07) * mm});
            skLineSegment(sketch, "E1403", {"start": v(91.02, 41.07) * mm, "end": v(91.46, 40.03) * mm});
            skLineSegment(sketch, "E1404", {"start": v(91.46, 40.03) * mm, "end": v(91.13, 39.72) * mm});
            skLineSegment(sketch, "E1405", {"start": v(91.13, 39.72) * mm, "end": v(90.47, 39.12) * mm});
            skLineSegment(sketch, "E1406", {"start": v(90.47, 39.12) * mm, "end": v(90.13, 38.83) * mm});
            skLineSegment(sketch, "E1407", {"start": v(90.13, 38.83) * mm, "end": v(90.56, 37.76) * mm});
            skLineSegment(sketch, "E1408", {"start": v(90.56, 37.76) * mm, "end": v(91, 37.78) * mm});
            skLineSegment(sketch, "E1409", {"start": v(91, 37.78) * mm, "end": v(91.9, 37.8) * mm});
            skLineSegment(sketch, "E1410", {"start": v(91.9, 37.8) * mm, "end": v(92.35, 37.8) * mm});
            skLineSegment(sketch, "E1411", {"start": v(92.35, 37.8) * mm, "end": v(92.75, 36.74) * mm});
            skLineSegment(sketch, "E1412", {"start": v(92.75, 36.74) * mm, "end": v(92.4, 36.45) * mm});
            skLineSegment(sketch, "E1413", {"start": v(92.4, 36.45) * mm, "end": v(91.73, 35.87) * mm});
            skLineSegment(sketch, "E1414", {"start": v(91.73, 35.87) * mm, "end": v(91.38, 35.59) * mm});
            skLineSegment(sketch, "E1415", {"start": v(91.38, 35.59) * mm, "end": v(91.77, 34.5) * mm});
            skLineSegment(sketch, "E1416", {"start": v(91.77, 34.5) * mm, "end": v(92.22, 34.51) * mm});
            skLineSegment(sketch, "E1417", {"start": v(92.22, 34.51) * mm, "end": v(93.11, 34.5) * mm});
            skLineSegment(sketch, "E1418", {"start": v(93.11, 34.5) * mm, "end": v(93.56, 34.49) * mm});
            skLineSegment(sketch, "E1419", {"start": v(93.56, 34.49) * mm, "end": v(93.93, 33.42) * mm});
            skLineSegment(sketch, "E1420", {"start": v(93.93, 33.42) * mm, "end": v(93.58, 33.13) * mm});
            skLineSegment(sketch, "E1421", {"start": v(93.58, 33.13) * mm, "end": v(92.88, 32.58) * mm});
            skLineSegment(sketch, "E1422", {"start": v(92.88, 32.58) * mm, "end": v(92.52, 32.3) * mm});
            skLineSegment(sketch, "E1423", {"start": v(92.52, 32.3) * mm, "end": v(92.88, 31.22) * mm});
            skLineSegment(sketch, "E1424", {"start": v(92.88, 31.22) * mm, "end": v(93.32, 31.2) * mm});
            skLineSegment(sketch, "E1425", {"start": v(93.32, 31.2) * mm, "end": v(94.21, 31.16) * mm});
            skLineSegment(sketch, "E1426", {"start": v(94.21, 31.16) * mm, "end": v(94.66, 31.14) * mm});
            skLineSegment(sketch, "E1427", {"start": v(94.66, 31.14) * mm, "end": v(95, 30.05) * mm});
            skLineSegment(sketch, "E1428", {"start": v(95, 30.05) * mm, "end": v(94.64, 29.78) * mm});
            skLineSegment(sketch, "E1429", {"start": v(94.64, 29.78) * mm, "end": v(93.92, 29.25) * mm});
            skLineSegment(sketch, "E1430", {"start": v(93.92, 29.25) * mm, "end": v(93.55, 29) * mm});
            skLineSegment(sketch, "E1431", {"start": v(93.55, 29) * mm, "end": v(93.87, 27.89) * mm});
            skLineSegment(sketch, "E1432", {"start": v(93.87, 27.89) * mm, "end": v(94.31, 27.86) * mm});
            skLineSegment(sketch, "E1433", {"start": v(94.31, 27.86) * mm, "end": v(95.2, 27.8) * mm});
            skLineSegment(sketch, "E1434", {"start": v(95.2, 27.8) * mm, "end": v(95.65, 27.75) * mm});
            skLineSegment(sketch, "E1435", {"start": v(95.65, 27.75) * mm, "end": v(95.95, 26.66) * mm});
            skLineSegment(sketch, "E1436", {"start": v(95.95, 26.66) * mm, "end": v(95.58, 26.4) * mm});
            skLineSegment(sketch, "E1437", {"start": v(95.58, 26.4) * mm, "end": v(94.84, 25.89) * mm});
            skLineSegment(sketch, "E1438", {"start": v(94.84, 25.89) * mm, "end": v(94.47, 25.65) * mm});
            skLineSegment(sketch, "E1439", {"start": v(94.47, 25.65) * mm, "end": v(94.75, 24.53) * mm});
            skLineSegment(sketch, "E1440", {"start": v(94.75, 24.53) * mm, "end": v(95.2, 24.49) * mm});
            skLineSegment(sketch, "E1441", {"start": v(95.2, 24.49) * mm, "end": v(96.08, 24.39) * mm});
            skLineSegment(sketch, "E1442", {"start": v(96.08, 24.39) * mm, "end": v(96.53, 24.33) * mm});
            skLineSegment(sketch, "E1443", {"start": v(96.53, 24.33) * mm, "end": v(96.78, 23.23) * mm});
            skLineSegment(sketch, "E1444", {"start": v(96.78, 23.23) * mm, "end": v(96.4, 22.98) * mm});
            skLineSegment(sketch, "E1445", {"start": v(96.4, 22.98) * mm, "end": v(95.66, 22.5) * mm});
            skLineSegment(sketch, "E1446", {"start": v(95.66, 22.5) * mm, "end": v(95.28, 22.27) * mm});
            skLineSegment(sketch, "E1447", {"start": v(95.28, 22.27) * mm, "end": v(95.52, 21.15) * mm});
            skLineSegment(sketch, "E1448", {"start": v(95.52, 21.15) * mm, "end": v(95.96, 21.09) * mm});
            skLineSegment(sketch, "E1449", {"start": v(95.96, 21.09) * mm, "end": v(96.84, 20.96) * mm});
            skLineSegment(sketch, "E1450", {"start": v(96.84, 20.96) * mm, "end": v(97.29, 20.89) * mm});
            skLineSegment(sketch, "E1451", {"start": v(97.29, 20.89) * mm, "end": v(97.5, 19.78) * mm});
            skLineSegment(sketch, "E1452", {"start": v(97.5, 19.78) * mm, "end": v(97.12, 19.54) * mm});
            skLineSegment(sketch, "E1453", {"start": v(97.12, 19.54) * mm, "end": v(96.36, 19.09) * mm});
            skLineSegment(sketch, "E1454", {"start": v(96.36, 19.09) * mm, "end": v(95.97, 18.87) * mm});
            skLineSegment(sketch, "E1455", {"start": v(95.97, 18.87) * mm, "end": v(96.17, 17.74) * mm});
            skLineSegment(sketch, "E1456", {"start": v(96.17, 17.74) * mm, "end": v(96.61, 17.66) * mm});
            skLineSegment(sketch, "E1457", {"start": v(96.61, 17.66) * mm, "end": v(97.5, 17.5) * mm});
            skLineSegment(sketch, "E1458", {"start": v(97.5, 17.5) * mm, "end": v(97.93, 17.42) * mm});
            skLineSegment(sketch, "E1459", {"start": v(97.93, 17.42) * mm, "end": v(98.11, 16.3) * mm});
            skLineSegment(sketch, "E1460", {"start": v(98.11, 16.3) * mm, "end": v(97.72, 16.08) * mm});
            skLineSegment(sketch, "E1461", {"start": v(97.72, 16.08) * mm, "end": v(96.94, 15.65) * mm});
            skLineSegment(sketch, "E1462", {"start": v(96.94, 15.65) * mm, "end": v(96.55, 15.44) * mm});
            skLineSegment(sketch, "E1463", {"start": v(96.55, 15.44) * mm, "end": v(96.71, 14.3) * mm});
            skLineSegment(sketch, "E1464", {"start": v(96.71, 14.3) * mm, "end": v(97.15, 14.22) * mm});
            skLineSegment(sketch, "E1465", {"start": v(97.15, 14.22) * mm, "end": v(98.02, 14.03) * mm});
            skLineSegment(sketch, "E1466", {"start": v(98.02, 14.03) * mm, "end": v(98.46, 13.93) * mm});
            skLineSegment(sketch, "E1467", {"start": v(98.46, 13.93) * mm, "end": v(98.6, 12.8) * mm});
            skLineSegment(sketch, "E1468", {"start": v(98.6, 12.8) * mm, "end": v(98.2, 12.6) * mm});
            skLineSegment(sketch, "E1469", {"start": v(98.2, 12.6) * mm, "end": v(97.4, 12.2) * mm});
            skLineSegment(sketch, "E1470", {"start": v(97.4, 12.2) * mm, "end": v(97, 12) * mm});
            skLineSegment(sketch, "E1471", {"start": v(97, 12) * mm, "end": v(97.13, 10.86) * mm});
            skLineSegment(sketch, "E1472", {"start": v(97.13, 10.86) * mm, "end": v(97.57, 10.76) * mm});
            skLineSegment(sketch, "E1473", {"start": v(97.57, 10.76) * mm, "end": v(98.43, 10.54) * mm});
            skLineSegment(sketch, "E1474", {"start": v(98.43, 10.54) * mm, "end": v(98.87, 10.42) * mm});
            skLineSegment(sketch, "E1475", {"start": v(98.87, 10.42) * mm, "end": v(98.97, 9.3) * mm});
            skLineSegment(sketch, "E1476", {"start": v(98.97, 9.3) * mm, "end": v(98.57, 9.1) * mm});
            skLineSegment(sketch, "E1477", {"start": v(98.57, 9.1) * mm, "end": v(97.76, 8.73) * mm});
            skLineSegment(sketch, "E1478", {"start": v(97.76, 8.73) * mm, "end": v(97.35, 8.55) * mm});
            skLineSegment(sketch, "E1479", {"start": v(97.35, 8.55) * mm, "end": v(97.44, 7.4) * mm});
            skLineSegment(sketch, "E1480", {"start": v(97.44, 7.4) * mm, "end": v(97.87, 7.29) * mm});
            skLineSegment(sketch, "E1481", {"start": v(97.87, 7.29) * mm, "end": v(98.73, 7.04) * mm});
            skLineSegment(sketch, "E1482", {"start": v(98.73, 7.04) * mm, "end": v(99.16, 6.9) * mm});
            skLineSegment(sketch, "E1483", {"start": v(99.16, 6.9) * mm, "end": v(99.23, 5.78) * mm});
            skLineSegment(sketch, "E1484", {"start": v(99.23, 5.78) * mm, "end": v(98.82, 5.6) * mm});
            skLineSegment(sketch, "E1485", {"start": v(98.82, 5.6) * mm, "end": v(98, 5.25) * mm});
            skLineSegment(sketch, "E1486", {"start": v(98, 5.25) * mm, "end": v(97.58, 5.08) * mm});
            skLineSegment(sketch, "E1487", {"start": v(97.58, 5.08) * mm, "end": v(97.63, 3.94) * mm});
            skLineSegment(sketch, "E1488", {"start": v(97.63, 3.94) * mm, "end": v(98.06, 3.8) * mm});
            skLineSegment(sketch, "E1489", {"start": v(98.06, 3.8) * mm, "end": v(98.9, 3.53) * mm});
            skLineSegment(sketch, "E1490", {"start": v(98.9, 3.53) * mm, "end": v(99.33, 3.38) * mm});
            skLineSegment(sketch, "E1491", {"start": v(99.33, 3.38) * mm, "end": v(99.36, 2.26) * mm});
            skLineSegment(sketch, "E1492", {"start": v(99.36, 2.26) * mm, "end": v(98.95, 2.09) * mm});
            skLineSegment(sketch, "E1493", {"start": v(98.95, 2.09) * mm, "end": v(98.11, 1.77) * mm});
            skLineSegment(sketch, "E1494", {"start": v(98.11, 1.77) * mm, "end": v(97.7, 1.61) * mm});
            skLineSegment(sketch, "E1495", {"start": v(97.7, 1.61) * mm, "end": v(97.7, 0.47) * mm});
            skLineSegment(sketch, "E1496", {"start": v(17.25, 6.14) * mm, "end": v(84.93, 5.69) * mm});
            skLineSegment(sketch, "E1497", {"start": v(84.93, 5.69) * mm, "end": v(87.84, 8.82) * mm});
            skLineSegment(sketch, "E1498", {"start": v(87.84, 8.82) * mm, "end": v(86.99, 15.38) * mm});
            skLineSegment(sketch, "E1499", {"start": v(86.99, 15.38) * mm, "end": v(85.67, 21.86) * mm});
            skLineSegment(sketch, "E1500", {"start": v(85.67, 21.86) * mm, "end": v(83.9, 28.23) * mm});
            skLineSegment(sketch, "E1501", {"start": v(83.9, 28.23) * mm, "end": v(81.7, 34.47) * mm});
            skLineSegment(sketch, "E1502", {"start": v(81.7, 34.47) * mm, "end": v(79.06, 40.53) * mm});
            skLineSegment(sketch, "E1503", {"start": v(79.06, 40.53) * mm, "end": v(76, 46.39) * mm});
            skLineSegment(sketch, "E1504", {"start": v(76, 46.39) * mm, "end": v(72.52, 52.02) * mm});
            skLineSegment(sketch, "E1505", {"start": v(72.52, 52.02) * mm, "end": v(68.67, 57.4) * mm});
            skLineSegment(sketch, "E1506", {"start": v(68.67, 57.4) * mm, "end": v(64.44, 62.48) * mm});
            skLineSegment(sketch, "E1507", {"start": v(64.44, 62.48) * mm, "end": v(59.87, 67.26) * mm});
            skLineSegment(sketch, "E1508", {"start": v(59.87, 67.26) * mm, "end": v(54.97, 71.7) * mm});
            skLineSegment(sketch, "E1509", {"start": v(54.97, 71.7) * mm, "end": v(49.77, 75.79) * mm});
            skLineSegment(sketch, "E1510", {"start": v(49.77, 75.79) * mm, "end": v(45.6, 74.9) * mm});
            skLineSegment(sketch, "E1511", {"start": v(45.6, 74.9) * mm, "end": v(11.36, 16.5) * mm});
            skLineSegment(sketch, "E1512", {"start": v(11.36, 16.5) * mm, "end": v(11.83, 11.07) * mm});
            skLineSegment(sketch, "E1513", {"start": v(11.83, 11.07) * mm, "end": v(17.25, 6.14) * mm});
            skLineSegment(sketch, "E1514", {"start": v(0.5, 22.88) * mm, "end": v(34.73, 81.27) * mm});
            skLineSegment(sketch, "E1515", {"start": v(34.73, 81.27) * mm, "end": v(33.47, 85.35) * mm});
            skLineSegment(sketch, "E1516", {"start": v(33.47, 85.35) * mm, "end": v(27.36, 87.89) * mm});
            skLineSegment(sketch, "E1517", {"start": v(27.36, 87.89) * mm, "end": v(21.1, 90) * mm});
            skLineSegment(sketch, "E1518", {"start": v(21.1, 90) * mm, "end": v(14.7, 91.65) * mm});
            skLineSegment(sketch, "E1519", {"start": v(14.7, 91.65) * mm, "end": v(8.19, 92.85) * mm});
            skLineSegment(sketch, "E1520", {"start": v(8.19, 92.85) * mm, "end": v(1.62, 93.6) * mm});
            skLineSegment(sketch, "E1521", {"start": v(1.62, 93.6) * mm, "end": v(-4.99, 93.87) * mm});
            skLineSegment(sketch, "E1522", {"start": v(-4.99, 93.87) * mm, "end": v(-11.6, 93.68) * mm});
            skLineSegment(sketch, "E1523", {"start": v(-11.6, 93.68) * mm, "end": v(-18.18, 93.03) * mm});
            skLineSegment(sketch, "E1524", {"start": v(-18.18, 93.03) * mm, "end": v(-24.7, 91.92) * mm});
            skLineSegment(sketch, "E1525", {"start": v(-24.7, 91.92) * mm, "end": v(-31.12, 90.34) * mm});
            skLineSegment(sketch, "E1526", {"start": v(-31.12, 90.34) * mm, "end": v(-37.42, 88.32) * mm});
            skLineSegment(sketch, "E1527", {"start": v(-37.42, 88.32) * mm, "end": v(-43.56, 85.87) * mm});
            skLineSegment(sketch, "E1528", {"start": v(-43.56, 85.87) * mm, "end": v(-44.87, 81.8) * mm});
            skLineSegment(sketch, "E1529", {"start": v(-44.87, 81.8) * mm, "end": v(-11.43, 22.96) * mm});
            skLineSegment(sketch, "E1530", {"start": v(-11.43, 22.96) * mm, "end": v(-6.49, 20.65) * mm});
            skLineSegment(sketch, "E1531", {"start": v(-6.49, 20.65) * mm, "end": v(0.5, 22.88) * mm});
            skLineSegment(sketch, "E1532", {"start": v(-22.38, 16.73) * mm, "end": v(-55.83, 75.57) * mm});
            skLineSegment(sketch, "E1533", {"start": v(-55.83, 75.57) * mm, "end": v(-60, 76.53) * mm});
            skLineSegment(sketch, "E1534", {"start": v(-60, 76.53) * mm, "end": v(-65.24, 72.5) * mm});
            skLineSegment(sketch, "E1535", {"start": v(-65.24, 72.5) * mm, "end": v(-70.2, 68.13) * mm});
            skLineSegment(sketch, "E1536", {"start": v(-70.2, 68.13) * mm, "end": v(-74.84, 63.42) * mm});
            skLineSegment(sketch, "E1537", {"start": v(-74.84, 63.42) * mm, "end": v(-79.13, 58.39) * mm});
            skLineSegment(sketch, "E1538", {"start": v(-79.13, 58.39) * mm, "end": v(-83.06, 53.06) * mm});
            skLineSegment(sketch, "E1539", {"start": v(-83.06, 53.06) * mm, "end": v(-86.6, 47.48) * mm});
            skLineSegment(sketch, "E1540", {"start": v(-86.6, 47.48) * mm, "end": v(-89.75, 41.66) * mm});
            skLineSegment(sketch, "E1541", {"start": v(-89.75, 41.66) * mm, "end": v(-92.47, 35.64) * mm});
            skLineSegment(sketch, "E1542", {"start": v(-92.47, 35.64) * mm, "end": v(-94.76, 29.43) * mm});
            skLineSegment(sketch, "E1543", {"start": v(-94.76, 29.43) * mm, "end": v(-96.61, 23.09) * mm});
            skLineSegment(sketch, "E1544", {"start": v(-96.61, 23.09) * mm, "end": v(-98.01, 16.62) * mm});
            skLineSegment(sketch, "E1545", {"start": v(-98.01, 16.62) * mm, "end": v(-98.95, 10.08) * mm});
            skLineSegment(sketch, "E1546", {"start": v(-98.95, 10.08) * mm, "end": v(-96.1, 6.9) * mm});
            skLineSegment(sketch, "E1547", {"start": v(-96.1, 6.9) * mm, "end": v(-28.4, 6.45) * mm});
            skLineSegment(sketch, "E1548", {"start": v(-28.4, 6.45) * mm, "end": v(-23.93, 9.57) * mm});
            skLineSegment(sketch, "E1549", {"start": v(-23.93, 9.57) * mm, "end": v(-22.38, 16.73) * mm});
            skLineSegment(sketch, "E1550", {"start": v(-28.5, -6.15) * mm, "end": v(-96.18, -5.7) * mm});
            skLineSegment(sketch, "E1551", {"start": v(-96.18, -5.7) * mm, "end": v(-99.08, -8.82) * mm});
            skLineSegment(sketch, "E1552", {"start": v(-99.08, -8.82) * mm, "end": v(-98.23, -15.38) * mm});
            skLineSegment(sketch, "E1553", {"start": v(-98.23, -15.38) * mm, "end": v(-96.92, -21.86) * mm});
            skLineSegment(sketch, "E1554", {"start": v(-96.92, -21.86) * mm, "end": v(-95.15, -28.24) * mm});
            skLineSegment(sketch, "E1555", {"start": v(-95.15, -28.24) * mm, "end": v(-92.94, -34.47) * mm});
            skLineSegment(sketch, "E1556", {"start": v(-92.94, -34.47) * mm, "end": v(-90.3, -40.53) * mm});
            skLineSegment(sketch, "E1557", {"start": v(-90.3, -40.53) * mm, "end": v(-87.23, -46.4) * mm});
            skLineSegment(sketch, "E1558", {"start": v(-87.23, -46.4) * mm, "end": v(-83.77, -52.02) * mm});
            skLineSegment(sketch, "E1559", {"start": v(-83.77, -52.02) * mm, "end": v(-79.9, -57.4) * mm});
            skLineSegment(sketch, "E1560", {"start": v(-79.9, -57.4) * mm, "end": v(-75.68, -62.48) * mm});
            skLineSegment(sketch, "E1561", {"start": v(-75.68, -62.48) * mm, "end": v(-71.11, -67.26) * mm});
            skLineSegment(sketch, "E1562", {"start": v(-71.11, -67.26) * mm, "end": v(-66.21, -71.7) * mm});
            skLineSegment(sketch, "E1563", {"start": v(-66.21, -71.7) * mm, "end": v(-61.02, -75.8) * mm});
            skLineSegment(sketch, "E1564", {"start": v(-61.02, -75.8) * mm, "end": v(-56.84, -74.9) * mm});
            skLineSegment(sketch, "E1565", {"start": v(-56.84, -74.9) * mm, "end": v(-22.6, -16.51) * mm});
            skLineSegment(sketch, "E1566", {"start": v(-22.6, -16.51) * mm, "end": v(-23.07, -11.08) * mm});
            skLineSegment(sketch, "E1567", {"start": v(-23.07, -11.08) * mm, "end": v(-28.5, -6.15) * mm});
            skLineSegment(sketch, "E1568", {"start": v(-11.73, -22.88) * mm, "end": v(-45.97, -81.27) * mm});
            skLineSegment(sketch, "E1569", {"start": v(-45.97, -81.27) * mm, "end": v(-44.71, -85.35) * mm});
            skLineSegment(sketch, "E1570", {"start": v(-44.71, -85.35) * mm, "end": v(-38.6, -87.9) * mm});
            skLineSegment(sketch, "E1571", {"start": v(-38.6, -87.9) * mm, "end": v(-32.34, -90) * mm});
            skLineSegment(sketch, "E1572", {"start": v(-32.34, -90) * mm, "end": v(-25.93, -91.65) * mm});
            skLineSegment(sketch, "E1573", {"start": v(-25.93, -91.65) * mm, "end": v(-19.43, -92.86) * mm});
            skLineSegment(sketch, "E1574", {"start": v(-19.43, -92.86) * mm, "end": v(-12.86, -93.6) * mm});
            skLineSegment(sketch, "E1575", {"start": v(-12.86, -93.6) * mm, "end": v(-6.25, -93.88) * mm});
            skLineSegment(sketch, "E1576", {"start": v(-6.25, -93.88) * mm, "end": v(0.36, -93.69) * mm});
            skLineSegment(sketch, "E1577", {"start": v(0.36, -93.69) * mm, "end": v(6.94, -93.03) * mm});
            skLineSegment(sketch, "E1578", {"start": v(6.94, -93.03) * mm, "end": v(13.46, -91.92) * mm});
            skLineSegment(sketch, "E1579", {"start": v(13.46, -91.92) * mm, "end": v(19.88, -90.35) * mm});
            skLineSegment(sketch, "E1580", {"start": v(19.88, -90.35) * mm, "end": v(26.18, -88.33) * mm});
            skLineSegment(sketch, "E1581", {"start": v(26.18, -88.33) * mm, "end": v(32.32, -85.87) * mm});
            skLineSegment(sketch, "E1582", {"start": v(32.32, -85.87) * mm, "end": v(33.63, -81.8) * mm});
            skLineSegment(sketch, "E1583", {"start": v(33.63, -81.8) * mm, "end": v(0.18, -22.96) * mm});
            skLineSegment(sketch, "E1584", {"start": v(0.18, -22.96) * mm, "end": v(-4.75, -20.65) * mm});
            skLineSegment(sketch, "E1585", {"start": v(-4.75, -20.65) * mm, "end": v(-11.73, -22.88) * mm});
            skLineSegment(sketch, "E1586", {"start": v(11.14, -16.74) * mm, "end": v(44.59, -75.58) * mm});
            skLineSegment(sketch, "E1587", {"start": v(44.59, -75.58) * mm, "end": v(48.75, -76.53) * mm});
            skLineSegment(sketch, "E1588", {"start": v(48.75, -76.53) * mm, "end": v(54, -72.51) * mm});
            skLineSegment(sketch, "E1589", {"start": v(54, -72.51) * mm, "end": v(58.96, -68.14) * mm});
            skLineSegment(sketch, "E1590", {"start": v(58.96, -68.14) * mm, "end": v(63.6, -63.42) * mm});
            skLineSegment(sketch, "E1591", {"start": v(63.6, -63.42) * mm, "end": v(67.89, -58.39) * mm});
            skLineSegment(sketch, "E1592", {"start": v(67.89, -58.39) * mm, "end": v(71.82, -53.07) * mm});
            skLineSegment(sketch, "E1593", {"start": v(71.82, -53.07) * mm, "end": v(75.36, -47.49) * mm});
            skLineSegment(sketch, "E1594", {"start": v(75.36, -47.49) * mm, "end": v(78.5, -41.67) * mm});
            skLineSegment(sketch, "E1595", {"start": v(78.5, -41.67) * mm, "end": v(81.23, -35.64) * mm});
            skLineSegment(sketch, "E1596", {"start": v(81.23, -35.64) * mm, "end": v(83.52, -29.44) * mm});
            skLineSegment(sketch, "E1597", {"start": v(83.52, -29.44) * mm, "end": v(85.37, -23.09) * mm});
            skLineSegment(sketch, "E1598", {"start": v(85.37, -23.09) * mm, "end": v(86.77, -16.63) * mm});
            skLineSegment(sketch, "E1599", {"start": v(86.77, -16.63) * mm, "end": v(87.71, -10.08) * mm});
            skLineSegment(sketch, "E1600", {"start": v(87.71, -10.08) * mm, "end": v(84.85, -6.91) * mm});
            skLineSegment(sketch, "E1601", {"start": v(84.85, -6.91) * mm, "end": v(17.17, -6.46) * mm});
            skLineSegment(sketch, "E1602", {"start": v(17.17, -6.46) * mm, "end": v(12.7, -9.58) * mm});
            skLineSegment(sketch, "E1603", {"start": v(12.7, -9.58) * mm, "end": v(11.14, -16.74) * mm});
            skLineSegment(sketch, "E1604", {"start": v(-4.62, 0) * mm, "end": v(-4.65, 0.26) * mm});
            skLineSegment(sketch, "E1605", {"start": v(-4.65, 0.26) * mm, "end": v(-4.75, 0.5) * mm});
            skLineSegment(sketch, "E1606", {"start": v(-4.75, 0.5) * mm, "end": v(-4.91, 0.7) * mm});
            skLineSegment(sketch, "E1607", {"start": v(-4.91, 0.7) * mm, "end": v(-5.12, 0.86) * mm});
            skLineSegment(sketch, "E1608", {"start": v(-5.12, 0.86) * mm, "end": v(-5.36, 0.96) * mm});
            skLineSegment(sketch, "E1609", {"start": v(-5.36, 0.96) * mm, "end": v(-5.62, 1) * mm});
            skLineSegment(sketch, "E1610", {"start": v(-5.62, 1) * mm, "end": v(-5.88, 0.96) * mm});
            skLineSegment(sketch, "E1611", {"start": v(-5.88, 0.96) * mm, "end": v(-6.12, 0.86) * mm});
            skLineSegment(sketch, "E1612", {"start": v(-6.12, 0.86) * mm, "end": v(-6.33, 0.7) * mm});
            skLineSegment(sketch, "E1613", {"start": v(-6.33, 0.7) * mm, "end": v(-6.49, 0.5) * mm});
            skLineSegment(sketch, "E1614", {"start": v(-6.49, 0.5) * mm, "end": v(-6.59, 0.26) * mm});
            skLineSegment(sketch, "E1615", {"start": v(-6.59, 0.26) * mm, "end": v(-6.62, 0) * mm});
            skLineSegment(sketch, "E1616", {"start": v(-6.62, 0) * mm, "end": v(-6.59, -0.26) * mm});
            skLineSegment(sketch, "E1617", {"start": v(-6.59, -0.26) * mm, "end": v(-6.49, -0.5) * mm});
            skLineSegment(sketch, "E1618", {"start": v(-6.49, -0.5) * mm, "end": v(-6.33, -0.7) * mm});
            skLineSegment(sketch, "E1619", {"start": v(-6.33, -0.7) * mm, "end": v(-6.12, -0.87) * mm});
            skLineSegment(sketch, "E1620", {"start": v(-6.12, -0.87) * mm, "end": v(-5.88, -0.97) * mm});
            skLineSegment(sketch, "E1621", {"start": v(-5.88, -0.97) * mm, "end": v(-5.62, -1) * mm});
            skLineSegment(sketch, "E1622", {"start": v(-5.62, -1) * mm, "end": v(-5.36, -0.97) * mm});
            skLineSegment(sketch, "E1623", {"start": v(-5.36, -0.97) * mm, "end": v(-5.12, -0.87) * mm});
            skLineSegment(sketch, "E1624", {"start": v(-5.12, -0.87) * mm, "end": v(-4.91, -0.7) * mm});
            skLineSegment(sketch, "E1625", {"start": v(-4.91, -0.7) * mm, "end": v(-4.75, -0.5) * mm});
            skLineSegment(sketch, "E1626", {"start": v(-4.75, -0.5) * mm, "end": v(-4.65, -0.26) * mm});
            skLineSegment(sketch, "E1627", {"start": v(-4.65, -0.26) * mm, "end": v(-4.62, 0) * mm});
            skLineSegment(sketch, "E1628", {"start": v(101.77, -0.12) * mm, "end": v(101.7, 0) * mm});
            skLineSegment(sketch, "E1629", {"start": v(101.7, 0) * mm, "end": v(101.65, 0.04) * mm});
            skLineSegment(sketch, "E1630", {"start": v(101.65, 0.04) * mm, "end": v(101.54, 0.09) * mm});
            skLineSegment(sketch, "E1631", {"start": v(101.54, 0.09) * mm, "end": v(101.43, 0.1) * mm});
            skLineSegment(sketch, "E1632", {"start": v(101.43, 0.1) * mm, "end": v(101.2, 0.1) * mm});
            skLineSegment(sketch, "E1633", {"start": v(101.2, 0.1) * mm, "end": v(100.98, 0.15) * mm});
            skLineSegment(sketch, "E1634", {"start": v(100.98, 0.15) * mm, "end": v(100.76, 0.25) * mm});
            skLineSegment(sketch, "E1635", {"start": v(100.76, 0.25) * mm, "end": v(100.55, 0.38) * mm});
            skLineSegment(sketch, "E1636", {"start": v(100.55, 0.38) * mm, "end": v(100.34, 0.55) * mm});
            skLineSegment(sketch, "E1637", {"start": v(100.34, 0.55) * mm, "end": v(100.14, 0.74) * mm});
            skLineSegment(sketch, "E1638", {"start": v(100.14, 0.74) * mm, "end": v(100.23, 1.23) * mm});
            skLineSegment(sketch, "E1639", {"start": v(100.23, 1.23) * mm, "end": v(100.37, 1.72) * mm});
            skLineSegment(sketch, "E1640", {"start": v(100.37, 1.72) * mm, "end": v(100.64, 1.8) * mm});
            skLineSegment(sketch, "E1641", {"start": v(100.64, 1.8) * mm, "end": v(100.9, 1.85) * mm});
            skLineSegment(sketch, "E1642", {"start": v(100.9, 1.85) * mm, "end": v(101.15, 1.87) * mm});
            skLineSegment(sketch, "E1643", {"start": v(101.15, 1.87) * mm, "end": v(101.4, 1.86) * mm});
            skLineSegment(sketch, "E1644", {"start": v(101.4, 1.86) * mm, "end": v(101.61, 1.8) * mm});
            skLineSegment(sketch, "E1645", {"start": v(101.61, 1.8) * mm, "end": v(101.81, 1.7) * mm});
            skLineSegment(sketch, "E1646", {"start": v(101.81, 1.7) * mm, "end": v(101.92, 1.66) * mm});
            skLineSegment(sketch, "E1647", {"start": v(101.92, 1.66) * mm, "end": v(102.04, 1.65) * mm});
            skLineSegment(sketch, "E1648", {"start": v(102.04, 1.65) * mm, "end": v(102.1, 1.66) * mm});
            skLineSegment(sketch, "E1649", {"start": v(102.1, 1.66) * mm, "end": v(102.21, 1.74) * mm});
            skLineSegment(sketch, "E1650", {"start": v(102.21, 1.74) * mm, "end": v(102.46, 2.12) * mm});
            skLineSegment(sketch, "E1651", {"start": v(102.46, 2.12) * mm, "end": v(102.75, 2.47) * mm});
            skLineSegment(sketch, "E1652", {"start": v(102.75, 2.47) * mm, "end": v(102.79, 2.6) * mm});
            skLineSegment(sketch, "E1653", {"start": v(102.79, 2.6) * mm, "end": v(102.78, 2.66) * mm});
            skLineSegment(sketch, "E1654", {"start": v(102.78, 2.66) * mm, "end": v(102.73, 2.78) * mm});
            skLineSegment(sketch, "E1655", {"start": v(102.73, 2.78) * mm, "end": v(102.66, 2.87) * mm});
            skLineSegment(sketch, "E1656", {"start": v(102.66, 2.87) * mm, "end": v(102.5, 3.03) * mm});
            skLineSegment(sketch, "E1657", {"start": v(102.5, 3.03) * mm, "end": v(102.38, 3.22) * mm});
            skLineSegment(sketch, "E1658", {"start": v(102.38, 3.22) * mm, "end": v(102.3, 3.44) * mm});
            skLineSegment(sketch, "E1659", {"start": v(102.3, 3.44) * mm, "end": v(102.24, 3.69) * mm});
            skLineSegment(sketch, "E1660", {"start": v(102.24, 3.69) * mm, "end": v(102.2, 3.95) * mm});
            skLineSegment(sketch, "E1661", {"start": v(102.2, 3.95) * mm, "end": v(102.2, 4.23) * mm});
            skLineSegment(sketch, "E1662", {"start": v(102.2, 4.23) * mm, "end": v(102.61, 4.51) * mm});
            skLineSegment(sketch, "E1663", {"start": v(102.61, 4.51) * mm, "end": v(103.06, 4.76) * mm});
            skLineSegment(sketch, "E1664", {"start": v(103.06, 4.76) * mm, "end": v(103.3, 4.62) * mm});
            skLineSegment(sketch, "E1665", {"start": v(103.3, 4.62) * mm, "end": v(103.52, 4.47) * mm});
            skLineSegment(sketch, "E1666", {"start": v(103.52, 4.47) * mm, "end": v(103.71, 4.31) * mm});
            skLineSegment(sketch, "E1667", {"start": v(103.71, 4.31) * mm, "end": v(103.88, 4.13) * mm});
            skLineSegment(sketch, "E1668", {"start": v(103.88, 4.13) * mm, "end": v(104, 3.94) * mm});
            skLineSegment(sketch, "E1669", {"start": v(104, 3.94) * mm, "end": v(104.06, 3.72) * mm});
            skLineSegment(sketch, "E1670", {"start": v(104.06, 3.72) * mm, "end": v(104.11, 3.62) * mm});
            skLineSegment(sketch, "E1671", {"start": v(104.11, 3.62) * mm, "end": v(104.19, 3.53) * mm});
            skLineSegment(sketch, "E1672", {"start": v(104.19, 3.53) * mm, "end": v(104.24, 3.49) * mm});
            skLineSegment(sketch, "E1673", {"start": v(104.24, 3.49) * mm, "end": v(104.37, 3.47) * mm});
            skLineSegment(sketch, "E1674", {"start": v(104.37, 3.47) * mm, "end": v(104.82, 3.57) * mm});
            skLineSegment(sketch, "E1675", {"start": v(104.82, 3.57) * mm, "end": v(105.27, 3.61) * mm});
            skLineSegment(sketch, "E1676", {"start": v(105.27, 3.61) * mm, "end": v(105.38, 3.67) * mm});
            skLineSegment(sketch, "E1677", {"start": v(105.38, 3.67) * mm, "end": v(105.43, 3.73) * mm});
            skLineSegment(sketch, "E1678", {"start": v(105.43, 3.73) * mm, "end": v(105.47, 3.84) * mm});
            skLineSegment(sketch, "E1679", {"start": v(105.47, 3.84) * mm, "end": v(105.5, 3.95) * mm});
            skLineSegment(sketch, "E1680", {"start": v(105.5, 3.95) * mm, "end": v(105.49, 4.17) * mm});
            skLineSegment(sketch, "E1681", {"start": v(105.49, 4.17) * mm, "end": v(105.54, 4.4) * mm});
            skLineSegment(sketch, "E1682", {"start": v(105.54, 4.4) * mm, "end": v(105.63, 4.62) * mm});
            skLineSegment(sketch, "E1683", {"start": v(105.63, 4.62) * mm, "end": v(105.77, 4.83) * mm});
            skLineSegment(sketch, "E1684", {"start": v(105.77, 4.83) * mm, "end": v(105.93, 5.04) * mm});
            skLineSegment(sketch, "E1685", {"start": v(105.93, 5.04) * mm, "end": v(106.12, 5.24) * mm});
            skLineSegment(sketch, "E1686", {"start": v(106.12, 5.24) * mm, "end": v(106.62, 5.15) * mm});
            skLineSegment(sketch, "E1687", {"start": v(106.62, 5.15) * mm, "end": v(107.1, 5) * mm});
            skLineSegment(sketch, "E1688", {"start": v(107.1, 5) * mm, "end": v(107.18, 4.74) * mm});
            skLineSegment(sketch, "E1689", {"start": v(107.18, 4.74) * mm, "end": v(107.23, 4.48) * mm});
            skLineSegment(sketch, "E1690", {"start": v(107.23, 4.48) * mm, "end": v(107.25, 4.23) * mm});
            skLineSegment(sketch, "E1691", {"start": v(107.25, 4.23) * mm, "end": v(107.24, 3.99) * mm});
            skLineSegment(sketch, "E1692", {"start": v(107.24, 3.99) * mm, "end": v(107.18, 3.77) * mm});
            skLineSegment(sketch, "E1693", {"start": v(107.18, 3.77) * mm, "end": v(107.08, 3.57) * mm});
            skLineSegment(sketch, "E1694", {"start": v(107.08, 3.57) * mm, "end": v(107.05, 3.46) * mm});
            skLineSegment(sketch, "E1695", {"start": v(107.05, 3.46) * mm, "end": v(107.04, 3.34) * mm});
            skLineSegment(sketch, "E1696", {"start": v(107.04, 3.34) * mm, "end": v(107.05, 3.27) * mm});
            skLineSegment(sketch, "E1697", {"start": v(107.05, 3.27) * mm, "end": v(107.12, 3.17) * mm});
            skLineSegment(sketch, "E1698", {"start": v(107.12, 3.17) * mm, "end": v(107.5, 2.92) * mm});
            skLineSegment(sketch, "E1699", {"start": v(107.5, 2.92) * mm, "end": v(107.86, 2.63) * mm});
            skLineSegment(sketch, "E1700", {"start": v(107.86, 2.63) * mm, "end": v(107.98, 2.6) * mm});
            skLineSegment(sketch, "E1701", {"start": v(107.98, 2.6) * mm, "end": v(108.05, 2.6) * mm});
            skLineSegment(sketch, "E1702", {"start": v(108.05, 2.6) * mm, "end": v(108.16, 2.65) * mm});
            skLineSegment(sketch, "E1703", {"start": v(108.16, 2.65) * mm, "end": v(108.25, 2.71) * mm});
            skLineSegment(sketch, "E1704", {"start": v(108.25, 2.71) * mm, "end": v(108.4, 2.87) * mm});
            skLineSegment(sketch, "E1705", {"start": v(108.4, 2.87) * mm, "end": v(108.6, 3) * mm});
            skLineSegment(sketch, "E1706", {"start": v(108.6, 3) * mm, "end": v(108.83, 3.08) * mm});
            skLineSegment(sketch, "E1707", {"start": v(108.83, 3.08) * mm, "end": v(109.07, 3.14) * mm});
            skLineSegment(sketch, "E1708", {"start": v(109.07, 3.14) * mm, "end": v(109.33, 3.18) * mm});
            skLineSegment(sketch, "E1709", {"start": v(109.33, 3.18) * mm, "end": v(109.61, 3.18) * mm});
            skLineSegment(sketch, "E1710", {"start": v(109.61, 3.18) * mm, "end": v(109.9, 2.77) * mm});
            skLineSegment(sketch, "E1711", {"start": v(109.9, 2.77) * mm, "end": v(110.14, 2.32) * mm});
            skLineSegment(sketch, "E1712", {"start": v(110.14, 2.32) * mm, "end": v(110, 2.08) * mm});
            skLineSegment(sketch, "E1713", {"start": v(110, 2.08) * mm, "end": v(109.86, 1.86) * mm});
            skLineSegment(sketch, "E1714", {"start": v(109.86, 1.86) * mm, "end": v(109.7, 1.67) * mm});
            skLineSegment(sketch, "E1715", {"start": v(109.7, 1.67) * mm, "end": v(109.52, 1.5) * mm});
            skLineSegment(sketch, "E1716", {"start": v(109.52, 1.5) * mm, "end": v(109.32, 1.39) * mm});
            skLineSegment(sketch, "E1717", {"start": v(109.32, 1.39) * mm, "end": v(109.1, 1.32) * mm});
            skLineSegment(sketch, "E1718", {"start": v(109.1, 1.32) * mm, "end": v(109, 1.27) * mm});
            skLineSegment(sketch, "E1719", {"start": v(109, 1.27) * mm, "end": v(108.91, 1.2) * mm});
            skLineSegment(sketch, "E1720", {"start": v(108.91, 1.2) * mm, "end": v(108.87, 1.14) * mm});
            skLineSegment(sketch, "E1721", {"start": v(108.87, 1.14) * mm, "end": v(108.85, 1) * mm});
            skLineSegment(sketch, "E1722", {"start": v(108.85, 1) * mm, "end": v(108.95, 0.56) * mm});
            skLineSegment(sketch, "E1723", {"start": v(108.95, 0.56) * mm, "end": v(109, 0.11) * mm});
            skLineSegment(sketch, "E1724", {"start": v(109, 0.11) * mm, "end": v(109.05, 0) * mm});
            skLineSegment(sketch, "E1725", {"start": v(109.05, 0) * mm, "end": v(109.11, -0.05) * mm});
            skLineSegment(sketch, "E1726", {"start": v(109.11, -0.05) * mm, "end": v(109.22, -0.1) * mm});
            skLineSegment(sketch, "E1727", {"start": v(109.22, -0.1) * mm, "end": v(109.33, -0.11) * mm});
            skLineSegment(sketch, "E1728", {"start": v(109.33, -0.11) * mm, "end": v(109.56, -0.1) * mm});
            skLineSegment(sketch, "E1729", {"start": v(109.56, -0.1) * mm, "end": v(109.78, -0.16) * mm});
            skLineSegment(sketch, "E1730", {"start": v(109.78, -0.16) * mm, "end": v(110, -0.26) * mm});
            skLineSegment(sketch, "E1731", {"start": v(110, -0.26) * mm, "end": v(110.21, -0.39) * mm});
            skLineSegment(sketch, "E1732", {"start": v(110.21, -0.39) * mm, "end": v(110.42, -0.55) * mm});
            skLineSegment(sketch, "E1733", {"start": v(110.42, -0.55) * mm, "end": v(110.63, -0.74) * mm});
            skLineSegment(sketch, "E1734", {"start": v(110.63, -0.74) * mm, "end": v(110.53, -1.24) * mm});
            skLineSegment(sketch, "E1735", {"start": v(110.53, -1.24) * mm, "end": v(110.39, -1.73) * mm});
            skLineSegment(sketch, "E1736", {"start": v(110.39, -1.73) * mm, "end": v(110.12, -1.8) * mm});
            skLineSegment(sketch, "E1737", {"start": v(110.12, -1.8) * mm, "end": v(109.86, -1.85) * mm});
            skLineSegment(sketch, "E1738", {"start": v(109.86, -1.85) * mm, "end": v(109.61, -1.87) * mm});
            skLineSegment(sketch, "E1739", {"start": v(109.61, -1.87) * mm, "end": v(109.37, -1.86) * mm});
            skLineSegment(sketch, "E1740", {"start": v(109.37, -1.86) * mm, "end": v(109.15, -1.8) * mm});
            skLineSegment(sketch, "E1741", {"start": v(109.15, -1.8) * mm, "end": v(108.95, -1.7) * mm});
            skLineSegment(sketch, "E1742", {"start": v(108.95, -1.7) * mm, "end": v(108.84, -1.67) * mm});
            skLineSegment(sketch, "E1743", {"start": v(108.84, -1.67) * mm, "end": v(108.72, -1.66) * mm});
            skLineSegment(sketch, "E1744", {"start": v(108.72, -1.66) * mm, "end": v(108.66, -1.67) * mm});
            skLineSegment(sketch, "E1745", {"start": v(108.66, -1.67) * mm, "end": v(108.55, -1.74) * mm});
            skLineSegment(sketch, "E1746", {"start": v(108.55, -1.74) * mm, "end": v(108.3, -2.13) * mm});
            skLineSegment(sketch, "E1747", {"start": v(108.3, -2.13) * mm, "end": v(108.02, -2.48) * mm});
            skLineSegment(sketch, "E1748", {"start": v(108.02, -2.48) * mm, "end": v(107.98, -2.6) * mm});
            skLineSegment(sketch, "E1749", {"start": v(107.98, -2.6) * mm, "end": v(107.99, -2.67) * mm});
            skLineSegment(sketch, "E1750", {"start": v(107.99, -2.67) * mm, "end": v(108.03, -2.78) * mm});
            skLineSegment(sketch, "E1751", {"start": v(108.03, -2.78) * mm, "end": v(108.1, -2.87) * mm});
            skLineSegment(sketch, "E1752", {"start": v(108.1, -2.87) * mm, "end": v(108.26, -3.03) * mm});
            skLineSegment(sketch, "E1753", {"start": v(108.26, -3.03) * mm, "end": v(108.38, -3.22) * mm});
            skLineSegment(sketch, "E1754", {"start": v(108.38, -3.22) * mm, "end": v(108.47, -3.45) * mm});
            skLineSegment(sketch, "E1755", {"start": v(108.47, -3.45) * mm, "end": v(108.53, -3.7) * mm});
            skLineSegment(sketch, "E1756", {"start": v(108.53, -3.7) * mm, "end": v(108.56, -3.96) * mm});
            skLineSegment(sketch, "E1757", {"start": v(108.56, -3.96) * mm, "end": v(108.57, -4.23) * mm});
            skLineSegment(sketch, "E1758", {"start": v(108.57, -4.23) * mm, "end": v(108.15, -4.52) * mm});
            skLineSegment(sketch, "E1759", {"start": v(108.15, -4.52) * mm, "end": v(107.7, -4.76) * mm});
            skLineSegment(sketch, "E1760", {"start": v(107.7, -4.76) * mm, "end": v(107.46, -4.63) * mm});
            skLineSegment(sketch, "E1761", {"start": v(107.46, -4.63) * mm, "end": v(107.24, -4.48) * mm});
            skLineSegment(sketch, "E1762", {"start": v(107.24, -4.48) * mm, "end": v(107.05, -4.32) * mm});
            skLineSegment(sketch, "E1763", {"start": v(107.05, -4.32) * mm, "end": v(106.89, -4.14) * mm});
            skLineSegment(sketch, "E1764", {"start": v(106.89, -4.14) * mm, "end": v(106.77, -3.94) * mm});
            skLineSegment(sketch, "E1765", {"start": v(106.77, -3.94) * mm, "end": v(106.7, -3.73) * mm});
            skLineSegment(sketch, "E1766", {"start": v(106.7, -3.73) * mm, "end": v(106.65, -3.63) * mm});
            skLineSegment(sketch, "E1767", {"start": v(106.65, -3.63) * mm, "end": v(106.58, -3.53) * mm});
            skLineSegment(sketch, "E1768", {"start": v(106.58, -3.53) * mm, "end": v(106.52, -3.5) * mm});
            skLineSegment(sketch, "E1769", {"start": v(106.52, -3.5) * mm, "end": v(106.4, -3.48) * mm});
            skLineSegment(sketch, "E1770", {"start": v(106.4, -3.48) * mm, "end": v(105.95, -3.57) * mm});
            skLineSegment(sketch, "E1771", {"start": v(105.95, -3.57) * mm, "end": v(105.5, -3.62) * mm});
            skLineSegment(sketch, "E1772", {"start": v(105.5, -3.62) * mm, "end": v(105.38, -3.67) * mm});
            skLineSegment(sketch, "E1773", {"start": v(105.38, -3.67) * mm, "end": v(105.34, -3.73) * mm});
            skLineSegment(sketch, "E1774", {"start": v(105.34, -3.73) * mm, "end": v(105.3, -3.84) * mm});
            skLineSegment(sketch, "E1775", {"start": v(105.3, -3.84) * mm, "end": v(105.27, -3.95) * mm});
            skLineSegment(sketch, "E1776", {"start": v(105.27, -3.95) * mm, "end": v(105.28, -4.18) * mm});
            skLineSegment(sketch, "E1777", {"start": v(105.28, -4.18) * mm, "end": v(105.23, -4.4) * mm});
            skLineSegment(sketch, "E1778", {"start": v(105.23, -4.4) * mm, "end": v(105.13, -4.62) * mm});
            skLineSegment(sketch, "E1779", {"start": v(105.13, -4.62) * mm, "end": v(105, -4.83) * mm});
            skLineSegment(sketch, "E1780", {"start": v(105, -4.83) * mm, "end": v(104.83, -5.04) * mm});
            skLineSegment(sketch, "E1781", {"start": v(104.83, -5.04) * mm, "end": v(104.64, -5.25) * mm});
            skLineSegment(sketch, "E1782", {"start": v(104.64, -5.25) * mm, "end": v(104.15, -5.15) * mm});
            skLineSegment(sketch, "E1783", {"start": v(104.15, -5.15) * mm, "end": v(103.66, -5) * mm});
            skLineSegment(sketch, "E1784", {"start": v(103.66, -5) * mm, "end": v(103.58, -4.74) * mm});
            skLineSegment(sketch, "E1785", {"start": v(103.58, -4.74) * mm, "end": v(103.53, -4.48) * mm});
            skLineSegment(sketch, "E1786", {"start": v(103.53, -4.48) * mm, "end": v(103.51, -4.23) * mm});
            skLineSegment(sketch, "E1787", {"start": v(103.51, -4.23) * mm, "end": v(103.52, -4) * mm});
            skLineSegment(sketch, "E1788", {"start": v(103.52, -4) * mm, "end": v(103.58, -3.77) * mm});
            skLineSegment(sketch, "E1789", {"start": v(103.58, -3.77) * mm, "end": v(103.68, -3.57) * mm});
            skLineSegment(sketch, "E1790", {"start": v(103.68, -3.57) * mm, "end": v(103.72, -3.46) * mm});
            skLineSegment(sketch, "E1791", {"start": v(103.72, -3.46) * mm, "end": v(103.73, -3.34) * mm});
            skLineSegment(sketch, "E1792", {"start": v(103.73, -3.34) * mm, "end": v(103.72, -3.28) * mm});
            skLineSegment(sketch, "E1793", {"start": v(103.72, -3.28) * mm, "end": v(103.64, -3.17) * mm});
            skLineSegment(sketch, "E1794", {"start": v(103.64, -3.17) * mm, "end": v(103.26, -2.93) * mm});
            skLineSegment(sketch, "E1795", {"start": v(103.26, -2.93) * mm, "end": v(102.9, -2.64) * mm});
            skLineSegment(sketch, "E1796", {"start": v(102.9, -2.64) * mm, "end": v(102.78, -2.6) * mm});
            skLineSegment(sketch, "E1797", {"start": v(102.78, -2.6) * mm, "end": v(102.71, -2.6) * mm});
            skLineSegment(sketch, "E1798", {"start": v(102.71, -2.6) * mm, "end": v(102.6, -2.65) * mm});
            skLineSegment(sketch, "E1799", {"start": v(102.6, -2.65) * mm, "end": v(102.51, -2.72) * mm});
            skLineSegment(sketch, "E1800", {"start": v(102.51, -2.72) * mm, "end": v(102.35, -2.88) * mm});
            skLineSegment(sketch, "E1801", {"start": v(102.35, -2.88) * mm, "end": v(102.16, -3) * mm});
            skLineSegment(sketch, "E1802", {"start": v(102.16, -3) * mm, "end": v(101.94, -3.09) * mm});
            skLineSegment(sketch, "E1803", {"start": v(101.94, -3.09) * mm, "end": v(101.7, -3.15) * mm});
            skLineSegment(sketch, "E1804", {"start": v(101.7, -3.15) * mm, "end": v(101.43, -3.18) * mm});
            skLineSegment(sketch, "E1805", {"start": v(101.43, -3.18) * mm, "end": v(101.15, -3.19) * mm});
            skLineSegment(sketch, "E1806", {"start": v(101.15, -3.19) * mm, "end": v(100.87, -2.77) * mm});
            skLineSegment(sketch, "E1807", {"start": v(100.87, -2.77) * mm, "end": v(100.62, -2.32) * mm});
            skLineSegment(sketch, "E1808", {"start": v(100.62, -2.32) * mm, "end": v(100.76, -2.08) * mm});
            skLineSegment(sketch, "E1809", {"start": v(100.76, -2.08) * mm, "end": v(100.9, -1.86) * mm});
            skLineSegment(sketch, "E1810", {"start": v(100.9, -1.86) * mm, "end": v(101.07, -1.67) * mm});
            skLineSegment(sketch, "E1811", {"start": v(101.07, -1.67) * mm, "end": v(101.25, -1.5) * mm});
            skLineSegment(sketch, "E1812", {"start": v(101.25, -1.5) * mm, "end": v(101.44, -1.4) * mm});
            skLineSegment(sketch, "E1813", {"start": v(101.44, -1.4) * mm, "end": v(101.66, -1.33) * mm});
            skLineSegment(sketch, "E1814", {"start": v(101.66, -1.33) * mm, "end": v(101.76, -1.27) * mm});
            skLineSegment(sketch, "E1815", {"start": v(101.76, -1.27) * mm, "end": v(101.85, -1.2) * mm});
            skLineSegment(sketch, "E1816", {"start": v(101.85, -1.2) * mm, "end": v(101.89, -1.14) * mm});
            skLineSegment(sketch, "E1817", {"start": v(101.89, -1.14) * mm, "end": v(101.9, -1.01) * mm});
            skLineSegment(sketch, "E1818", {"start": v(101.9, -1.01) * mm, "end": v(101.8, -0.57) * mm});
            skLineSegment(sketch, "E1819", {"start": v(101.8, -0.57) * mm, "end": v(101.77, -0.12) * mm});
            skLineSegment(sketch, "E1820", {"start": v(106.13, 0) * mm, "end": v(106.1, 0.2) * mm});
            skLineSegment(sketch, "E1821", {"start": v(106.1, 0.2) * mm, "end": v(106.03, 0.37) * mm});
            skLineSegment(sketch, "E1822", {"start": v(106.03, 0.37) * mm, "end": v(105.91, 0.53) * mm});
            skLineSegment(sketch, "E1823", {"start": v(105.91, 0.53) * mm, "end": v(105.76, 0.65) * mm});
            skLineSegment(sketch, "E1824", {"start": v(105.76, 0.65) * mm, "end": v(105.58, 0.72) * mm});
            skLineSegment(sketch, "E1825", {"start": v(105.58, 0.72) * mm, "end": v(105.38, 0.75) * mm});
            skLineSegment(sketch, "E1826", {"start": v(105.38, 0.75) * mm, "end": v(105.19, 0.72) * mm});
            skLineSegment(sketch, "E1827", {"start": v(105.19, 0.72) * mm, "end": v(105, 0.65) * mm});
            skLineSegment(sketch, "E1828", {"start": v(105, 0.65) * mm, "end": v(104.85, 0.53) * mm});
            skLineSegment(sketch, "E1829", {"start": v(104.85, 0.53) * mm, "end": v(104.73, 0.37) * mm});
            skLineSegment(sketch, "E1830", {"start": v(104.73, 0.37) * mm, "end": v(104.66, 0.2) * mm});
            skLineSegment(sketch, "E1831", {"start": v(104.66, 0.2) * mm, "end": v(104.63, 0) * mm});
            skLineSegment(sketch, "E1832", {"start": v(104.63, 0) * mm, "end": v(104.66, -0.2) * mm});
            skLineSegment(sketch, "E1833", {"start": v(104.66, -0.2) * mm, "end": v(104.73, -0.38) * mm});
            skLineSegment(sketch, "E1834", {"start": v(104.73, -0.38) * mm, "end": v(104.85, -0.53) * mm});
            skLineSegment(sketch, "E1835", {"start": v(104.85, -0.53) * mm, "end": v(105, -0.65) * mm});
            skLineSegment(sketch, "E1836", {"start": v(105, -0.65) * mm, "end": v(105.19, -0.73) * mm});
            skLineSegment(sketch, "E1837", {"start": v(105.19, -0.73) * mm, "end": v(105.38, -0.75) * mm});
            skLineSegment(sketch, "E1838", {"start": v(105.38, -0.75) * mm, "end": v(105.58, -0.73) * mm});
            skLineSegment(sketch, "E1839", {"start": v(105.58, -0.73) * mm, "end": v(105.76, -0.65) * mm});
            skLineSegment(sketch, "E1840", {"start": v(105.76, -0.65) * mm, "end": v(105.91, -0.53) * mm});
            skLineSegment(sketch, "E1841", {"start": v(105.91, -0.53) * mm, "end": v(106.03, -0.38) * mm});
            skLineSegment(sketch, "E1842", {"start": v(106.03, -0.38) * mm, "end": v(106.1, -0.2) * mm});
            skLineSegment(sketch, "E1843", {"start": v(106.1, -0.2) * mm, "end": v(106.13, 0) * mm});
            skSolve(sketch);
        }
        {
            var Q0;
            Q0=makeQuery(id+"F0.imprint","IMPRINT",FACE,{"disambiguationData":[TD([[makeQuery(id+"F0.imprint","IMPRINT",EDGE,{"derivedFrom":sQuery(id+"F0.wireOp",EDGE,"E1628")}),-1.0]])]});
            extrude(context, id + "F1", {"entities" : qUnion([Q0]), "depth" : 3 * mm, "offsetDistance" : 25 * mm});
        }
    });
